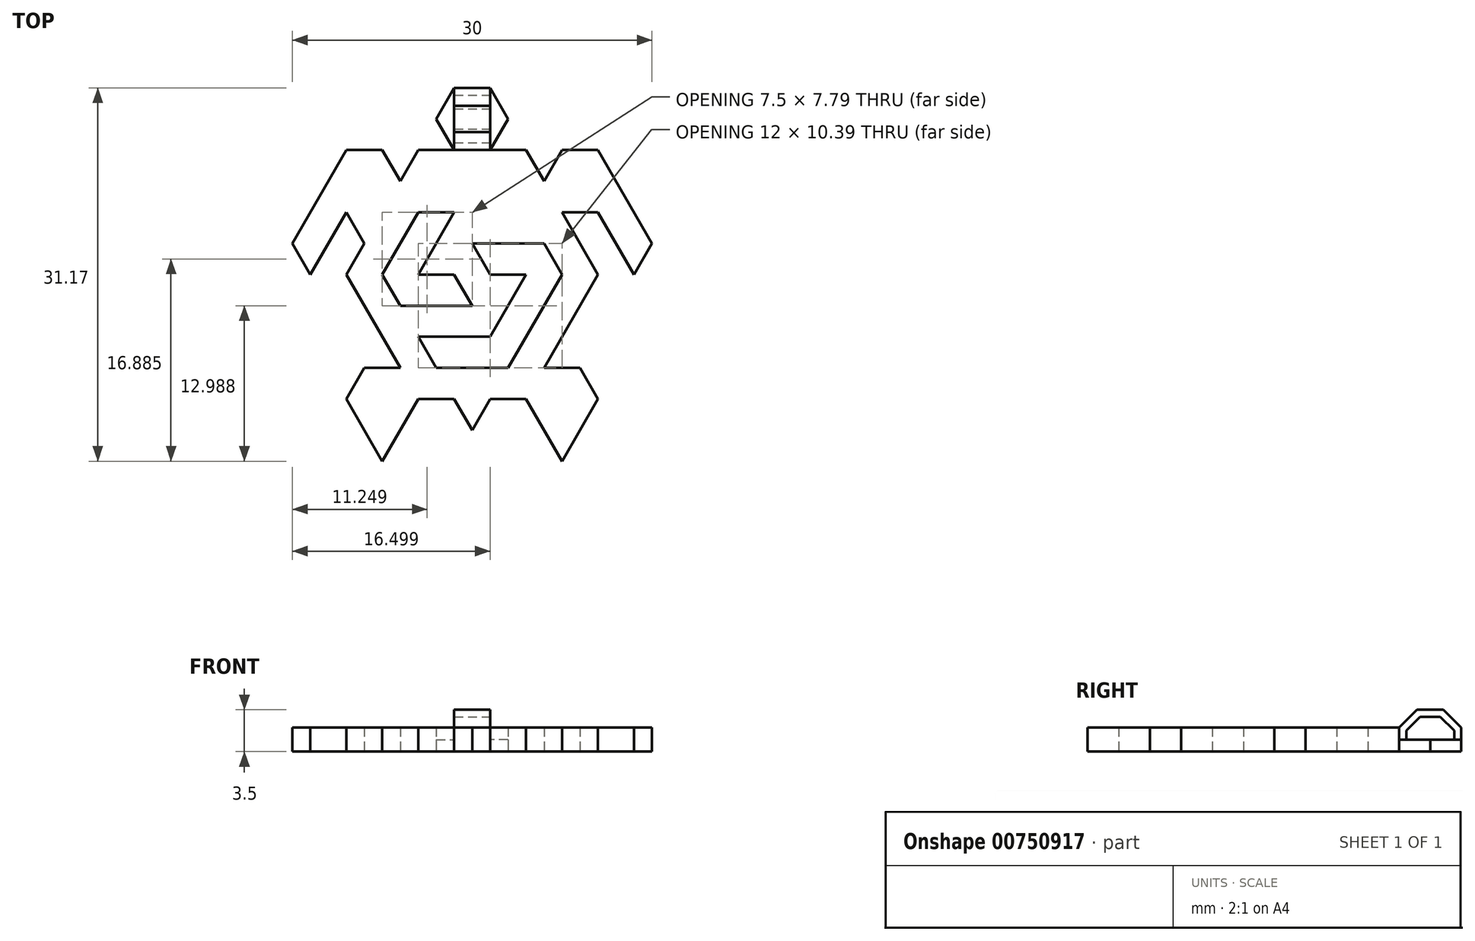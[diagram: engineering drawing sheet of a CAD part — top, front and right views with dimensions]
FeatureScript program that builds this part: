
annotation { "Feature Type Name" : "Feature", "Feature Type Description" : "" }
export const myFeature = defineFeature(function(context is Context, id is Id, definition is map)
    precondition{}
    {
        {
            var Q0;
            Q0=qCreatedBy(makeId("Top.planeOp"),FACE);
            var sketch = newSketch(context, id + "F0", { "sketchPlane" : qUnion([Q0])});
            skLineSegment(sketch, "E0", {"start": v(-15.95, 6.9) * mm, "end": v(-12.95, 6.9) * mm});
            skLineSegment(sketch, "E1", {"start": v(-12.95, 6.9) * mm, "end": v(-14.45, 9.5) * mm});
            skLineSegment(sketch, "E2", {"start": v(-14.45, 9.5) * mm, "end": v(-15.95, 6.9) * mm});
            skLineSegment(sketch, "E3", {"start": v(-14.45, 9.5) * mm, "end": v(-11.45, 9.5) * mm});
            skLineSegment(sketch, "E4", {"start": v(-11.45, 9.5) * mm, "end": v(-12.95, 6.9) * mm});
            skLineSegment(sketch, "E5", {"start": v(-11.45, 9.5) * mm, "end": v(-12.95, 12.1) * mm});
            skLineSegment(sketch, "E6", {"start": v(-14.45, 9.5) * mm, "end": v(-12.95, 12.1) * mm});
            skLineSegment(sketch, "E7", {"start": v(-12.95, 12.1) * mm, "end": v(-9.95, 12.1) * mm});
            skLineSegment(sketch, "E8", {"start": v(-9.95, 12.1) * mm, "end": v(-11.45, 9.5) * mm});
            skLineSegment(sketch, "E9.0.1.0", {"start": v(-15.95, 12.1) * mm, "end": v(-12.95, 12.1) * mm});
            skLineSegment(sketch, "E9.0.1.1", {"start": v(-14.45, 14.69) * mm, "end": v(-15.95, 12.1) * mm});
            skLineSegment(sketch, "E9.0.1.2", {"start": v(-12.95, 12.1) * mm, "end": v(-14.45, 14.69) * mm});
            skLineSegment(sketch, "E9.0.1.3", {"start": v(-14.45, 14.69) * mm, "end": v(-11.45, 14.69) * mm});
            skLineSegment(sketch, "E9.0.1.4", {"start": v(-14.45, 14.69) * mm, "end": v(-12.95, 17.29) * mm});
            skLineSegment(sketch, "E9.0.1.5", {"start": v(-11.45, 14.69) * mm, "end": v(-12.95, 17.29) * mm});
            skLineSegment(sketch, "E9.0.2.0", {"start": v(-15.95, 17.29) * mm, "end": v(-12.95, 17.29) * mm});
            skLineSegment(sketch, "E9.0.2.1", {"start": v(-14.45, 19.89) * mm, "end": v(-15.95, 17.29) * mm});
            skLineSegment(sketch, "E9.0.2.2", {"start": v(-12.95, 17.29) * mm, "end": v(-14.45, 19.89) * mm});
            skLineSegment(sketch, "E9.0.2.3", {"start": v(-14.45, 19.89) * mm, "end": v(-11.45, 19.89) * mm});
            skLineSegment(sketch, "E9.0.2.4", {"start": v(-14.45, 19.89) * mm, "end": v(-12.95, 22.48) * mm});
            skLineSegment(sketch, "E9.0.2.5", {"start": v(-11.45, 19.89) * mm, "end": v(-12.95, 22.48) * mm});
            skLineSegment(sketch, "E9.0.3.0", {"start": v(-15.95, 22.48) * mm, "end": v(-12.95, 22.48) * mm});
            skLineSegment(sketch, "E9.0.3.1", {"start": v(-14.45, 25.08) * mm, "end": v(-15.95, 22.48) * mm});
            skLineSegment(sketch, "E9.0.3.2", {"start": v(-12.95, 22.48) * mm, "end": v(-14.45, 25.08) * mm});
            skLineSegment(sketch, "E9.0.3.3", {"start": v(-14.45, 25.08) * mm, "end": v(-11.45, 25.08) * mm});
            skLineSegment(sketch, "E9.0.3.4", {"start": v(-14.45, 25.08) * mm, "end": v(-12.95, 27.68) * mm});
            skLineSegment(sketch, "E9.0.3.5", {"start": v(-11.45, 25.08) * mm, "end": v(-12.95, 27.68) * mm});
            skLineSegment(sketch, "E9.0.4.0", {"start": v(-15.95, 27.68) * mm, "end": v(-12.95, 27.68) * mm});
            skLineSegment(sketch, "E9.0.4.1", {"start": v(-14.45, 30.28) * mm, "end": v(-15.95, 27.68) * mm});
            skLineSegment(sketch, "E9.0.4.2", {"start": v(-12.95, 27.68) * mm, "end": v(-14.45, 30.28) * mm});
            skLineSegment(sketch, "E9.0.4.3", {"start": v(-14.45, 30.28) * mm, "end": v(-11.45, 30.28) * mm});
            skLineSegment(sketch, "E9.0.4.4", {"start": v(-14.45, 30.28) * mm, "end": v(-12.95, 32.88) * mm});
            skLineSegment(sketch, "E9.0.4.5", {"start": v(-11.45, 30.28) * mm, "end": v(-12.95, 32.88) * mm});
            skLineSegment(sketch, "E9.0.5.0", {"start": v(-15.95, 32.88) * mm, "end": v(-12.95, 32.88) * mm});
            skLineSegment(sketch, "E9.0.5.1", {"start": v(-14.45, 35.47) * mm, "end": v(-15.95, 32.88) * mm});
            skLineSegment(sketch, "E9.0.5.2", {"start": v(-12.95, 32.88) * mm, "end": v(-14.45, 35.47) * mm});
            skLineSegment(sketch, "E9.0.5.3", {"start": v(-14.45, 35.47) * mm, "end": v(-11.45, 35.47) * mm});
            skLineSegment(sketch, "E9.0.5.4", {"start": v(-14.45, 35.47) * mm, "end": v(-12.95, 38.07) * mm});
            skLineSegment(sketch, "E9.0.5.5", {"start": v(-11.45, 35.47) * mm, "end": v(-12.95, 38.07) * mm});
            skLineSegment(sketch, "E9.0.6.0", {"start": v(-15.95, 38.07) * mm, "end": v(-12.95, 38.07) * mm});
            skLineSegment(sketch, "E9.0.6.1", {"start": v(-14.45, 40.67) * mm, "end": v(-15.95, 38.07) * mm});
            skLineSegment(sketch, "E9.0.6.2", {"start": v(-12.95, 38.07) * mm, "end": v(-14.45, 40.67) * mm});
            skLineSegment(sketch, "E9.0.6.3", {"start": v(-14.45, 40.67) * mm, "end": v(-11.45, 40.67) * mm});
            skLineSegment(sketch, "E9.0.6.4", {"start": v(-14.45, 40.67) * mm, "end": v(-12.95, 43.27) * mm});
            skLineSegment(sketch, "E9.0.6.5", {"start": v(-11.45, 40.67) * mm, "end": v(-12.95, 43.27) * mm});
            skLineSegment(sketch, "E9.0.7.0", {"start": v(-15.95, 43.27) * mm, "end": v(-12.95, 43.27) * mm});
            skLineSegment(sketch, "E9.0.7.1", {"start": v(-14.45, 45.87) * mm, "end": v(-15.95, 43.27) * mm});
            skLineSegment(sketch, "E9.0.7.2", {"start": v(-12.95, 43.27) * mm, "end": v(-14.45, 45.87) * mm});
            skLineSegment(sketch, "E9.0.7.3", {"start": v(-14.45, 45.87) * mm, "end": v(-11.45, 45.87) * mm});
            skLineSegment(sketch, "E9.0.7.4", {"start": v(-14.45, 45.87) * mm, "end": v(-12.95, 48.46) * mm});
            skLineSegment(sketch, "E9.0.7.5", {"start": v(-11.45, 45.87) * mm, "end": v(-12.95, 48.46) * mm});
            skLineSegment(sketch, "E9.0.8.0", {"start": v(-15.95, 48.46) * mm, "end": v(-12.95, 48.46) * mm});
            skLineSegment(sketch, "E9.0.8.1", {"start": v(-14.45, 51.06) * mm, "end": v(-15.95, 48.46) * mm});
            skLineSegment(sketch, "E9.0.8.2", {"start": v(-12.95, 48.46) * mm, "end": v(-14.45, 51.06) * mm});
            skLineSegment(sketch, "E9.0.8.3", {"start": v(-14.45, 51.06) * mm, "end": v(-11.45, 51.06) * mm});
            skLineSegment(sketch, "E9.0.8.4", {"start": v(-14.45, 51.06) * mm, "end": v(-12.95, 53.66) * mm});
            skLineSegment(sketch, "E9.0.8.5", {"start": v(-11.45, 51.06) * mm, "end": v(-12.95, 53.66) * mm});
            skLineSegment(sketch, "E9.0.9.0", {"start": v(-15.95, 53.66) * mm, "end": v(-12.95, 53.66) * mm});
            skLineSegment(sketch, "E9.0.9.1", {"start": v(-14.45, 56.26) * mm, "end": v(-15.95, 53.66) * mm});
            skLineSegment(sketch, "E9.0.9.2", {"start": v(-12.95, 53.66) * mm, "end": v(-14.45, 56.26) * mm});
            skLineSegment(sketch, "E9.0.9.3", {"start": v(-14.45, 56.26) * mm, "end": v(-11.45, 56.26) * mm});
            skLineSegment(sketch, "E9.0.9.4", {"start": v(-14.45, 56.26) * mm, "end": v(-12.95, 58.86) * mm});
            skLineSegment(sketch, "E9.0.9.5", {"start": v(-11.45, 56.26) * mm, "end": v(-12.95, 58.86) * mm});
            skLineSegment(sketch, "E9.1.0.0", {"start": v(-12.95, 6.9) * mm, "end": v(-9.95, 6.9) * mm});
            skLineSegment(sketch, "E9.1.0.2", {"start": v(-9.95, 6.9) * mm, "end": v(-11.45, 9.5) * mm});
            skLineSegment(sketch, "E9.1.0.3", {"start": v(-11.45, 9.5) * mm, "end": v(-8.45, 9.5) * mm});
            skLineSegment(sketch, "E9.1.0.4", {"start": v(-11.45, 9.5) * mm, "end": v(-9.95, 12.1) * mm});
            skLineSegment(sketch, "E9.1.0.5", {"start": v(-8.45, 9.5) * mm, "end": v(-9.95, 12.1) * mm});
            skLineSegment(sketch, "E9.1.1.1", {"start": v(-11.45, 14.69) * mm, "end": v(-12.95, 12.1) * mm});
            skLineSegment(sketch, "E9.1.1.2", {"start": v(-9.95, 12.1) * mm, "end": v(-11.45, 14.69) * mm});
            skLineSegment(sketch, "E9.1.1.3", {"start": v(-11.45, 14.69) * mm, "end": v(-8.45, 14.69) * mm});
            skLineSegment(sketch, "E9.1.1.4", {"start": v(-11.45, 14.69) * mm, "end": v(-9.95, 17.29) * mm});
            skLineSegment(sketch, "E9.1.1.5", {"start": v(-8.45, 14.69) * mm, "end": v(-9.95, 17.29) * mm});
            skLineSegment(sketch, "E9.1.2.0", {"start": v(-12.95, 17.29) * mm, "end": v(-9.95, 17.29) * mm});
            skLineSegment(sketch, "E9.1.2.1", {"start": v(-11.45, 19.89) * mm, "end": v(-12.95, 17.29) * mm});
            skLineSegment(sketch, "E9.1.2.2", {"start": v(-9.95, 17.29) * mm, "end": v(-11.45, 19.89) * mm});
            skLineSegment(sketch, "E9.1.2.3", {"start": v(-11.45, 19.89) * mm, "end": v(-8.45, 19.89) * mm});
            skLineSegment(sketch, "E9.1.2.4", {"start": v(-11.45, 19.89) * mm, "end": v(-9.95, 22.48) * mm});
            skLineSegment(sketch, "E9.1.2.5", {"start": v(-8.45, 19.89) * mm, "end": v(-9.95, 22.48) * mm});
            skLineSegment(sketch, "E9.1.3.0", {"start": v(-12.95, 22.48) * mm, "end": v(-9.95, 22.48) * mm});
            skLineSegment(sketch, "E9.1.3.1", {"start": v(-11.45, 25.08) * mm, "end": v(-12.95, 22.48) * mm});
            skLineSegment(sketch, "E9.1.3.2", {"start": v(-9.95, 22.48) * mm, "end": v(-11.45, 25.08) * mm});
            skLineSegment(sketch, "E9.1.3.3", {"start": v(-11.45, 25.08) * mm, "end": v(-8.45, 25.08) * mm});
            skLineSegment(sketch, "E9.1.3.4", {"start": v(-11.45, 25.08) * mm, "end": v(-9.95, 27.68) * mm});
            skLineSegment(sketch, "E9.1.3.5", {"start": v(-8.45, 25.08) * mm, "end": v(-9.95, 27.68) * mm});
            skLineSegment(sketch, "E9.1.4.0", {"start": v(-12.95, 27.68) * mm, "end": v(-9.95, 27.68) * mm});
            skLineSegment(sketch, "E9.1.4.1", {"start": v(-11.45, 30.28) * mm, "end": v(-12.95, 27.68) * mm});
            skLineSegment(sketch, "E9.1.4.2", {"start": v(-9.95, 27.68) * mm, "end": v(-11.45, 30.28) * mm});
            skLineSegment(sketch, "E9.1.4.3", {"start": v(-11.45, 30.28) * mm, "end": v(-8.45, 30.28) * mm});
            skLineSegment(sketch, "E9.1.4.4", {"start": v(-11.45, 30.28) * mm, "end": v(-9.95, 32.88) * mm});
            skLineSegment(sketch, "E9.1.4.5", {"start": v(-8.45, 30.28) * mm, "end": v(-9.95, 32.88) * mm});
            skLineSegment(sketch, "E9.1.5.0", {"start": v(-12.95, 32.88) * mm, "end": v(-9.95, 32.88) * mm});
            skLineSegment(sketch, "E9.1.5.1", {"start": v(-11.45, 35.47) * mm, "end": v(-12.95, 32.88) * mm});
            skLineSegment(sketch, "E9.1.5.2", {"start": v(-9.95, 32.88) * mm, "end": v(-11.45, 35.47) * mm});
            skLineSegment(sketch, "E9.1.5.3", {"start": v(-11.45, 35.47) * mm, "end": v(-8.45, 35.47) * mm});
            skLineSegment(sketch, "E9.1.5.4", {"start": v(-11.45, 35.47) * mm, "end": v(-9.95, 38.07) * mm});
            skLineSegment(sketch, "E9.1.5.5", {"start": v(-8.45, 35.47) * mm, "end": v(-9.95, 38.07) * mm});
            skLineSegment(sketch, "E9.1.6.0", {"start": v(-12.95, 38.07) * mm, "end": v(-9.95, 38.07) * mm});
            skLineSegment(sketch, "E9.1.6.1", {"start": v(-11.45, 40.67) * mm, "end": v(-12.95, 38.07) * mm});
            skLineSegment(sketch, "E9.1.6.2", {"start": v(-9.95, 38.07) * mm, "end": v(-11.45, 40.67) * mm});
            skLineSegment(sketch, "E9.1.6.3", {"start": v(-11.45, 40.67) * mm, "end": v(-8.45, 40.67) * mm});
            skLineSegment(sketch, "E9.1.6.4", {"start": v(-11.45, 40.67) * mm, "end": v(-9.95, 43.27) * mm});
            skLineSegment(sketch, "E9.1.6.5", {"start": v(-8.45, 40.67) * mm, "end": v(-9.95, 43.27) * mm});
            skLineSegment(sketch, "E9.1.7.0", {"start": v(-12.95, 43.27) * mm, "end": v(-9.95, 43.27) * mm});
            skLineSegment(sketch, "E9.1.7.1", {"start": v(-11.45, 45.87) * mm, "end": v(-12.95, 43.27) * mm});
            skLineSegment(sketch, "E9.1.7.2", {"start": v(-9.95, 43.27) * mm, "end": v(-11.45, 45.87) * mm});
            skLineSegment(sketch, "E9.1.7.3", {"start": v(-11.45, 45.87) * mm, "end": v(-8.45, 45.87) * mm});
            skLineSegment(sketch, "E9.1.7.4", {"start": v(-11.45, 45.87) * mm, "end": v(-9.95, 48.46) * mm});
            skLineSegment(sketch, "E9.1.7.5", {"start": v(-8.45, 45.87) * mm, "end": v(-9.95, 48.46) * mm});
            skLineSegment(sketch, "E9.1.8.0", {"start": v(-12.95, 48.46) * mm, "end": v(-9.95, 48.46) * mm});
            skLineSegment(sketch, "E9.1.8.1", {"start": v(-11.45, 51.06) * mm, "end": v(-12.95, 48.46) * mm});
            skLineSegment(sketch, "E9.1.8.2", {"start": v(-9.95, 48.46) * mm, "end": v(-11.45, 51.06) * mm});
            skLineSegment(sketch, "E9.1.8.3", {"start": v(-11.45, 51.06) * mm, "end": v(-8.45, 51.06) * mm});
            skLineSegment(sketch, "E9.1.8.4", {"start": v(-11.45, 51.06) * mm, "end": v(-9.95, 53.66) * mm});
            skLineSegment(sketch, "E9.1.8.5", {"start": v(-8.45, 51.06) * mm, "end": v(-9.95, 53.66) * mm});
            skLineSegment(sketch, "E9.1.9.0", {"start": v(-12.95, 53.66) * mm, "end": v(-9.95, 53.66) * mm});
            skLineSegment(sketch, "E9.1.9.1", {"start": v(-11.45, 56.26) * mm, "end": v(-12.95, 53.66) * mm});
            skLineSegment(sketch, "E9.1.9.2", {"start": v(-9.95, 53.66) * mm, "end": v(-11.45, 56.26) * mm});
            skLineSegment(sketch, "E9.1.9.3", {"start": v(-11.45, 56.26) * mm, "end": v(-8.45, 56.26) * mm});
            skLineSegment(sketch, "E9.1.9.4", {"start": v(-11.45, 56.26) * mm, "end": v(-9.95, 58.86) * mm});
            skLineSegment(sketch, "E9.1.9.5", {"start": v(-8.45, 56.26) * mm, "end": v(-9.95, 58.86) * mm});
            skLineSegment(sketch, "E9.2.0.0", {"start": v(-9.95, 6.9) * mm, "end": v(-6.95, 6.9) * mm});
            skLineSegment(sketch, "E9.2.0.1", {"start": v(-8.45, 9.5) * mm, "end": v(-9.95, 6.9) * mm});
            skLineSegment(sketch, "E9.2.0.2", {"start": v(-6.95, 6.9) * mm, "end": v(-8.45, 9.5) * mm});
            skLineSegment(sketch, "E9.2.0.3", {"start": v(-8.45, 9.5) * mm, "end": v(-5.45, 9.5) * mm});
            skLineSegment(sketch, "E9.2.0.4", {"start": v(-8.45, 9.5) * mm, "end": v(-6.95, 12.1) * mm});
            skLineSegment(sketch, "E9.2.0.5", {"start": v(-5.45, 9.5) * mm, "end": v(-6.95, 12.1) * mm});
            skLineSegment(sketch, "E9.2.1.0", {"start": v(-9.95, 12.1) * mm, "end": v(-6.95, 12.1) * mm});
            skLineSegment(sketch, "E9.2.1.1", {"start": v(-8.45, 14.69) * mm, "end": v(-9.95, 12.1) * mm});
            skLineSegment(sketch, "E9.2.1.2", {"start": v(-6.95, 12.1) * mm, "end": v(-8.45, 14.69) * mm});
            skLineSegment(sketch, "E9.2.1.3", {"start": v(-8.45, 14.69) * mm, "end": v(-5.45, 14.69) * mm});
            skLineSegment(sketch, "E9.2.1.4", {"start": v(-8.45, 14.69) * mm, "end": v(-6.95, 17.29) * mm});
            skLineSegment(sketch, "E9.2.1.5", {"start": v(-5.45, 14.69) * mm, "end": v(-6.95, 17.29) * mm});
            skLineSegment(sketch, "E9.2.2.0", {"start": v(-9.95, 17.29) * mm, "end": v(-6.95, 17.29) * mm});
            skLineSegment(sketch, "E9.2.2.1", {"start": v(-8.45, 19.89) * mm, "end": v(-9.95, 17.29) * mm});
            skLineSegment(sketch, "E9.2.2.2", {"start": v(-6.95, 17.29) * mm, "end": v(-8.45, 19.89) * mm});
            skLineSegment(sketch, "E9.2.2.3", {"start": v(-8.45, 19.89) * mm, "end": v(-5.45, 19.89) * mm});
            skLineSegment(sketch, "E9.2.2.4", {"start": v(-8.45, 19.89) * mm, "end": v(-6.95, 22.48) * mm});
            skLineSegment(sketch, "E9.2.2.5", {"start": v(-5.45, 19.89) * mm, "end": v(-6.95, 22.48) * mm});
            skLineSegment(sketch, "E9.2.3.0", {"start": v(-9.95, 22.48) * mm, "end": v(-6.95, 22.48) * mm});
            skLineSegment(sketch, "E9.2.3.1", {"start": v(-8.45, 25.08) * mm, "end": v(-9.95, 22.48) * mm});
            skLineSegment(sketch, "E9.2.3.2", {"start": v(-6.95, 22.48) * mm, "end": v(-8.45, 25.08) * mm});
            skLineSegment(sketch, "E9.2.3.3", {"start": v(-8.45, 25.08) * mm, "end": v(-5.45, 25.08) * mm});
            skLineSegment(sketch, "E9.2.3.4", {"start": v(-8.45, 25.08) * mm, "end": v(-6.95, 27.68) * mm});
            skLineSegment(sketch, "E9.2.3.5", {"start": v(-5.45, 25.08) * mm, "end": v(-6.95, 27.68) * mm});
            skLineSegment(sketch, "E9.2.4.0", {"start": v(-9.95, 27.68) * mm, "end": v(-6.95, 27.68) * mm});
            skLineSegment(sketch, "E9.2.4.1", {"start": v(-8.45, 30.28) * mm, "end": v(-9.95, 27.68) * mm});
            skLineSegment(sketch, "E9.2.4.2", {"start": v(-6.95, 27.68) * mm, "end": v(-8.45, 30.28) * mm});
            skLineSegment(sketch, "E9.2.4.3", {"start": v(-8.45, 30.28) * mm, "end": v(-5.45, 30.28) * mm});
            skLineSegment(sketch, "E9.2.4.4", {"start": v(-8.45, 30.28) * mm, "end": v(-6.95, 32.88) * mm});
            skLineSegment(sketch, "E9.2.4.5", {"start": v(-5.45, 30.28) * mm, "end": v(-6.95, 32.88) * mm});
            skLineSegment(sketch, "E9.2.5.0", {"start": v(-9.95, 32.88) * mm, "end": v(-6.95, 32.88) * mm});
            skLineSegment(sketch, "E9.2.5.1", {"start": v(-8.45, 35.47) * mm, "end": v(-9.95, 32.88) * mm});
            skLineSegment(sketch, "E9.2.5.2", {"start": v(-6.95, 32.88) * mm, "end": v(-8.45, 35.47) * mm});
            skLineSegment(sketch, "E9.2.5.3", {"start": v(-8.45, 35.47) * mm, "end": v(-5.45, 35.47) * mm});
            skLineSegment(sketch, "E9.2.5.4", {"start": v(-8.45, 35.47) * mm, "end": v(-6.95, 38.07) * mm});
            skLineSegment(sketch, "E9.2.5.5", {"start": v(-5.45, 35.47) * mm, "end": v(-6.95, 38.07) * mm});
            skLineSegment(sketch, "E9.2.6.0", {"start": v(-9.95, 38.07) * mm, "end": v(-6.95, 38.07) * mm});
            skLineSegment(sketch, "E9.2.6.1", {"start": v(-8.45, 40.67) * mm, "end": v(-9.95, 38.07) * mm});
            skLineSegment(sketch, "E9.2.6.2", {"start": v(-6.95, 38.07) * mm, "end": v(-8.45, 40.67) * mm});
            skLineSegment(sketch, "E9.2.6.3", {"start": v(-8.45, 40.67) * mm, "end": v(-5.45, 40.67) * mm});
            skLineSegment(sketch, "E9.2.6.4", {"start": v(-8.45, 40.67) * mm, "end": v(-6.95, 43.27) * mm});
            skLineSegment(sketch, "E9.2.6.5", {"start": v(-5.45, 40.67) * mm, "end": v(-6.95, 43.27) * mm});
            skLineSegment(sketch, "E9.2.7.0", {"start": v(-9.95, 43.27) * mm, "end": v(-6.95, 43.27) * mm});
            skLineSegment(sketch, "E9.2.7.1", {"start": v(-8.45, 45.87) * mm, "end": v(-9.95, 43.27) * mm});
            skLineSegment(sketch, "E9.2.7.2", {"start": v(-6.95, 43.27) * mm, "end": v(-8.45, 45.87) * mm});
            skLineSegment(sketch, "E9.2.7.3", {"start": v(-8.45, 45.87) * mm, "end": v(-5.45, 45.87) * mm});
            skLineSegment(sketch, "E9.2.7.4", {"start": v(-8.45, 45.87) * mm, "end": v(-6.95, 48.46) * mm});
            skLineSegment(sketch, "E9.2.7.5", {"start": v(-5.45, 45.87) * mm, "end": v(-6.95, 48.46) * mm});
            skLineSegment(sketch, "E9.2.8.0", {"start": v(-9.95, 48.46) * mm, "end": v(-6.95, 48.46) * mm});
            skLineSegment(sketch, "E9.2.8.1", {"start": v(-8.45, 51.06) * mm, "end": v(-9.95, 48.46) * mm});
            skLineSegment(sketch, "E9.2.8.2", {"start": v(-6.95, 48.46) * mm, "end": v(-8.45, 51.06) * mm});
            skLineSegment(sketch, "E9.2.8.3", {"start": v(-8.45, 51.06) * mm, "end": v(-5.45, 51.06) * mm});
            skLineSegment(sketch, "E9.2.8.4", {"start": v(-8.45, 51.06) * mm, "end": v(-6.95, 53.66) * mm});
            skLineSegment(sketch, "E9.2.8.5", {"start": v(-5.45, 51.06) * mm, "end": v(-6.95, 53.66) * mm});
            skLineSegment(sketch, "E9.2.9.0", {"start": v(-9.95, 53.66) * mm, "end": v(-6.95, 53.66) * mm});
            skLineSegment(sketch, "E9.2.9.1", {"start": v(-8.45, 56.26) * mm, "end": v(-9.95, 53.66) * mm});
            skLineSegment(sketch, "E9.2.9.2", {"start": v(-6.95, 53.66) * mm, "end": v(-8.45, 56.26) * mm});
            skLineSegment(sketch, "E9.2.9.3", {"start": v(-8.45, 56.26) * mm, "end": v(-5.45, 56.26) * mm});
            skLineSegment(sketch, "E9.2.9.4", {"start": v(-8.45, 56.26) * mm, "end": v(-6.95, 58.86) * mm});
            skLineSegment(sketch, "E9.2.9.5", {"start": v(-5.45, 56.26) * mm, "end": v(-6.95, 58.86) * mm});
            skLineSegment(sketch, "E9.3.0.0", {"start": v(-6.95, 6.9) * mm, "end": v(-3.95, 6.9) * mm});
            skLineSegment(sketch, "E9.3.0.1", {"start": v(-5.45, 9.5) * mm, "end": v(-6.95, 6.9) * mm});
            skLineSegment(sketch, "E9.3.0.2", {"start": v(-3.95, 6.9) * mm, "end": v(-5.45, 9.5) * mm});
            skLineSegment(sketch, "E9.3.0.3", {"start": v(-5.45, 9.5) * mm, "end": v(-2.45, 9.5) * mm});
            skLineSegment(sketch, "E9.3.0.4", {"start": v(-5.45, 9.5) * mm, "end": v(-3.95, 12.1) * mm});
            skLineSegment(sketch, "E9.3.0.5", {"start": v(-2.45, 9.5) * mm, "end": v(-3.95, 12.1) * mm});
            skLineSegment(sketch, "E9.3.1.0", {"start": v(-6.95, 12.1) * mm, "end": v(-3.95, 12.1) * mm});
            skLineSegment(sketch, "E9.3.1.1", {"start": v(-5.45, 14.69) * mm, "end": v(-6.95, 12.1) * mm});
            skLineSegment(sketch, "E9.3.1.2", {"start": v(-3.95, 12.1) * mm, "end": v(-5.45, 14.69) * mm});
            skLineSegment(sketch, "E9.3.1.3", {"start": v(-5.45, 14.69) * mm, "end": v(-2.45, 14.69) * mm});
            skLineSegment(sketch, "E9.3.1.4", {"start": v(-5.45, 14.69) * mm, "end": v(-3.95, 17.29) * mm});
            skLineSegment(sketch, "E9.3.1.5", {"start": v(-2.45, 14.69) * mm, "end": v(-3.95, 17.29) * mm});
            skLineSegment(sketch, "E9.3.2.0", {"start": v(-6.95, 17.29) * mm, "end": v(-3.95, 17.29) * mm});
            skLineSegment(sketch, "E9.3.2.1", {"start": v(-5.45, 19.89) * mm, "end": v(-6.95, 17.29) * mm});
            skLineSegment(sketch, "E9.3.2.2", {"start": v(-3.95, 17.29) * mm, "end": v(-5.45, 19.89) * mm});
            skLineSegment(sketch, "E9.3.2.3", {"start": v(-5.45, 19.89) * mm, "end": v(-2.45, 19.89) * mm});
            skLineSegment(sketch, "E9.3.2.4", {"start": v(-5.45, 19.89) * mm, "end": v(-3.95, 22.48) * mm});
            skLineSegment(sketch, "E9.3.2.5", {"start": v(-2.45, 19.89) * mm, "end": v(-3.95, 22.48) * mm});
            skLineSegment(sketch, "E9.3.3.0", {"start": v(-6.95, 22.48) * mm, "end": v(-3.95, 22.48) * mm});
            skLineSegment(sketch, "E9.3.3.1", {"start": v(-5.45, 25.08) * mm, "end": v(-6.95, 22.48) * mm});
            skLineSegment(sketch, "E9.3.3.2", {"start": v(-3.95, 22.48) * mm, "end": v(-5.45, 25.08) * mm});
            skLineSegment(sketch, "E9.3.3.3", {"start": v(-5.45, 25.08) * mm, "end": v(-2.45, 25.08) * mm});
            skLineSegment(sketch, "E9.3.3.4", {"start": v(-5.45, 25.08) * mm, "end": v(-3.95, 27.68) * mm});
            skLineSegment(sketch, "E9.3.3.5", {"start": v(-2.45, 25.08) * mm, "end": v(-3.95, 27.68) * mm});
            skLineSegment(sketch, "E9.3.4.0", {"start": v(-6.95, 27.68) * mm, "end": v(-3.95, 27.68) * mm});
            skLineSegment(sketch, "E9.3.4.1", {"start": v(-5.45, 30.28) * mm, "end": v(-6.95, 27.68) * mm});
            skLineSegment(sketch, "E9.3.4.2", {"start": v(-3.95, 27.68) * mm, "end": v(-5.45, 30.28) * mm});
            skLineSegment(sketch, "E9.3.4.3", {"start": v(-5.45, 30.28) * mm, "end": v(-2.45, 30.28) * mm});
            skLineSegment(sketch, "E9.3.4.4", {"start": v(-5.45, 30.28) * mm, "end": v(-3.95, 32.88) * mm});
            skLineSegment(sketch, "E9.3.4.5", {"start": v(-2.45, 30.28) * mm, "end": v(-3.95, 32.88) * mm});
            skLineSegment(sketch, "E9.3.5.0", {"start": v(-6.95, 32.88) * mm, "end": v(-3.95, 32.88) * mm});
            skLineSegment(sketch, "E9.3.5.1", {"start": v(-5.45, 35.47) * mm, "end": v(-6.95, 32.88) * mm});
            skLineSegment(sketch, "E9.3.5.2", {"start": v(-3.95, 32.88) * mm, "end": v(-5.45, 35.47) * mm});
            skLineSegment(sketch, "E9.3.5.3", {"start": v(-5.45, 35.47) * mm, "end": v(-2.45, 35.47) * mm});
            skLineSegment(sketch, "E9.3.5.4", {"start": v(-5.45, 35.47) * mm, "end": v(-3.95, 38.07) * mm});
            skLineSegment(sketch, "E9.3.5.5", {"start": v(-2.45, 35.47) * mm, "end": v(-3.95, 38.07) * mm});
            skLineSegment(sketch, "E9.3.6.0", {"start": v(-6.95, 38.07) * mm, "end": v(-3.95, 38.07) * mm});
            skLineSegment(sketch, "E9.3.6.1", {"start": v(-5.45, 40.67) * mm, "end": v(-6.95, 38.07) * mm});
            skLineSegment(sketch, "E9.3.6.2", {"start": v(-3.95, 38.07) * mm, "end": v(-5.45, 40.67) * mm});
            skLineSegment(sketch, "E9.3.6.3", {"start": v(-5.45, 40.67) * mm, "end": v(-2.45, 40.67) * mm});
            skLineSegment(sketch, "E9.3.6.4", {"start": v(-5.45, 40.67) * mm, "end": v(-3.95, 43.27) * mm});
            skLineSegment(sketch, "E9.3.6.5", {"start": v(-2.45, 40.67) * mm, "end": v(-3.95, 43.27) * mm});
            skLineSegment(sketch, "E9.3.7.0", {"start": v(-6.95, 43.27) * mm, "end": v(-3.95, 43.27) * mm});
            skLineSegment(sketch, "E9.3.7.1", {"start": v(-5.45, 45.87) * mm, "end": v(-6.95, 43.27) * mm});
            skLineSegment(sketch, "E9.3.7.2", {"start": v(-3.95, 43.27) * mm, "end": v(-5.45, 45.87) * mm});
            skLineSegment(sketch, "E9.3.7.3", {"start": v(-5.45, 45.87) * mm, "end": v(-2.45, 45.87) * mm});
            skLineSegment(sketch, "E9.3.7.4", {"start": v(-5.45, 45.87) * mm, "end": v(-3.95, 48.46) * mm});
            skLineSegment(sketch, "E9.3.7.5", {"start": v(-2.45, 45.87) * mm, "end": v(-3.95, 48.46) * mm});
            skLineSegment(sketch, "E9.3.8.0", {"start": v(-6.95, 48.46) * mm, "end": v(-3.95, 48.46) * mm});
            skLineSegment(sketch, "E9.3.8.1", {"start": v(-5.45, 51.06) * mm, "end": v(-6.95, 48.46) * mm});
            skLineSegment(sketch, "E9.3.8.2", {"start": v(-3.95, 48.46) * mm, "end": v(-5.45, 51.06) * mm});
            skLineSegment(sketch, "E9.3.8.3", {"start": v(-5.45, 51.06) * mm, "end": v(-2.45, 51.06) * mm});
            skLineSegment(sketch, "E9.3.8.4", {"start": v(-5.45, 51.06) * mm, "end": v(-3.95, 53.66) * mm});
            skLineSegment(sketch, "E9.3.8.5", {"start": v(-2.45, 51.06) * mm, "end": v(-3.95, 53.66) * mm});
            skLineSegment(sketch, "E9.3.9.0", {"start": v(-6.95, 53.66) * mm, "end": v(-3.95, 53.66) * mm});
            skLineSegment(sketch, "E9.3.9.1", {"start": v(-5.45, 56.26) * mm, "end": v(-6.95, 53.66) * mm});
            skLineSegment(sketch, "E9.3.9.2", {"start": v(-3.95, 53.66) * mm, "end": v(-5.45, 56.26) * mm});
            skLineSegment(sketch, "E9.3.9.3", {"start": v(-5.45, 56.26) * mm, "end": v(-2.45, 56.26) * mm});
            skLineSegment(sketch, "E9.3.9.4", {"start": v(-5.45, 56.26) * mm, "end": v(-3.95, 58.86) * mm});
            skLineSegment(sketch, "E9.3.9.5", {"start": v(-2.45, 56.26) * mm, "end": v(-3.95, 58.86) * mm});
            skLineSegment(sketch, "E9.4.0.0", {"start": v(-3.95, 6.9) * mm, "end": v(-0.95, 6.9) * mm});
            skLineSegment(sketch, "E9.4.0.1", {"start": v(-2.45, 9.5) * mm, "end": v(-3.95, 6.9) * mm});
            skLineSegment(sketch, "E9.4.0.2", {"start": v(-0.95, 6.9) * mm, "end": v(-2.45, 9.5) * mm});
            skLineSegment(sketch, "E9.4.0.3", {"start": v(-2.45, 9.5) * mm, "end": v(0.55, 9.5) * mm});
            skLineSegment(sketch, "E9.4.0.4", {"start": v(-2.45, 9.5) * mm, "end": v(-0.95, 12.1) * mm});
            skLineSegment(sketch, "E9.4.0.5", {"start": v(0.55, 9.5) * mm, "end": v(-0.95, 12.1) * mm});
            skLineSegment(sketch, "E9.4.1.0", {"start": v(-3.95, 12.1) * mm, "end": v(-0.95, 12.1) * mm});
            skLineSegment(sketch, "E9.4.1.1", {"start": v(-2.45, 14.69) * mm, "end": v(-3.95, 12.1) * mm});
            skLineSegment(sketch, "E9.4.1.2", {"start": v(-0.95, 12.1) * mm, "end": v(-2.45, 14.69) * mm});
            skLineSegment(sketch, "E9.4.1.3", {"start": v(-2.45, 14.69) * mm, "end": v(0.55, 14.69) * mm});
            skLineSegment(sketch, "E9.4.1.4", {"start": v(-2.45, 14.69) * mm, "end": v(-0.95, 17.29) * mm});
            skLineSegment(sketch, "E9.4.1.5", {"start": v(0.55, 14.69) * mm, "end": v(-0.95, 17.29) * mm});
            skLineSegment(sketch, "E9.4.2.0", {"start": v(-3.95, 17.29) * mm, "end": v(-0.95, 17.29) * mm});
            skLineSegment(sketch, "E9.4.2.1", {"start": v(-2.45, 19.89) * mm, "end": v(-3.95, 17.29) * mm});
            skLineSegment(sketch, "E9.4.2.2", {"start": v(-0.95, 17.29) * mm, "end": v(-2.45, 19.89) * mm});
            skLineSegment(sketch, "E9.4.2.3", {"start": v(-2.45, 19.89) * mm, "end": v(0.55, 19.89) * mm});
            skLineSegment(sketch, "E9.4.2.4", {"start": v(-2.45, 19.89) * mm, "end": v(-0.95, 22.48) * mm});
            skLineSegment(sketch, "E9.4.2.5", {"start": v(0.55, 19.89) * mm, "end": v(-0.95, 22.48) * mm});
            skLineSegment(sketch, "E9.4.3.0", {"start": v(-3.95, 22.48) * mm, "end": v(-0.95, 22.48) * mm});
            skLineSegment(sketch, "E9.4.3.1", {"start": v(-2.45, 25.08) * mm, "end": v(-3.95, 22.48) * mm});
            skLineSegment(sketch, "E9.4.3.2", {"start": v(-0.95, 22.48) * mm, "end": v(-2.45, 25.08) * mm});
            skLineSegment(sketch, "E9.4.3.3", {"start": v(-2.45, 25.08) * mm, "end": v(0.55, 25.08) * mm});
            skLineSegment(sketch, "E9.4.3.4", {"start": v(-2.45, 25.08) * mm, "end": v(-0.95, 27.68) * mm});
            skLineSegment(sketch, "E9.4.3.5", {"start": v(0.55, 25.08) * mm, "end": v(-0.95, 27.68) * mm});
            skLineSegment(sketch, "E9.4.4.0", {"start": v(-3.95, 27.68) * mm, "end": v(-0.95, 27.68) * mm});
            skLineSegment(sketch, "E9.4.4.1", {"start": v(-2.45, 30.28) * mm, "end": v(-3.95, 27.68) * mm});
            skLineSegment(sketch, "E9.4.4.2", {"start": v(-0.95, 27.68) * mm, "end": v(-2.45, 30.28) * mm});
            skLineSegment(sketch, "E9.4.4.3", {"start": v(-2.45, 30.28) * mm, "end": v(0.55, 30.28) * mm});
            skLineSegment(sketch, "E9.4.4.4", {"start": v(-2.45, 30.28) * mm, "end": v(-0.95, 32.88) * mm});
            skLineSegment(sketch, "E9.4.4.5", {"start": v(0.55, 30.28) * mm, "end": v(-0.95, 32.88) * mm});
            skLineSegment(sketch, "E9.4.5.0", {"start": v(-3.95, 32.88) * mm, "end": v(-0.95, 32.88) * mm});
            skLineSegment(sketch, "E9.4.5.1", {"start": v(-2.45, 35.47) * mm, "end": v(-3.95, 32.88) * mm});
            skLineSegment(sketch, "E9.4.5.2", {"start": v(-0.95, 32.88) * mm, "end": v(-2.45, 35.47) * mm});
            skLineSegment(sketch, "E9.4.5.3", {"start": v(-2.45, 35.47) * mm, "end": v(0.55, 35.47) * mm});
            skLineSegment(sketch, "E9.4.5.4", {"start": v(-2.45, 35.47) * mm, "end": v(-0.95, 38.07) * mm});
            skLineSegment(sketch, "E9.4.5.5", {"start": v(0.55, 35.47) * mm, "end": v(-0.95, 38.07) * mm});
            skLineSegment(sketch, "E9.4.6.0", {"start": v(-3.95, 38.07) * mm, "end": v(-0.95, 38.07) * mm});
            skLineSegment(sketch, "E9.4.6.1", {"start": v(-2.45, 40.67) * mm, "end": v(-3.95, 38.07) * mm});
            skLineSegment(sketch, "E9.4.6.2", {"start": v(-0.95, 38.07) * mm, "end": v(-2.45, 40.67) * mm});
            skLineSegment(sketch, "E9.4.6.3", {"start": v(-2.45, 40.67) * mm, "end": v(0.55, 40.67) * mm});
            skLineSegment(sketch, "E9.4.6.4", {"start": v(-2.45, 40.67) * mm, "end": v(-0.95, 43.27) * mm});
            skLineSegment(sketch, "E9.4.6.5", {"start": v(0.55, 40.67) * mm, "end": v(-0.95, 43.27) * mm});
            skLineSegment(sketch, "E9.4.7.0", {"start": v(-3.95, 43.27) * mm, "end": v(-0.95, 43.27) * mm});
            skLineSegment(sketch, "E9.4.7.1", {"start": v(-2.45, 45.87) * mm, "end": v(-3.95, 43.27) * mm});
            skLineSegment(sketch, "E9.4.7.2", {"start": v(-0.95, 43.27) * mm, "end": v(-2.45, 45.87) * mm});
            skLineSegment(sketch, "E9.4.7.3", {"start": v(-2.45, 45.87) * mm, "end": v(0.55, 45.87) * mm});
            skLineSegment(sketch, "E9.4.7.4", {"start": v(-2.45, 45.87) * mm, "end": v(-0.95, 48.46) * mm});
            skLineSegment(sketch, "E9.4.7.5", {"start": v(0.55, 45.87) * mm, "end": v(-0.95, 48.46) * mm});
            skLineSegment(sketch, "E9.4.8.0", {"start": v(-3.95, 48.46) * mm, "end": v(-0.95, 48.46) * mm});
            skLineSegment(sketch, "E9.4.8.1", {"start": v(-2.45, 51.06) * mm, "end": v(-3.95, 48.46) * mm});
            skLineSegment(sketch, "E9.4.8.2", {"start": v(-0.95, 48.46) * mm, "end": v(-2.45, 51.06) * mm});
            skLineSegment(sketch, "E9.4.8.3", {"start": v(-2.45, 51.06) * mm, "end": v(0.55, 51.06) * mm});
            skLineSegment(sketch, "E9.4.8.4", {"start": v(-2.45, 51.06) * mm, "end": v(-0.95, 53.66) * mm});
            skLineSegment(sketch, "E9.4.8.5", {"start": v(0.55, 51.06) * mm, "end": v(-0.95, 53.66) * mm});
            skLineSegment(sketch, "E9.4.9.0", {"start": v(-3.95, 53.66) * mm, "end": v(-0.95, 53.66) * mm});
            skLineSegment(sketch, "E9.4.9.1", {"start": v(-2.45, 56.26) * mm, "end": v(-3.95, 53.66) * mm});
            skLineSegment(sketch, "E9.4.9.2", {"start": v(-0.95, 53.66) * mm, "end": v(-2.45, 56.26) * mm});
            skLineSegment(sketch, "E9.4.9.3", {"start": v(-2.45, 56.26) * mm, "end": v(0.55, 56.26) * mm});
            skLineSegment(sketch, "E9.4.9.4", {"start": v(-2.45, 56.26) * mm, "end": v(-0.95, 58.86) * mm});
            skLineSegment(sketch, "E9.4.9.5", {"start": v(0.55, 56.26) * mm, "end": v(-0.95, 58.86) * mm});
            skLineSegment(sketch, "E9.5.0.0", {"start": v(-0.95, 6.9) * mm, "end": v(2.05, 6.9) * mm});
            skLineSegment(sketch, "E9.5.0.1", {"start": v(0.55, 9.5) * mm, "end": v(-0.95, 6.9) * mm});
            skLineSegment(sketch, "E9.5.0.2", {"start": v(2.05, 6.9) * mm, "end": v(0.55, 9.5) * mm});
            skLineSegment(sketch, "E9.5.0.3", {"start": v(0.55, 9.5) * mm, "end": v(3.55, 9.5) * mm});
            skLineSegment(sketch, "E9.5.0.4", {"start": v(0.55, 9.5) * mm, "end": v(2.05, 12.1) * mm});
            skLineSegment(sketch, "E9.5.0.5", {"start": v(3.55, 9.5) * mm, "end": v(2.05, 12.1) * mm});
            skLineSegment(sketch, "E9.5.1.0", {"start": v(-0.95, 12.1) * mm, "end": v(2.05, 12.1) * mm});
            skLineSegment(sketch, "E9.5.1.1", {"start": v(0.55, 14.69) * mm, "end": v(-0.95, 12.1) * mm});
            skLineSegment(sketch, "E9.5.1.2", {"start": v(2.05, 12.1) * mm, "end": v(0.55, 14.69) * mm});
            skLineSegment(sketch, "E9.5.1.3", {"start": v(0.55, 14.69) * mm, "end": v(3.55, 14.69) * mm});
            skLineSegment(sketch, "E9.5.1.4", {"start": v(0.55, 14.69) * mm, "end": v(2.05, 17.29) * mm});
            skLineSegment(sketch, "E9.5.1.5", {"start": v(3.55, 14.69) * mm, "end": v(2.05, 17.29) * mm});
            skLineSegment(sketch, "E9.5.2.0", {"start": v(-0.95, 17.29) * mm, "end": v(2.05, 17.29) * mm});
            skLineSegment(sketch, "E9.5.2.1", {"start": v(0.55, 19.89) * mm, "end": v(-0.95, 17.29) * mm});
            skLineSegment(sketch, "E9.5.2.2", {"start": v(2.05, 17.29) * mm, "end": v(0.55, 19.89) * mm});
            skLineSegment(sketch, "E9.5.2.3", {"start": v(0.55, 19.89) * mm, "end": v(3.55, 19.89) * mm});
            skLineSegment(sketch, "E9.5.2.4", {"start": v(0.55, 19.89) * mm, "end": v(2.05, 22.48) * mm});
            skLineSegment(sketch, "E9.5.2.5", {"start": v(3.55, 19.89) * mm, "end": v(2.05, 22.48) * mm});
            skLineSegment(sketch, "E9.5.3.0", {"start": v(-0.95, 22.48) * mm, "end": v(2.05, 22.48) * mm});
            skLineSegment(sketch, "E9.5.3.1", {"start": v(0.55, 25.08) * mm, "end": v(-0.95, 22.48) * mm});
            skLineSegment(sketch, "E9.5.3.2", {"start": v(2.05, 22.48) * mm, "end": v(0.55, 25.08) * mm});
            skLineSegment(sketch, "E9.5.3.3", {"start": v(0.55, 25.08) * mm, "end": v(3.55, 25.08) * mm});
            skLineSegment(sketch, "E9.5.3.4", {"start": v(0.55, 25.08) * mm, "end": v(2.05, 27.68) * mm});
            skLineSegment(sketch, "E9.5.3.5", {"start": v(3.55, 25.08) * mm, "end": v(2.05, 27.68) * mm});
            skLineSegment(sketch, "E9.5.4.0", {"start": v(-0.95, 27.68) * mm, "end": v(2.05, 27.68) * mm});
            skLineSegment(sketch, "E9.5.4.1", {"start": v(0.55, 30.28) * mm, "end": v(-0.95, 27.68) * mm});
            skLineSegment(sketch, "E9.5.4.2", {"start": v(2.05, 27.68) * mm, "end": v(0.55, 30.28) * mm});
            skLineSegment(sketch, "E9.5.4.3", {"start": v(0.55, 30.28) * mm, "end": v(3.55, 30.28) * mm});
            skLineSegment(sketch, "E9.5.4.4", {"start": v(0.55, 30.28) * mm, "end": v(2.05, 32.88) * mm});
            skLineSegment(sketch, "E9.5.4.5", {"start": v(3.55, 30.28) * mm, "end": v(2.05, 32.88) * mm});
            skLineSegment(sketch, "E9.5.5.0", {"start": v(-0.95, 32.88) * mm, "end": v(2.05, 32.88) * mm});
            skLineSegment(sketch, "E9.5.5.1", {"start": v(0.55, 35.47) * mm, "end": v(-0.95, 32.88) * mm});
            skLineSegment(sketch, "E9.5.5.2", {"start": v(2.05, 32.88) * mm, "end": v(0.55, 35.47) * mm});
            skLineSegment(sketch, "E9.5.5.3", {"start": v(0.55, 35.47) * mm, "end": v(3.55, 35.47) * mm});
            skLineSegment(sketch, "E9.5.5.4", {"start": v(0.55, 35.47) * mm, "end": v(2.05, 38.07) * mm});
            skLineSegment(sketch, "E9.5.5.5", {"start": v(3.55, 35.47) * mm, "end": v(2.05, 38.07) * mm});
            skLineSegment(sketch, "E9.5.6.0", {"start": v(-0.95, 38.07) * mm, "end": v(2.05, 38.07) * mm});
            skLineSegment(sketch, "E9.5.6.1", {"start": v(0.55, 40.67) * mm, "end": v(-0.95, 38.07) * mm});
            skLineSegment(sketch, "E9.5.6.2", {"start": v(2.05, 38.07) * mm, "end": v(0.55, 40.67) * mm});
            skLineSegment(sketch, "E9.5.6.3", {"start": v(0.55, 40.67) * mm, "end": v(3.55, 40.67) * mm});
            skLineSegment(sketch, "E9.5.6.4", {"start": v(0.55, 40.67) * mm, "end": v(2.05, 43.27) * mm});
            skLineSegment(sketch, "E9.5.6.5", {"start": v(3.55, 40.67) * mm, "end": v(2.05, 43.27) * mm});
            skLineSegment(sketch, "E9.5.7.0", {"start": v(-0.95, 43.27) * mm, "end": v(2.05, 43.27) * mm});
            skLineSegment(sketch, "E9.5.7.1", {"start": v(0.55, 45.87) * mm, "end": v(-0.95, 43.27) * mm});
            skLineSegment(sketch, "E9.5.7.2", {"start": v(2.05, 43.27) * mm, "end": v(0.55, 45.87) * mm});
            skLineSegment(sketch, "E9.5.7.3", {"start": v(0.55, 45.87) * mm, "end": v(3.55, 45.87) * mm});
            skLineSegment(sketch, "E9.5.7.4", {"start": v(0.55, 45.87) * mm, "end": v(2.05, 48.46) * mm});
            skLineSegment(sketch, "E9.5.7.5", {"start": v(3.55, 45.87) * mm, "end": v(2.05, 48.46) * mm});
            skLineSegment(sketch, "E9.5.8.0", {"start": v(-0.95, 48.46) * mm, "end": v(2.05, 48.46) * mm});
            skLineSegment(sketch, "E9.5.8.1", {"start": v(0.55, 51.06) * mm, "end": v(-0.95, 48.46) * mm});
            skLineSegment(sketch, "E9.5.8.2", {"start": v(2.05, 48.46) * mm, "end": v(0.55, 51.06) * mm});
            skLineSegment(sketch, "E9.5.8.3", {"start": v(0.55, 51.06) * mm, "end": v(3.55, 51.06) * mm});
            skLineSegment(sketch, "E9.5.8.4", {"start": v(0.55, 51.06) * mm, "end": v(2.05, 53.66) * mm});
            skLineSegment(sketch, "E9.5.8.5", {"start": v(3.55, 51.06) * mm, "end": v(2.05, 53.66) * mm});
            skLineSegment(sketch, "E9.5.9.0", {"start": v(-0.95, 53.66) * mm, "end": v(2.05, 53.66) * mm});
            skLineSegment(sketch, "E9.5.9.1", {"start": v(0.55, 56.26) * mm, "end": v(-0.95, 53.66) * mm});
            skLineSegment(sketch, "E9.5.9.2", {"start": v(2.05, 53.66) * mm, "end": v(0.55, 56.26) * mm});
            skLineSegment(sketch, "E9.5.9.3", {"start": v(0.55, 56.26) * mm, "end": v(3.55, 56.26) * mm});
            skLineSegment(sketch, "E9.5.9.4", {"start": v(0.55, 56.26) * mm, "end": v(2.05, 58.86) * mm});
            skLineSegment(sketch, "E9.5.9.5", {"start": v(3.55, 56.26) * mm, "end": v(2.05, 58.86) * mm});
            skLineSegment(sketch, "E9.6.0.0", {"start": v(2.05, 6.9) * mm, "end": v(5.05, 6.9) * mm});
            skLineSegment(sketch, "E9.6.0.1", {"start": v(3.55, 9.5) * mm, "end": v(2.05, 6.9) * mm});
            skLineSegment(sketch, "E9.6.0.2", {"start": v(5.05, 6.9) * mm, "end": v(3.55, 9.5) * mm});
            skLineSegment(sketch, "E9.6.0.3", {"start": v(3.55, 9.5) * mm, "end": v(6.55, 9.5) * mm});
            skLineSegment(sketch, "E9.6.0.4", {"start": v(3.55, 9.5) * mm, "end": v(5.05, 12.1) * mm});
            skLineSegment(sketch, "E9.6.0.5", {"start": v(6.55, 9.5) * mm, "end": v(5.05, 12.1) * mm});
            skLineSegment(sketch, "E9.6.1.0", {"start": v(2.05, 12.1) * mm, "end": v(5.05, 12.1) * mm});
            skLineSegment(sketch, "E9.6.1.1", {"start": v(3.55, 14.69) * mm, "end": v(2.05, 12.1) * mm});
            skLineSegment(sketch, "E9.6.1.2", {"start": v(5.05, 12.1) * mm, "end": v(3.55, 14.69) * mm});
            skLineSegment(sketch, "E9.6.1.3", {"start": v(3.55, 14.69) * mm, "end": v(6.55, 14.69) * mm});
            skLineSegment(sketch, "E9.6.1.4", {"start": v(3.55, 14.69) * mm, "end": v(5.05, 17.29) * mm});
            skLineSegment(sketch, "E9.6.1.5", {"start": v(6.55, 14.69) * mm, "end": v(5.05, 17.29) * mm});
            skLineSegment(sketch, "E9.6.2.0", {"start": v(2.05, 17.29) * mm, "end": v(5.05, 17.29) * mm});
            skLineSegment(sketch, "E9.6.2.1", {"start": v(3.55, 19.89) * mm, "end": v(2.05, 17.29) * mm});
            skLineSegment(sketch, "E9.6.2.2", {"start": v(5.05, 17.29) * mm, "end": v(3.55, 19.89) * mm});
            skLineSegment(sketch, "E9.6.2.3", {"start": v(3.55, 19.89) * mm, "end": v(6.55, 19.89) * mm});
            skLineSegment(sketch, "E9.6.2.4", {"start": v(3.55, 19.89) * mm, "end": v(5.05, 22.48) * mm});
            skLineSegment(sketch, "E9.6.2.5", {"start": v(6.55, 19.89) * mm, "end": v(5.05, 22.48) * mm});
            skLineSegment(sketch, "E9.6.3.0", {"start": v(2.05, 22.48) * mm, "end": v(5.05, 22.48) * mm});
            skLineSegment(sketch, "E9.6.3.1", {"start": v(3.55, 25.08) * mm, "end": v(2.05, 22.48) * mm});
            skLineSegment(sketch, "E9.6.3.2", {"start": v(5.05, 22.48) * mm, "end": v(3.55, 25.08) * mm});
            skLineSegment(sketch, "E9.6.3.3", {"start": v(3.55, 25.08) * mm, "end": v(6.55, 25.08) * mm});
            skLineSegment(sketch, "E9.6.3.4", {"start": v(3.55, 25.08) * mm, "end": v(5.05, 27.68) * mm});
            skLineSegment(sketch, "E9.6.3.5", {"start": v(6.55, 25.08) * mm, "end": v(5.05, 27.68) * mm});
            skLineSegment(sketch, "E9.6.4.0", {"start": v(2.05, 27.68) * mm, "end": v(5.05, 27.68) * mm});
            skLineSegment(sketch, "E9.6.4.1", {"start": v(3.55, 30.28) * mm, "end": v(2.05, 27.68) * mm});
            skLineSegment(sketch, "E9.6.4.2", {"start": v(5.05, 27.68) * mm, "end": v(3.55, 30.28) * mm});
            skLineSegment(sketch, "E9.6.4.3", {"start": v(3.55, 30.28) * mm, "end": v(6.55, 30.28) * mm});
            skLineSegment(sketch, "E9.6.4.4", {"start": v(3.55, 30.28) * mm, "end": v(5.05, 32.88) * mm});
            skLineSegment(sketch, "E9.6.4.5", {"start": v(6.55, 30.28) * mm, "end": v(5.05, 32.88) * mm});
            skLineSegment(sketch, "E9.6.5.0", {"start": v(2.05, 32.88) * mm, "end": v(5.05, 32.88) * mm});
            skLineSegment(sketch, "E9.6.5.1", {"start": v(3.55, 35.47) * mm, "end": v(2.05, 32.88) * mm});
            skLineSegment(sketch, "E9.6.5.2", {"start": v(5.05, 32.88) * mm, "end": v(3.55, 35.47) * mm});
            skLineSegment(sketch, "E9.6.5.3", {"start": v(3.55, 35.47) * mm, "end": v(6.55, 35.47) * mm});
            skLineSegment(sketch, "E9.6.5.4", {"start": v(3.55, 35.47) * mm, "end": v(5.05, 38.07) * mm});
            skLineSegment(sketch, "E9.6.5.5", {"start": v(6.55, 35.47) * mm, "end": v(5.05, 38.07) * mm});
            skLineSegment(sketch, "E9.6.6.0", {"start": v(2.05, 38.07) * mm, "end": v(5.05, 38.07) * mm});
            skLineSegment(sketch, "E9.6.6.1", {"start": v(3.55, 40.67) * mm, "end": v(2.05, 38.07) * mm});
            skLineSegment(sketch, "E9.6.6.2", {"start": v(5.05, 38.07) * mm, "end": v(3.55, 40.67) * mm});
            skLineSegment(sketch, "E9.6.6.3", {"start": v(3.55, 40.67) * mm, "end": v(6.55, 40.67) * mm});
            skLineSegment(sketch, "E9.6.6.4", {"start": v(3.55, 40.67) * mm, "end": v(5.05, 43.27) * mm});
            skLineSegment(sketch, "E9.6.6.5", {"start": v(6.55, 40.67) * mm, "end": v(5.05, 43.27) * mm});
            skLineSegment(sketch, "E9.6.7.0", {"start": v(2.05, 43.27) * mm, "end": v(5.05, 43.27) * mm});
            skLineSegment(sketch, "E9.6.7.1", {"start": v(3.55, 45.87) * mm, "end": v(2.05, 43.27) * mm});
            skLineSegment(sketch, "E9.6.7.2", {"start": v(5.05, 43.27) * mm, "end": v(3.55, 45.87) * mm});
            skLineSegment(sketch, "E9.6.7.3", {"start": v(3.55, 45.87) * mm, "end": v(6.55, 45.87) * mm});
            skLineSegment(sketch, "E9.6.7.4", {"start": v(3.55, 45.87) * mm, "end": v(5.05, 48.46) * mm});
            skLineSegment(sketch, "E9.6.7.5", {"start": v(6.55, 45.87) * mm, "end": v(5.05, 48.46) * mm});
            skLineSegment(sketch, "E9.6.8.0", {"start": v(2.05, 48.46) * mm, "end": v(5.05, 48.46) * mm});
            skLineSegment(sketch, "E9.6.8.1", {"start": v(3.55, 51.06) * mm, "end": v(2.05, 48.46) * mm});
            skLineSegment(sketch, "E9.6.8.2", {"start": v(5.05, 48.46) * mm, "end": v(3.55, 51.06) * mm});
            skLineSegment(sketch, "E9.6.8.3", {"start": v(3.55, 51.06) * mm, "end": v(6.55, 51.06) * mm});
            skLineSegment(sketch, "E9.6.8.4", {"start": v(3.55, 51.06) * mm, "end": v(5.05, 53.66) * mm});
            skLineSegment(sketch, "E9.6.8.5", {"start": v(6.55, 51.06) * mm, "end": v(5.05, 53.66) * mm});
            skLineSegment(sketch, "E9.6.9.0", {"start": v(2.05, 53.66) * mm, "end": v(5.05, 53.66) * mm});
            skLineSegment(sketch, "E9.6.9.1", {"start": v(3.55, 56.26) * mm, "end": v(2.05, 53.66) * mm});
            skLineSegment(sketch, "E9.6.9.2", {"start": v(5.05, 53.66) * mm, "end": v(3.55, 56.26) * mm});
            skLineSegment(sketch, "E9.6.9.3", {"start": v(3.55, 56.26) * mm, "end": v(6.55, 56.26) * mm});
            skLineSegment(sketch, "E9.6.9.4", {"start": v(3.55, 56.26) * mm, "end": v(5.05, 58.86) * mm});
            skLineSegment(sketch, "E9.6.9.5", {"start": v(6.55, 56.26) * mm, "end": v(5.05, 58.86) * mm});
            skLineSegment(sketch, "E9.7.0.0", {"start": v(5.05, 6.9) * mm, "end": v(8.05, 6.9) * mm});
            skLineSegment(sketch, "E9.7.0.1", {"start": v(6.55, 9.5) * mm, "end": v(5.05, 6.9) * mm});
            skLineSegment(sketch, "E9.7.0.2", {"start": v(8.05, 6.9) * mm, "end": v(6.55, 9.5) * mm});
            skLineSegment(sketch, "E9.7.0.3", {"start": v(6.55, 9.5) * mm, "end": v(9.55, 9.5) * mm});
            skLineSegment(sketch, "E9.7.0.4", {"start": v(6.55, 9.5) * mm, "end": v(8.05, 12.1) * mm});
            skLineSegment(sketch, "E9.7.0.5", {"start": v(9.55, 9.5) * mm, "end": v(8.05, 12.1) * mm});
            skLineSegment(sketch, "E9.7.1.0", {"start": v(5.05, 12.1) * mm, "end": v(8.05, 12.1) * mm});
            skLineSegment(sketch, "E9.7.1.1", {"start": v(6.55, 14.69) * mm, "end": v(5.05, 12.1) * mm});
            skLineSegment(sketch, "E9.7.1.2", {"start": v(8.05, 12.1) * mm, "end": v(6.55, 14.69) * mm});
            skLineSegment(sketch, "E9.7.1.3", {"start": v(6.55, 14.69) * mm, "end": v(9.55, 14.69) * mm});
            skLineSegment(sketch, "E9.7.1.4", {"start": v(6.55, 14.69) * mm, "end": v(8.05, 17.29) * mm});
            skLineSegment(sketch, "E9.7.1.5", {"start": v(9.55, 14.69) * mm, "end": v(8.05, 17.29) * mm});
            skLineSegment(sketch, "E9.7.2.0", {"start": v(5.05, 17.29) * mm, "end": v(8.05, 17.29) * mm});
            skLineSegment(sketch, "E9.7.2.1", {"start": v(6.55, 19.89) * mm, "end": v(5.05, 17.29) * mm});
            skLineSegment(sketch, "E9.7.2.2", {"start": v(8.05, 17.29) * mm, "end": v(6.55, 19.89) * mm});
            skLineSegment(sketch, "E9.7.2.3", {"start": v(6.55, 19.89) * mm, "end": v(9.55, 19.89) * mm});
            skLineSegment(sketch, "E9.7.2.4", {"start": v(6.55, 19.89) * mm, "end": v(8.05, 22.48) * mm});
            skLineSegment(sketch, "E9.7.2.5", {"start": v(9.55, 19.89) * mm, "end": v(8.05, 22.48) * mm});
            skLineSegment(sketch, "E9.7.3.0", {"start": v(5.05, 22.48) * mm, "end": v(8.05, 22.48) * mm});
            skLineSegment(sketch, "E9.7.3.1", {"start": v(6.55, 25.08) * mm, "end": v(5.05, 22.48) * mm});
            skLineSegment(sketch, "E9.7.3.2", {"start": v(8.05, 22.48) * mm, "end": v(6.55, 25.08) * mm});
            skLineSegment(sketch, "E9.7.3.3", {"start": v(6.55, 25.08) * mm, "end": v(9.55, 25.08) * mm});
            skLineSegment(sketch, "E9.7.3.4", {"start": v(6.55, 25.08) * mm, "end": v(8.05, 27.68) * mm});
            skLineSegment(sketch, "E9.7.3.5", {"start": v(9.55, 25.08) * mm, "end": v(8.05, 27.68) * mm});
            skLineSegment(sketch, "E9.7.4.0", {"start": v(5.05, 27.68) * mm, "end": v(8.05, 27.68) * mm});
            skLineSegment(sketch, "E9.7.4.1", {"start": v(6.55, 30.28) * mm, "end": v(5.05, 27.68) * mm});
            skLineSegment(sketch, "E9.7.4.2", {"start": v(8.05, 27.68) * mm, "end": v(6.55, 30.28) * mm});
            skLineSegment(sketch, "E9.7.4.3", {"start": v(6.55, 30.28) * mm, "end": v(9.55, 30.28) * mm});
            skLineSegment(sketch, "E9.7.4.4", {"start": v(6.55, 30.28) * mm, "end": v(8.05, 32.88) * mm});
            skLineSegment(sketch, "E9.7.4.5", {"start": v(9.55, 30.28) * mm, "end": v(8.05, 32.88) * mm});
            skLineSegment(sketch, "E9.7.5.0", {"start": v(5.05, 32.88) * mm, "end": v(8.05, 32.88) * mm});
            skLineSegment(sketch, "E9.7.5.1", {"start": v(6.55, 35.47) * mm, "end": v(5.05, 32.88) * mm});
            skLineSegment(sketch, "E9.7.5.2", {"start": v(8.05, 32.88) * mm, "end": v(6.55, 35.47) * mm});
            skLineSegment(sketch, "E9.7.5.3", {"start": v(6.55, 35.47) * mm, "end": v(9.55, 35.47) * mm});
            skLineSegment(sketch, "E9.7.5.4", {"start": v(6.55, 35.47) * mm, "end": v(8.05, 38.07) * mm});
            skLineSegment(sketch, "E9.7.5.5", {"start": v(9.55, 35.47) * mm, "end": v(8.05, 38.07) * mm});
            skLineSegment(sketch, "E9.7.6.0", {"start": v(5.05, 38.07) * mm, "end": v(8.05, 38.07) * mm});
            skLineSegment(sketch, "E9.7.6.1", {"start": v(6.55, 40.67) * mm, "end": v(5.05, 38.07) * mm});
            skLineSegment(sketch, "E9.7.6.2", {"start": v(8.05, 38.07) * mm, "end": v(6.55, 40.67) * mm});
            skLineSegment(sketch, "E9.7.6.3", {"start": v(6.55, 40.67) * mm, "end": v(9.55, 40.67) * mm});
            skLineSegment(sketch, "E9.7.6.4", {"start": v(6.55, 40.67) * mm, "end": v(8.05, 43.27) * mm});
            skLineSegment(sketch, "E9.7.6.5", {"start": v(9.55, 40.67) * mm, "end": v(8.05, 43.27) * mm});
            skLineSegment(sketch, "E9.7.7.0", {"start": v(5.05, 43.27) * mm, "end": v(8.05, 43.27) * mm});
            skLineSegment(sketch, "E9.7.7.1", {"start": v(6.55, 45.87) * mm, "end": v(5.05, 43.27) * mm});
            skLineSegment(sketch, "E9.7.7.2", {"start": v(8.05, 43.27) * mm, "end": v(6.55, 45.87) * mm});
            skLineSegment(sketch, "E9.7.7.3", {"start": v(6.55, 45.87) * mm, "end": v(9.55, 45.87) * mm});
            skLineSegment(sketch, "E9.7.7.4", {"start": v(6.55, 45.87) * mm, "end": v(8.05, 48.46) * mm});
            skLineSegment(sketch, "E9.7.7.5", {"start": v(9.55, 45.87) * mm, "end": v(8.05, 48.46) * mm});
            skLineSegment(sketch, "E9.7.8.0", {"start": v(5.05, 48.46) * mm, "end": v(8.05, 48.46) * mm});
            skLineSegment(sketch, "E9.7.8.1", {"start": v(6.55, 51.06) * mm, "end": v(5.05, 48.46) * mm});
            skLineSegment(sketch, "E9.7.8.2", {"start": v(8.05, 48.46) * mm, "end": v(6.55, 51.06) * mm});
            skLineSegment(sketch, "E9.7.8.3", {"start": v(6.55, 51.06) * mm, "end": v(9.55, 51.06) * mm});
            skLineSegment(sketch, "E9.7.8.4", {"start": v(6.55, 51.06) * mm, "end": v(8.05, 53.66) * mm});
            skLineSegment(sketch, "E9.7.8.5", {"start": v(9.55, 51.06) * mm, "end": v(8.05, 53.66) * mm});
            skLineSegment(sketch, "E9.7.9.0", {"start": v(5.05, 53.66) * mm, "end": v(8.05, 53.66) * mm});
            skLineSegment(sketch, "E9.7.9.1", {"start": v(6.55, 56.26) * mm, "end": v(5.05, 53.66) * mm});
            skLineSegment(sketch, "E9.7.9.2", {"start": v(8.05, 53.66) * mm, "end": v(6.55, 56.26) * mm});
            skLineSegment(sketch, "E9.7.9.3", {"start": v(6.55, 56.26) * mm, "end": v(9.55, 56.26) * mm});
            skLineSegment(sketch, "E9.7.9.4", {"start": v(6.55, 56.26) * mm, "end": v(8.05, 58.86) * mm});
            skLineSegment(sketch, "E9.7.9.5", {"start": v(9.55, 56.26) * mm, "end": v(8.05, 58.86) * mm});
            skLineSegment(sketch, "E9.8.0.0", {"start": v(8.05, 6.9) * mm, "end": v(11.05, 6.9) * mm});
            skLineSegment(sketch, "E9.8.0.1", {"start": v(9.55, 9.5) * mm, "end": v(8.05, 6.9) * mm});
            skLineSegment(sketch, "E9.8.0.2", {"start": v(11.05, 6.9) * mm, "end": v(9.55, 9.5) * mm});
            skLineSegment(sketch, "E9.8.0.3", {"start": v(9.55, 9.5) * mm, "end": v(12.55, 9.5) * mm});
            skLineSegment(sketch, "E9.8.0.4", {"start": v(9.55, 9.5) * mm, "end": v(11.05, 12.1) * mm});
            skLineSegment(sketch, "E9.8.0.5", {"start": v(12.55, 9.5) * mm, "end": v(11.05, 12.1) * mm});
            skLineSegment(sketch, "E9.8.1.0", {"start": v(8.05, 12.1) * mm, "end": v(11.05, 12.1) * mm});
            skLineSegment(sketch, "E9.8.1.1", {"start": v(9.55, 14.69) * mm, "end": v(8.05, 12.1) * mm});
            skLineSegment(sketch, "E9.8.1.2", {"start": v(11.05, 12.1) * mm, "end": v(9.55, 14.69) * mm});
            skLineSegment(sketch, "E9.8.1.3", {"start": v(9.55, 14.69) * mm, "end": v(12.55, 14.69) * mm});
            skLineSegment(sketch, "E9.8.1.4", {"start": v(9.55, 14.69) * mm, "end": v(11.05, 17.29) * mm});
            skLineSegment(sketch, "E9.8.1.5", {"start": v(12.55, 14.69) * mm, "end": v(11.05, 17.29) * mm});
            skLineSegment(sketch, "E9.8.2.0", {"start": v(8.05, 17.29) * mm, "end": v(11.05, 17.29) * mm});
            skLineSegment(sketch, "E9.8.2.1", {"start": v(9.55, 19.89) * mm, "end": v(8.05, 17.29) * mm});
            skLineSegment(sketch, "E9.8.2.2", {"start": v(11.05, 17.29) * mm, "end": v(9.55, 19.89) * mm});
            skLineSegment(sketch, "E9.8.2.3", {"start": v(9.55, 19.89) * mm, "end": v(12.55, 19.89) * mm});
            skLineSegment(sketch, "E9.8.2.4", {"start": v(9.55, 19.89) * mm, "end": v(11.05, 22.48) * mm});
            skLineSegment(sketch, "E9.8.2.5", {"start": v(12.55, 19.89) * mm, "end": v(11.05, 22.48) * mm});
            skLineSegment(sketch, "E9.8.3.0", {"start": v(8.05, 22.48) * mm, "end": v(11.05, 22.48) * mm});
            skLineSegment(sketch, "E9.8.3.1", {"start": v(9.55, 25.08) * mm, "end": v(8.05, 22.48) * mm});
            skLineSegment(sketch, "E9.8.3.2", {"start": v(11.05, 22.48) * mm, "end": v(9.55, 25.08) * mm});
            skLineSegment(sketch, "E9.8.3.3", {"start": v(9.55, 25.08) * mm, "end": v(12.55, 25.08) * mm});
            skLineSegment(sketch, "E9.8.3.4", {"start": v(9.55, 25.08) * mm, "end": v(11.05, 27.68) * mm});
            skLineSegment(sketch, "E9.8.3.5", {"start": v(12.55, 25.08) * mm, "end": v(11.05, 27.68) * mm});
            skLineSegment(sketch, "E9.8.4.0", {"start": v(8.05, 27.68) * mm, "end": v(11.05, 27.68) * mm});
            skLineSegment(sketch, "E9.8.4.1", {"start": v(9.55, 30.28) * mm, "end": v(8.05, 27.68) * mm});
            skLineSegment(sketch, "E9.8.4.2", {"start": v(11.05, 27.68) * mm, "end": v(9.55, 30.28) * mm});
            skLineSegment(sketch, "E9.8.4.3", {"start": v(9.55, 30.28) * mm, "end": v(12.55, 30.28) * mm});
            skLineSegment(sketch, "E9.8.4.4", {"start": v(9.55, 30.28) * mm, "end": v(11.05, 32.88) * mm});
            skLineSegment(sketch, "E9.8.4.5", {"start": v(12.55, 30.28) * mm, "end": v(11.05, 32.88) * mm});
            skLineSegment(sketch, "E9.8.5.0", {"start": v(8.05, 32.88) * mm, "end": v(11.05, 32.88) * mm});
            skLineSegment(sketch, "E9.8.5.1", {"start": v(9.55, 35.47) * mm, "end": v(8.05, 32.88) * mm});
            skLineSegment(sketch, "E9.8.5.2", {"start": v(11.05, 32.88) * mm, "end": v(9.55, 35.47) * mm});
            skLineSegment(sketch, "E9.8.5.3", {"start": v(9.55, 35.47) * mm, "end": v(12.55, 35.47) * mm});
            skLineSegment(sketch, "E9.8.5.4", {"start": v(9.55, 35.47) * mm, "end": v(11.05, 38.07) * mm});
            skLineSegment(sketch, "E9.8.5.5", {"start": v(12.55, 35.47) * mm, "end": v(11.05, 38.07) * mm});
            skLineSegment(sketch, "E9.8.6.0", {"start": v(8.05, 38.07) * mm, "end": v(11.05, 38.07) * mm});
            skLineSegment(sketch, "E9.8.6.1", {"start": v(9.55, 40.67) * mm, "end": v(8.05, 38.07) * mm});
            skLineSegment(sketch, "E9.8.6.2", {"start": v(11.05, 38.07) * mm, "end": v(9.55, 40.67) * mm});
            skLineSegment(sketch, "E9.8.6.3", {"start": v(9.55, 40.67) * mm, "end": v(12.55, 40.67) * mm});
            skLineSegment(sketch, "E9.8.6.4", {"start": v(9.55, 40.67) * mm, "end": v(11.05, 43.27) * mm});
            skLineSegment(sketch, "E9.8.6.5", {"start": v(12.55, 40.67) * mm, "end": v(11.05, 43.27) * mm});
            skLineSegment(sketch, "E9.8.7.0", {"start": v(8.05, 43.27) * mm, "end": v(11.05, 43.27) * mm});
            skLineSegment(sketch, "E9.8.7.1", {"start": v(9.55, 45.87) * mm, "end": v(8.05, 43.27) * mm});
            skLineSegment(sketch, "E9.8.7.2", {"start": v(11.05, 43.27) * mm, "end": v(9.55, 45.87) * mm});
            skLineSegment(sketch, "E9.8.7.3", {"start": v(9.55, 45.87) * mm, "end": v(12.55, 45.87) * mm});
            skLineSegment(sketch, "E9.8.7.4", {"start": v(9.55, 45.87) * mm, "end": v(11.05, 48.46) * mm});
            skLineSegment(sketch, "E9.8.7.5", {"start": v(12.55, 45.87) * mm, "end": v(11.05, 48.46) * mm});
            skLineSegment(sketch, "E9.8.8.0", {"start": v(8.05, 48.46) * mm, "end": v(11.05, 48.46) * mm});
            skLineSegment(sketch, "E9.8.8.1", {"start": v(9.55, 51.06) * mm, "end": v(8.05, 48.46) * mm});
            skLineSegment(sketch, "E9.8.8.2", {"start": v(11.05, 48.46) * mm, "end": v(9.55, 51.06) * mm});
            skLineSegment(sketch, "E9.8.8.3", {"start": v(9.55, 51.06) * mm, "end": v(12.55, 51.06) * mm});
            skLineSegment(sketch, "E9.8.8.4", {"start": v(9.55, 51.06) * mm, "end": v(11.05, 53.66) * mm});
            skLineSegment(sketch, "E9.8.8.5", {"start": v(12.55, 51.06) * mm, "end": v(11.05, 53.66) * mm});
            skLineSegment(sketch, "E9.8.9.0", {"start": v(8.05, 53.66) * mm, "end": v(11.05, 53.66) * mm});
            skLineSegment(sketch, "E9.8.9.1", {"start": v(9.55, 56.26) * mm, "end": v(8.05, 53.66) * mm});
            skLineSegment(sketch, "E9.8.9.2", {"start": v(11.05, 53.66) * mm, "end": v(9.55, 56.26) * mm});
            skLineSegment(sketch, "E9.8.9.3", {"start": v(9.55, 56.26) * mm, "end": v(12.55, 56.26) * mm});
            skLineSegment(sketch, "E9.8.9.4", {"start": v(9.55, 56.26) * mm, "end": v(11.05, 58.86) * mm});
            skLineSegment(sketch, "E9.8.9.5", {"start": v(12.55, 56.26) * mm, "end": v(11.05, 58.86) * mm});
            skLineSegment(sketch, "E9.9.0.0", {"start": v(11.05, 6.9) * mm, "end": v(14.05, 6.9) * mm});
            skLineSegment(sketch, "E9.9.0.1", {"start": v(12.55, 9.5) * mm, "end": v(11.05, 6.9) * mm});
            skLineSegment(sketch, "E9.9.0.2", {"start": v(14.05, 6.9) * mm, "end": v(12.55, 9.5) * mm});
            skLineSegment(sketch, "E9.9.0.3", {"start": v(12.55, 9.5) * mm, "end": v(15.55, 9.5) * mm});
            skLineSegment(sketch, "E9.9.0.4", {"start": v(12.55, 9.5) * mm, "end": v(14.05, 12.1) * mm});
            skLineSegment(sketch, "E9.9.0.5", {"start": v(15.55, 9.5) * mm, "end": v(14.05, 12.1) * mm});
            skLineSegment(sketch, "E9.9.1.0", {"start": v(11.05, 12.1) * mm, "end": v(14.05, 12.1) * mm});
            skLineSegment(sketch, "E9.9.1.1", {"start": v(12.55, 14.69) * mm, "end": v(11.05, 12.1) * mm});
            skLineSegment(sketch, "E9.9.1.2", {"start": v(14.05, 12.1) * mm, "end": v(12.55, 14.69) * mm});
            skLineSegment(sketch, "E9.9.1.3", {"start": v(12.55, 14.69) * mm, "end": v(15.55, 14.69) * mm});
            skLineSegment(sketch, "E9.9.1.4", {"start": v(12.55, 14.69) * mm, "end": v(14.05, 17.29) * mm});
            skLineSegment(sketch, "E9.9.1.5", {"start": v(15.55, 14.69) * mm, "end": v(14.05, 17.29) * mm});
            skLineSegment(sketch, "E9.9.2.0", {"start": v(11.05, 17.29) * mm, "end": v(14.05, 17.29) * mm});
            skLineSegment(sketch, "E9.9.2.1", {"start": v(12.55, 19.89) * mm, "end": v(11.05, 17.29) * mm});
            skLineSegment(sketch, "E9.9.2.2", {"start": v(14.05, 17.29) * mm, "end": v(12.55, 19.89) * mm});
            skLineSegment(sketch, "E9.9.2.3", {"start": v(12.55, 19.89) * mm, "end": v(15.55, 19.89) * mm});
            skLineSegment(sketch, "E9.9.2.4", {"start": v(12.55, 19.89) * mm, "end": v(14.05, 22.48) * mm});
            skLineSegment(sketch, "E9.9.2.5", {"start": v(15.55, 19.89) * mm, "end": v(14.05, 22.48) * mm});
            skLineSegment(sketch, "E9.9.3.0", {"start": v(11.05, 22.48) * mm, "end": v(14.05, 22.48) * mm});
            skLineSegment(sketch, "E9.9.3.1", {"start": v(12.55, 25.08) * mm, "end": v(11.05, 22.48) * mm});
            skLineSegment(sketch, "E9.9.3.2", {"start": v(14.05, 22.48) * mm, "end": v(12.55, 25.08) * mm});
            skLineSegment(sketch, "E9.9.3.3", {"start": v(12.55, 25.08) * mm, "end": v(15.55, 25.08) * mm});
            skLineSegment(sketch, "E9.9.3.4", {"start": v(12.55, 25.08) * mm, "end": v(14.05, 27.68) * mm});
            skLineSegment(sketch, "E9.9.3.5", {"start": v(15.55, 25.08) * mm, "end": v(14.05, 27.68) * mm});
            skLineSegment(sketch, "E9.9.4.0", {"start": v(11.05, 27.68) * mm, "end": v(14.05, 27.68) * mm});
            skLineSegment(sketch, "E9.9.4.1", {"start": v(12.55, 30.28) * mm, "end": v(11.05, 27.68) * mm});
            skLineSegment(sketch, "E9.9.4.2", {"start": v(14.05, 27.68) * mm, "end": v(12.55, 30.28) * mm});
            skLineSegment(sketch, "E9.9.4.3", {"start": v(12.55, 30.28) * mm, "end": v(15.55, 30.28) * mm});
            skLineSegment(sketch, "E9.9.4.4", {"start": v(12.55, 30.28) * mm, "end": v(14.05, 32.88) * mm});
            skLineSegment(sketch, "E9.9.4.5", {"start": v(15.55, 30.28) * mm, "end": v(14.05, 32.88) * mm});
            skLineSegment(sketch, "E9.9.5.0", {"start": v(11.05, 32.88) * mm, "end": v(14.05, 32.88) * mm});
            skLineSegment(sketch, "E9.9.5.1", {"start": v(12.55, 35.47) * mm, "end": v(11.05, 32.88) * mm});
            skLineSegment(sketch, "E9.9.5.2", {"start": v(14.05, 32.88) * mm, "end": v(12.55, 35.47) * mm});
            skLineSegment(sketch, "E9.9.5.3", {"start": v(12.55, 35.47) * mm, "end": v(15.55, 35.47) * mm});
            skLineSegment(sketch, "E9.9.5.4", {"start": v(12.55, 35.47) * mm, "end": v(14.05, 38.07) * mm});
            skLineSegment(sketch, "E9.9.5.5", {"start": v(15.55, 35.47) * mm, "end": v(14.05, 38.07) * mm});
            skLineSegment(sketch, "E9.9.6.0", {"start": v(11.05, 38.07) * mm, "end": v(14.05, 38.07) * mm});
            skLineSegment(sketch, "E9.9.6.1", {"start": v(12.55, 40.67) * mm, "end": v(11.05, 38.07) * mm});
            skLineSegment(sketch, "E9.9.6.2", {"start": v(14.05, 38.07) * mm, "end": v(12.55, 40.67) * mm});
            skLineSegment(sketch, "E9.9.6.3", {"start": v(12.55, 40.67) * mm, "end": v(15.55, 40.67) * mm});
            skLineSegment(sketch, "E9.9.6.4", {"start": v(12.55, 40.67) * mm, "end": v(14.05, 43.27) * mm});
            skLineSegment(sketch, "E9.9.6.5", {"start": v(15.55, 40.67) * mm, "end": v(14.05, 43.27) * mm});
            skLineSegment(sketch, "E9.9.7.0", {"start": v(11.05, 43.27) * mm, "end": v(14.05, 43.27) * mm});
            skLineSegment(sketch, "E9.9.7.1", {"start": v(12.55, 45.87) * mm, "end": v(11.05, 43.27) * mm});
            skLineSegment(sketch, "E9.9.7.2", {"start": v(14.05, 43.27) * mm, "end": v(12.55, 45.87) * mm});
            skLineSegment(sketch, "E9.9.7.3", {"start": v(12.55, 45.87) * mm, "end": v(15.55, 45.87) * mm});
            skLineSegment(sketch, "E9.9.7.4", {"start": v(12.55, 45.87) * mm, "end": v(14.05, 48.46) * mm});
            skLineSegment(sketch, "E9.9.7.5", {"start": v(15.55, 45.87) * mm, "end": v(14.05, 48.46) * mm});
            skLineSegment(sketch, "E9.9.8.0", {"start": v(11.05, 48.46) * mm, "end": v(14.05, 48.46) * mm});
            skLineSegment(sketch, "E9.9.8.1", {"start": v(12.55, 51.06) * mm, "end": v(11.05, 48.46) * mm});
            skLineSegment(sketch, "E9.9.8.2", {"start": v(14.05, 48.46) * mm, "end": v(12.55, 51.06) * mm});
            skLineSegment(sketch, "E9.9.8.3", {"start": v(12.55, 51.06) * mm, "end": v(15.55, 51.06) * mm});
            skLineSegment(sketch, "E9.9.8.4", {"start": v(12.55, 51.06) * mm, "end": v(14.05, 53.66) * mm});
            skLineSegment(sketch, "E9.9.8.5", {"start": v(15.55, 51.06) * mm, "end": v(14.05, 53.66) * mm});
            skLineSegment(sketch, "E9.9.9.0", {"start": v(11.05, 53.66) * mm, "end": v(14.05, 53.66) * mm});
            skLineSegment(sketch, "E9.9.9.1", {"start": v(12.55, 56.26) * mm, "end": v(11.05, 53.66) * mm});
            skLineSegment(sketch, "E9.9.9.2", {"start": v(14.05, 53.66) * mm, "end": v(12.55, 56.26) * mm});
            skLineSegment(sketch, "E9.9.9.3", {"start": v(12.55, 56.26) * mm, "end": v(15.55, 56.26) * mm});
            skLineSegment(sketch, "E9.9.9.4", {"start": v(12.55, 56.26) * mm, "end": v(14.05, 58.86) * mm});
            skLineSegment(sketch, "E9.9.9.5", {"start": v(15.55, 56.26) * mm, "end": v(14.05, 58.86) * mm});
            skLineSegment(sketch, "E9.10.0.0", {"start": v(14.05, 6.9) * mm, "end": v(17.05, 6.9) * mm});
            skLineSegment(sketch, "E9.10.0.1", {"start": v(15.55, 9.5) * mm, "end": v(14.05, 6.9) * mm});
            skLineSegment(sketch, "E9.10.0.2", {"start": v(17.05, 6.9) * mm, "end": v(15.55, 9.5) * mm});
            skLineSegment(sketch, "E9.10.0.3", {"start": v(15.55, 9.5) * mm, "end": v(18.55, 9.5) * mm});
            skLineSegment(sketch, "E9.10.0.4", {"start": v(15.55, 9.5) * mm, "end": v(17.05, 12.1) * mm});
            skLineSegment(sketch, "E9.10.0.5", {"start": v(18.55, 9.5) * mm, "end": v(17.05, 12.1) * mm});
            skLineSegment(sketch, "E9.10.1.0", {"start": v(14.05, 12.1) * mm, "end": v(17.05, 12.1) * mm});
            skLineSegment(sketch, "E9.10.1.1", {"start": v(15.55, 14.69) * mm, "end": v(14.05, 12.1) * mm});
            skLineSegment(sketch, "E9.10.1.2", {"start": v(17.05, 12.1) * mm, "end": v(15.55, 14.69) * mm});
            skLineSegment(sketch, "E9.10.1.3", {"start": v(15.55, 14.69) * mm, "end": v(18.55, 14.69) * mm});
            skLineSegment(sketch, "E9.10.1.4", {"start": v(15.55, 14.69) * mm, "end": v(17.05, 17.29) * mm});
            skLineSegment(sketch, "E9.10.1.5", {"start": v(18.55, 14.69) * mm, "end": v(17.05, 17.29) * mm});
            skLineSegment(sketch, "E9.10.2.0", {"start": v(14.05, 17.29) * mm, "end": v(17.05, 17.29) * mm});
            skLineSegment(sketch, "E9.10.2.1", {"start": v(15.55, 19.89) * mm, "end": v(14.05, 17.29) * mm});
            skLineSegment(sketch, "E9.10.2.2", {"start": v(17.05, 17.29) * mm, "end": v(15.55, 19.89) * mm});
            skLineSegment(sketch, "E9.10.2.3", {"start": v(15.55, 19.89) * mm, "end": v(18.55, 19.89) * mm});
            skLineSegment(sketch, "E9.10.2.4", {"start": v(15.55, 19.89) * mm, "end": v(17.05, 22.48) * mm});
            skLineSegment(sketch, "E9.10.2.5", {"start": v(18.55, 19.89) * mm, "end": v(17.05, 22.48) * mm});
            skLineSegment(sketch, "E9.10.3.0", {"start": v(14.05, 22.48) * mm, "end": v(17.05, 22.48) * mm});
            skLineSegment(sketch, "E9.10.3.1", {"start": v(15.55, 25.08) * mm, "end": v(14.05, 22.48) * mm});
            skLineSegment(sketch, "E9.10.3.2", {"start": v(17.05, 22.48) * mm, "end": v(15.55, 25.08) * mm});
            skLineSegment(sketch, "E9.10.3.3", {"start": v(15.55, 25.08) * mm, "end": v(18.55, 25.08) * mm});
            skLineSegment(sketch, "E9.10.3.4", {"start": v(15.55, 25.08) * mm, "end": v(17.05, 27.68) * mm});
            skLineSegment(sketch, "E9.10.3.5", {"start": v(18.55, 25.08) * mm, "end": v(17.05, 27.68) * mm});
            skLineSegment(sketch, "E9.10.4.0", {"start": v(14.05, 27.68) * mm, "end": v(17.05, 27.68) * mm});
            skLineSegment(sketch, "E9.10.4.1", {"start": v(15.55, 30.28) * mm, "end": v(14.05, 27.68) * mm});
            skLineSegment(sketch, "E9.10.4.2", {"start": v(17.05, 27.68) * mm, "end": v(15.55, 30.28) * mm});
            skLineSegment(sketch, "E9.10.4.3", {"start": v(15.55, 30.28) * mm, "end": v(18.55, 30.28) * mm});
            skLineSegment(sketch, "E9.10.4.4", {"start": v(15.55, 30.28) * mm, "end": v(17.05, 32.88) * mm});
            skLineSegment(sketch, "E9.10.4.5", {"start": v(18.55, 30.28) * mm, "end": v(17.05, 32.88) * mm});
            skLineSegment(sketch, "E9.10.5.0", {"start": v(14.05, 32.88) * mm, "end": v(17.05, 32.88) * mm});
            skLineSegment(sketch, "E9.10.5.1", {"start": v(15.55, 35.47) * mm, "end": v(14.05, 32.88) * mm});
            skLineSegment(sketch, "E9.10.5.2", {"start": v(17.05, 32.88) * mm, "end": v(15.55, 35.47) * mm});
            skLineSegment(sketch, "E9.10.5.3", {"start": v(15.55, 35.47) * mm, "end": v(18.55, 35.47) * mm});
            skLineSegment(sketch, "E9.10.5.4", {"start": v(15.55, 35.47) * mm, "end": v(17.05, 38.07) * mm});
            skLineSegment(sketch, "E9.10.5.5", {"start": v(18.55, 35.47) * mm, "end": v(17.05, 38.07) * mm});
            skLineSegment(sketch, "E9.10.6.0", {"start": v(14.05, 38.07) * mm, "end": v(17.05, 38.07) * mm});
            skLineSegment(sketch, "E9.10.6.1", {"start": v(15.55, 40.67) * mm, "end": v(14.05, 38.07) * mm});
            skLineSegment(sketch, "E9.10.6.2", {"start": v(17.05, 38.07) * mm, "end": v(15.55, 40.67) * mm});
            skLineSegment(sketch, "E9.10.6.3", {"start": v(15.55, 40.67) * mm, "end": v(18.55, 40.67) * mm});
            skLineSegment(sketch, "E9.10.6.4", {"start": v(15.55, 40.67) * mm, "end": v(17.05, 43.27) * mm});
            skLineSegment(sketch, "E9.10.6.5", {"start": v(18.55, 40.67) * mm, "end": v(17.05, 43.27) * mm});
            skLineSegment(sketch, "E9.10.7.0", {"start": v(14.05, 43.27) * mm, "end": v(17.05, 43.27) * mm});
            skLineSegment(sketch, "E9.10.7.1", {"start": v(15.55, 45.87) * mm, "end": v(14.05, 43.27) * mm});
            skLineSegment(sketch, "E9.10.7.2", {"start": v(17.05, 43.27) * mm, "end": v(15.55, 45.87) * mm});
            skLineSegment(sketch, "E9.10.7.3", {"start": v(15.55, 45.87) * mm, "end": v(18.55, 45.87) * mm});
            skLineSegment(sketch, "E9.10.7.4", {"start": v(15.55, 45.87) * mm, "end": v(17.05, 48.46) * mm});
            skLineSegment(sketch, "E9.10.7.5", {"start": v(18.55, 45.87) * mm, "end": v(17.05, 48.46) * mm});
            skLineSegment(sketch, "E9.10.8.0", {"start": v(14.05, 48.46) * mm, "end": v(17.05, 48.46) * mm});
            skLineSegment(sketch, "E9.10.8.1", {"start": v(15.55, 51.06) * mm, "end": v(14.05, 48.46) * mm});
            skLineSegment(sketch, "E9.10.8.2", {"start": v(17.05, 48.46) * mm, "end": v(15.55, 51.06) * mm});
            skLineSegment(sketch, "E9.10.8.3", {"start": v(15.55, 51.06) * mm, "end": v(18.55, 51.06) * mm});
            skLineSegment(sketch, "E9.10.8.4", {"start": v(15.55, 51.06) * mm, "end": v(17.05, 53.66) * mm});
            skLineSegment(sketch, "E9.10.8.5", {"start": v(18.55, 51.06) * mm, "end": v(17.05, 53.66) * mm});
            skLineSegment(sketch, "E9.10.9.0", {"start": v(14.05, 53.66) * mm, "end": v(17.05, 53.66) * mm});
            skLineSegment(sketch, "E9.10.9.1", {"start": v(15.55, 56.26) * mm, "end": v(14.05, 53.66) * mm});
            skLineSegment(sketch, "E9.10.9.2", {"start": v(17.05, 53.66) * mm, "end": v(15.55, 56.26) * mm});
            skLineSegment(sketch, "E9.10.9.3", {"start": v(15.55, 56.26) * mm, "end": v(18.55, 56.26) * mm});
            skLineSegment(sketch, "E9.10.9.4", {"start": v(15.55, 56.26) * mm, "end": v(17.05, 58.86) * mm});
            skLineSegment(sketch, "E9.10.9.5", {"start": v(18.55, 56.26) * mm, "end": v(17.05, 58.86) * mm});
            skLineSegment(sketch, "E9.11.0.0", {"start": v(17.05, 6.9) * mm, "end": v(20.05, 6.9) * mm});
            skLineSegment(sketch, "E9.11.0.1", {"start": v(18.55, 9.5) * mm, "end": v(17.05, 6.9) * mm});
            skLineSegment(sketch, "E9.11.0.2", {"start": v(20.05, 6.9) * mm, "end": v(18.55, 9.5) * mm});
            skLineSegment(sketch, "E9.11.0.3", {"start": v(18.55, 9.5) * mm, "end": v(21.55, 9.5) * mm});
            skLineSegment(sketch, "E9.11.0.4", {"start": v(18.55, 9.5) * mm, "end": v(20.05, 12.1) * mm});
            skLineSegment(sketch, "E9.11.0.5", {"start": v(21.55, 9.5) * mm, "end": v(20.05, 12.1) * mm});
            skLineSegment(sketch, "E9.11.1.0", {"start": v(17.05, 12.1) * mm, "end": v(20.05, 12.1) * mm});
            skLineSegment(sketch, "E9.11.1.1", {"start": v(18.55, 14.69) * mm, "end": v(17.05, 12.1) * mm});
            skLineSegment(sketch, "E9.11.1.2", {"start": v(20.05, 12.1) * mm, "end": v(18.55, 14.69) * mm});
            skLineSegment(sketch, "E9.11.1.3", {"start": v(18.55, 14.69) * mm, "end": v(21.55, 14.69) * mm});
            skLineSegment(sketch, "E9.11.1.4", {"start": v(18.55, 14.69) * mm, "end": v(20.05, 17.29) * mm});
            skLineSegment(sketch, "E9.11.1.5", {"start": v(21.55, 14.69) * mm, "end": v(20.05, 17.29) * mm});
            skLineSegment(sketch, "E9.11.2.0", {"start": v(17.05, 17.29) * mm, "end": v(20.05, 17.29) * mm});
            skLineSegment(sketch, "E9.11.2.1", {"start": v(18.55, 19.89) * mm, "end": v(17.05, 17.29) * mm});
            skLineSegment(sketch, "E9.11.2.2", {"start": v(20.05, 17.29) * mm, "end": v(18.55, 19.89) * mm});
            skLineSegment(sketch, "E9.11.2.3", {"start": v(18.55, 19.89) * mm, "end": v(21.55, 19.89) * mm});
            skLineSegment(sketch, "E9.11.2.4", {"start": v(18.55, 19.89) * mm, "end": v(20.05, 22.48) * mm});
            skLineSegment(sketch, "E9.11.2.5", {"start": v(21.55, 19.89) * mm, "end": v(20.05, 22.48) * mm});
            skLineSegment(sketch, "E9.11.3.0", {"start": v(17.05, 22.48) * mm, "end": v(20.05, 22.48) * mm});
            skLineSegment(sketch, "E9.11.3.1", {"start": v(18.55, 25.08) * mm, "end": v(17.05, 22.48) * mm});
            skLineSegment(sketch, "E9.11.3.2", {"start": v(20.05, 22.48) * mm, "end": v(18.55, 25.08) * mm});
            skLineSegment(sketch, "E9.11.3.3", {"start": v(18.55, 25.08) * mm, "end": v(21.55, 25.08) * mm});
            skLineSegment(sketch, "E9.11.3.4", {"start": v(18.55, 25.08) * mm, "end": v(20.05, 27.68) * mm});
            skLineSegment(sketch, "E9.11.3.5", {"start": v(21.55, 25.08) * mm, "end": v(20.05, 27.68) * mm});
            skLineSegment(sketch, "E9.11.4.0", {"start": v(17.05, 27.68) * mm, "end": v(20.05, 27.68) * mm});
            skLineSegment(sketch, "E9.11.4.1", {"start": v(18.55, 30.28) * mm, "end": v(17.05, 27.68) * mm});
            skLineSegment(sketch, "E9.11.4.2", {"start": v(20.05, 27.68) * mm, "end": v(18.55, 30.28) * mm});
            skLineSegment(sketch, "E9.11.4.3", {"start": v(18.55, 30.28) * mm, "end": v(21.55, 30.28) * mm});
            skLineSegment(sketch, "E9.11.4.4", {"start": v(18.55, 30.28) * mm, "end": v(20.05, 32.88) * mm});
            skLineSegment(sketch, "E9.11.4.5", {"start": v(21.55, 30.28) * mm, "end": v(20.05, 32.88) * mm});
            skLineSegment(sketch, "E9.11.5.0", {"start": v(17.05, 32.88) * mm, "end": v(20.05, 32.88) * mm});
            skLineSegment(sketch, "E9.11.5.1", {"start": v(18.55, 35.47) * mm, "end": v(17.05, 32.88) * mm});
            skLineSegment(sketch, "E9.11.5.2", {"start": v(20.05, 32.88) * mm, "end": v(18.55, 35.47) * mm});
            skLineSegment(sketch, "E9.11.5.3", {"start": v(18.55, 35.47) * mm, "end": v(21.55, 35.47) * mm});
            skLineSegment(sketch, "E9.11.5.4", {"start": v(18.55, 35.47) * mm, "end": v(20.05, 38.07) * mm});
            skLineSegment(sketch, "E9.11.5.5", {"start": v(21.55, 35.47) * mm, "end": v(20.05, 38.07) * mm});
            skLineSegment(sketch, "E9.11.6.0", {"start": v(17.05, 38.07) * mm, "end": v(20.05, 38.07) * mm});
            skLineSegment(sketch, "E9.11.6.1", {"start": v(18.55, 40.67) * mm, "end": v(17.05, 38.07) * mm});
            skLineSegment(sketch, "E9.11.6.2", {"start": v(20.05, 38.07) * mm, "end": v(18.55, 40.67) * mm});
            skLineSegment(sketch, "E9.11.6.3", {"start": v(18.55, 40.67) * mm, "end": v(21.55, 40.67) * mm});
            skLineSegment(sketch, "E9.11.6.4", {"start": v(18.55, 40.67) * mm, "end": v(20.05, 43.27) * mm});
            skLineSegment(sketch, "E9.11.6.5", {"start": v(21.55, 40.67) * mm, "end": v(20.05, 43.27) * mm});
            skLineSegment(sketch, "E9.11.7.0", {"start": v(17.05, 43.27) * mm, "end": v(20.05, 43.27) * mm});
            skLineSegment(sketch, "E9.11.7.1", {"start": v(18.55, 45.87) * mm, "end": v(17.05, 43.27) * mm});
            skLineSegment(sketch, "E9.11.7.2", {"start": v(20.05, 43.27) * mm, "end": v(18.55, 45.87) * mm});
            skLineSegment(sketch, "E9.11.7.3", {"start": v(18.55, 45.87) * mm, "end": v(21.55, 45.87) * mm});
            skLineSegment(sketch, "E9.11.7.4", {"start": v(18.55, 45.87) * mm, "end": v(20.05, 48.46) * mm});
            skLineSegment(sketch, "E9.11.7.5", {"start": v(21.55, 45.87) * mm, "end": v(20.05, 48.46) * mm});
            skLineSegment(sketch, "E9.11.8.0", {"start": v(17.05, 48.46) * mm, "end": v(20.05, 48.46) * mm});
            skLineSegment(sketch, "E9.11.8.1", {"start": v(18.55, 51.06) * mm, "end": v(17.05, 48.46) * mm});
            skLineSegment(sketch, "E9.11.8.2", {"start": v(20.05, 48.46) * mm, "end": v(18.55, 51.06) * mm});
            skLineSegment(sketch, "E9.11.8.3", {"start": v(18.55, 51.06) * mm, "end": v(21.55, 51.06) * mm});
            skLineSegment(sketch, "E9.11.8.4", {"start": v(18.55, 51.06) * mm, "end": v(20.05, 53.66) * mm});
            skLineSegment(sketch, "E9.11.8.5", {"start": v(21.55, 51.06) * mm, "end": v(20.05, 53.66) * mm});
            skLineSegment(sketch, "E9.11.9.0", {"start": v(17.05, 53.66) * mm, "end": v(20.05, 53.66) * mm});
            skLineSegment(sketch, "E9.11.9.1", {"start": v(18.55, 56.26) * mm, "end": v(17.05, 53.66) * mm});
            skLineSegment(sketch, "E9.11.9.2", {"start": v(20.05, 53.66) * mm, "end": v(18.55, 56.26) * mm});
            skLineSegment(sketch, "E9.11.9.3", {"start": v(18.55, 56.26) * mm, "end": v(21.55, 56.26) * mm});
            skLineSegment(sketch, "E9.11.9.4", {"start": v(18.55, 56.26) * mm, "end": v(20.05, 58.86) * mm});
            skLineSegment(sketch, "E9.11.9.5", {"start": v(21.55, 56.26) * mm, "end": v(20.05, 58.86) * mm});
            skLineSegment(sketch, "E9.12.0.0", {"start": v(20.05, 6.9) * mm, "end": v(23.05, 6.9) * mm});
            skLineSegment(sketch, "E9.12.0.1", {"start": v(21.55, 9.5) * mm, "end": v(20.05, 6.9) * mm});
            skLineSegment(sketch, "E9.12.0.2", {"start": v(23.05, 6.9) * mm, "end": v(21.55, 9.5) * mm});
            skLineSegment(sketch, "E9.12.0.3", {"start": v(21.55, 9.5) * mm, "end": v(24.55, 9.5) * mm});
            skLineSegment(sketch, "E9.12.0.4", {"start": v(21.55, 9.5) * mm, "end": v(23.05, 12.1) * mm});
            skLineSegment(sketch, "E9.12.0.5", {"start": v(24.55, 9.5) * mm, "end": v(23.05, 12.1) * mm});
            skLineSegment(sketch, "E9.12.1.0", {"start": v(20.05, 12.1) * mm, "end": v(23.05, 12.1) * mm});
            skLineSegment(sketch, "E9.12.1.1", {"start": v(21.55, 14.69) * mm, "end": v(20.05, 12.1) * mm});
            skLineSegment(sketch, "E9.12.1.2", {"start": v(23.05, 12.1) * mm, "end": v(21.55, 14.69) * mm});
            skLineSegment(sketch, "E9.12.1.3", {"start": v(21.55, 14.69) * mm, "end": v(24.55, 14.69) * mm});
            skLineSegment(sketch, "E9.12.1.4", {"start": v(21.55, 14.69) * mm, "end": v(23.05, 17.29) * mm});
            skLineSegment(sketch, "E9.12.1.5", {"start": v(24.55, 14.69) * mm, "end": v(23.05, 17.29) * mm});
            skLineSegment(sketch, "E9.12.2.0", {"start": v(20.05, 17.29) * mm, "end": v(23.05, 17.29) * mm});
            skLineSegment(sketch, "E9.12.2.1", {"start": v(21.55, 19.89) * mm, "end": v(20.05, 17.29) * mm});
            skLineSegment(sketch, "E9.12.2.2", {"start": v(23.05, 17.29) * mm, "end": v(21.55, 19.89) * mm});
            skLineSegment(sketch, "E9.12.2.3", {"start": v(21.55, 19.89) * mm, "end": v(24.55, 19.89) * mm});
            skLineSegment(sketch, "E9.12.2.4", {"start": v(21.55, 19.89) * mm, "end": v(23.05, 22.48) * mm});
            skLineSegment(sketch, "E9.12.2.5", {"start": v(24.55, 19.89) * mm, "end": v(23.05, 22.48) * mm});
            skLineSegment(sketch, "E9.12.3.0", {"start": v(20.05, 22.48) * mm, "end": v(23.05, 22.48) * mm});
            skLineSegment(sketch, "E9.12.3.1", {"start": v(21.55, 25.08) * mm, "end": v(20.05, 22.48) * mm});
            skLineSegment(sketch, "E9.12.3.2", {"start": v(23.05, 22.48) * mm, "end": v(21.55, 25.08) * mm});
            skLineSegment(sketch, "E9.12.3.3", {"start": v(21.55, 25.08) * mm, "end": v(24.55, 25.08) * mm});
            skLineSegment(sketch, "E9.12.3.4", {"start": v(21.55, 25.08) * mm, "end": v(23.05, 27.68) * mm});
            skLineSegment(sketch, "E9.12.3.5", {"start": v(24.55, 25.08) * mm, "end": v(23.05, 27.68) * mm});
            skLineSegment(sketch, "E9.12.4.0", {"start": v(20.05, 27.68) * mm, "end": v(23.05, 27.68) * mm});
            skLineSegment(sketch, "E9.12.4.1", {"start": v(21.55, 30.28) * mm, "end": v(20.05, 27.68) * mm});
            skLineSegment(sketch, "E9.12.4.2", {"start": v(23.05, 27.68) * mm, "end": v(21.55, 30.28) * mm});
            skLineSegment(sketch, "E9.12.4.3", {"start": v(21.55, 30.28) * mm, "end": v(24.55, 30.28) * mm});
            skLineSegment(sketch, "E9.12.4.4", {"start": v(21.55, 30.28) * mm, "end": v(23.05, 32.88) * mm});
            skLineSegment(sketch, "E9.12.4.5", {"start": v(24.55, 30.28) * mm, "end": v(23.05, 32.88) * mm});
            skLineSegment(sketch, "E9.12.5.0", {"start": v(20.05, 32.88) * mm, "end": v(23.05, 32.88) * mm});
            skLineSegment(sketch, "E9.12.5.1", {"start": v(21.55, 35.47) * mm, "end": v(20.05, 32.88) * mm});
            skLineSegment(sketch, "E9.12.5.2", {"start": v(23.05, 32.88) * mm, "end": v(21.55, 35.47) * mm});
            skLineSegment(sketch, "E9.12.5.3", {"start": v(21.55, 35.47) * mm, "end": v(24.55, 35.47) * mm});
            skLineSegment(sketch, "E9.12.5.4", {"start": v(21.55, 35.47) * mm, "end": v(23.05, 38.07) * mm});
            skLineSegment(sketch, "E9.12.5.5", {"start": v(24.55, 35.47) * mm, "end": v(23.05, 38.07) * mm});
            skLineSegment(sketch, "E9.12.6.0", {"start": v(20.05, 38.07) * mm, "end": v(23.05, 38.07) * mm});
            skLineSegment(sketch, "E9.12.6.1", {"start": v(21.55, 40.67) * mm, "end": v(20.05, 38.07) * mm});
            skLineSegment(sketch, "E9.12.6.2", {"start": v(23.05, 38.07) * mm, "end": v(21.55, 40.67) * mm});
            skLineSegment(sketch, "E9.12.6.3", {"start": v(21.55, 40.67) * mm, "end": v(24.55, 40.67) * mm});
            skLineSegment(sketch, "E9.12.6.4", {"start": v(21.55, 40.67) * mm, "end": v(23.05, 43.27) * mm});
            skLineSegment(sketch, "E9.12.6.5", {"start": v(24.55, 40.67) * mm, "end": v(23.05, 43.27) * mm});
            skLineSegment(sketch, "E9.12.7.0", {"start": v(20.05, 43.27) * mm, "end": v(23.05, 43.27) * mm});
            skLineSegment(sketch, "E9.12.7.1", {"start": v(21.55, 45.87) * mm, "end": v(20.05, 43.27) * mm});
            skLineSegment(sketch, "E9.12.7.2", {"start": v(23.05, 43.27) * mm, "end": v(21.55, 45.87) * mm});
            skLineSegment(sketch, "E9.12.7.3", {"start": v(21.55, 45.87) * mm, "end": v(24.55, 45.87) * mm});
            skLineSegment(sketch, "E9.12.7.4", {"start": v(21.55, 45.87) * mm, "end": v(23.05, 48.46) * mm});
            skLineSegment(sketch, "E9.12.7.5", {"start": v(24.55, 45.87) * mm, "end": v(23.05, 48.46) * mm});
            skLineSegment(sketch, "E9.12.8.0", {"start": v(20.05, 48.46) * mm, "end": v(23.05, 48.46) * mm});
            skLineSegment(sketch, "E9.12.8.1", {"start": v(21.55, 51.06) * mm, "end": v(20.05, 48.46) * mm});
            skLineSegment(sketch, "E9.12.8.2", {"start": v(23.05, 48.46) * mm, "end": v(21.55, 51.06) * mm});
            skLineSegment(sketch, "E9.12.8.3", {"start": v(21.55, 51.06) * mm, "end": v(24.55, 51.06) * mm});
            skLineSegment(sketch, "E9.12.8.4", {"start": v(21.55, 51.06) * mm, "end": v(23.05, 53.66) * mm});
            skLineSegment(sketch, "E9.12.8.5", {"start": v(24.55, 51.06) * mm, "end": v(23.05, 53.66) * mm});
            skLineSegment(sketch, "E9.12.9.0", {"start": v(20.05, 53.66) * mm, "end": v(23.05, 53.66) * mm});
            skLineSegment(sketch, "E9.12.9.1", {"start": v(21.55, 56.26) * mm, "end": v(20.05, 53.66) * mm});
            skLineSegment(sketch, "E9.12.9.2", {"start": v(23.05, 53.66) * mm, "end": v(21.55, 56.26) * mm});
            skLineSegment(sketch, "E9.12.9.3", {"start": v(21.55, 56.26) * mm, "end": v(24.55, 56.26) * mm});
            skLineSegment(sketch, "E9.12.9.4", {"start": v(21.55, 56.26) * mm, "end": v(23.05, 58.86) * mm});
            skLineSegment(sketch, "E9.12.9.5", {"start": v(24.55, 56.26) * mm, "end": v(23.05, 58.86) * mm});
            skLineSegment(sketch, "E9.13.0.0", {"start": v(23.05, 6.9) * mm, "end": v(26.05, 6.9) * mm});
            skLineSegment(sketch, "E9.13.0.1", {"start": v(24.55, 9.5) * mm, "end": v(23.05, 6.9) * mm});
            skLineSegment(sketch, "E9.13.0.2", {"start": v(26.05, 6.9) * mm, "end": v(24.55, 9.5) * mm});
            skLineSegment(sketch, "E9.13.0.3", {"start": v(24.55, 9.5) * mm, "end": v(27.55, 9.5) * mm});
            skLineSegment(sketch, "E9.13.0.4", {"start": v(24.55, 9.5) * mm, "end": v(26.05, 12.1) * mm});
            skLineSegment(sketch, "E9.13.0.5", {"start": v(27.55, 9.5) * mm, "end": v(26.05, 12.1) * mm});
            skLineSegment(sketch, "E9.13.1.0", {"start": v(23.05, 12.1) * mm, "end": v(26.05, 12.1) * mm});
            skLineSegment(sketch, "E9.13.1.1", {"start": v(24.55, 14.69) * mm, "end": v(23.05, 12.1) * mm});
            skLineSegment(sketch, "E9.13.1.2", {"start": v(26.05, 12.1) * mm, "end": v(24.55, 14.69) * mm});
            skLineSegment(sketch, "E9.13.1.3", {"start": v(24.55, 14.69) * mm, "end": v(27.55, 14.69) * mm});
            skLineSegment(sketch, "E9.13.1.4", {"start": v(24.55, 14.69) * mm, "end": v(26.05, 17.29) * mm});
            skLineSegment(sketch, "E9.13.1.5", {"start": v(27.55, 14.69) * mm, "end": v(26.05, 17.29) * mm});
            skLineSegment(sketch, "E9.13.2.0", {"start": v(23.05, 17.29) * mm, "end": v(26.05, 17.29) * mm});
            skLineSegment(sketch, "E9.13.2.1", {"start": v(24.55, 19.89) * mm, "end": v(23.05, 17.29) * mm});
            skLineSegment(sketch, "E9.13.2.2", {"start": v(26.05, 17.29) * mm, "end": v(24.55, 19.89) * mm});
            skLineSegment(sketch, "E9.13.2.3", {"start": v(24.55, 19.89) * mm, "end": v(27.55, 19.89) * mm});
            skLineSegment(sketch, "E9.13.2.4", {"start": v(24.55, 19.89) * mm, "end": v(26.05, 22.48) * mm});
            skLineSegment(sketch, "E9.13.2.5", {"start": v(27.55, 19.89) * mm, "end": v(26.05, 22.48) * mm});
            skLineSegment(sketch, "E9.13.3.0", {"start": v(23.05, 22.48) * mm, "end": v(26.05, 22.48) * mm});
            skLineSegment(sketch, "E9.13.3.1", {"start": v(24.55, 25.08) * mm, "end": v(23.05, 22.48) * mm});
            skLineSegment(sketch, "E9.13.3.2", {"start": v(26.05, 22.48) * mm, "end": v(24.55, 25.08) * mm});
            skLineSegment(sketch, "E9.13.3.3", {"start": v(24.55, 25.08) * mm, "end": v(27.55, 25.08) * mm});
            skLineSegment(sketch, "E9.13.3.4", {"start": v(24.55, 25.08) * mm, "end": v(26.05, 27.68) * mm});
            skLineSegment(sketch, "E9.13.3.5", {"start": v(27.55, 25.08) * mm, "end": v(26.05, 27.68) * mm});
            skLineSegment(sketch, "E9.13.4.0", {"start": v(23.05, 27.68) * mm, "end": v(26.05, 27.68) * mm});
            skLineSegment(sketch, "E9.13.4.1", {"start": v(24.55, 30.28) * mm, "end": v(23.05, 27.68) * mm});
            skLineSegment(sketch, "E9.13.4.2", {"start": v(26.05, 27.68) * mm, "end": v(24.55, 30.28) * mm});
            skLineSegment(sketch, "E9.13.4.3", {"start": v(24.55, 30.28) * mm, "end": v(27.55, 30.28) * mm});
            skLineSegment(sketch, "E9.13.4.4", {"start": v(24.55, 30.28) * mm, "end": v(26.05, 32.88) * mm});
            skLineSegment(sketch, "E9.13.4.5", {"start": v(27.55, 30.28) * mm, "end": v(26.05, 32.88) * mm});
            skLineSegment(sketch, "E9.13.5.0", {"start": v(23.05, 32.88) * mm, "end": v(26.05, 32.88) * mm});
            skLineSegment(sketch, "E9.13.5.1", {"start": v(24.55, 35.47) * mm, "end": v(23.05, 32.88) * mm});
            skLineSegment(sketch, "E9.13.5.2", {"start": v(26.05, 32.88) * mm, "end": v(24.55, 35.47) * mm});
            skLineSegment(sketch, "E9.13.5.3", {"start": v(24.55, 35.47) * mm, "end": v(27.55, 35.47) * mm});
            skLineSegment(sketch, "E9.13.5.4", {"start": v(24.55, 35.47) * mm, "end": v(26.05, 38.07) * mm});
            skLineSegment(sketch, "E9.13.5.5", {"start": v(27.55, 35.47) * mm, "end": v(26.05, 38.07) * mm});
            skLineSegment(sketch, "E9.13.6.0", {"start": v(23.05, 38.07) * mm, "end": v(26.05, 38.07) * mm});
            skLineSegment(sketch, "E9.13.6.1", {"start": v(24.55, 40.67) * mm, "end": v(23.05, 38.07) * mm});
            skLineSegment(sketch, "E9.13.6.2", {"start": v(26.05, 38.07) * mm, "end": v(24.55, 40.67) * mm});
            skLineSegment(sketch, "E9.13.6.3", {"start": v(24.55, 40.67) * mm, "end": v(27.55, 40.67) * mm});
            skLineSegment(sketch, "E9.13.6.4", {"start": v(24.55, 40.67) * mm, "end": v(26.05, 43.27) * mm});
            skLineSegment(sketch, "E9.13.6.5", {"start": v(27.55, 40.67) * mm, "end": v(26.05, 43.27) * mm});
            skLineSegment(sketch, "E9.13.7.0", {"start": v(23.05, 43.27) * mm, "end": v(26.05, 43.27) * mm});
            skLineSegment(sketch, "E9.13.7.1", {"start": v(24.55, 45.87) * mm, "end": v(23.05, 43.27) * mm});
            skLineSegment(sketch, "E9.13.7.2", {"start": v(26.05, 43.27) * mm, "end": v(24.55, 45.87) * mm});
            skLineSegment(sketch, "E9.13.7.3", {"start": v(24.55, 45.87) * mm, "end": v(27.55, 45.87) * mm});
            skLineSegment(sketch, "E9.13.7.4", {"start": v(24.55, 45.87) * mm, "end": v(26.05, 48.46) * mm});
            skLineSegment(sketch, "E9.13.7.5", {"start": v(27.55, 45.87) * mm, "end": v(26.05, 48.46) * mm});
            skLineSegment(sketch, "E9.13.8.0", {"start": v(23.05, 48.46) * mm, "end": v(26.05, 48.46) * mm});
            skLineSegment(sketch, "E9.13.8.1", {"start": v(24.55, 51.06) * mm, "end": v(23.05, 48.46) * mm});
            skLineSegment(sketch, "E9.13.8.2", {"start": v(26.05, 48.46) * mm, "end": v(24.55, 51.06) * mm});
            skLineSegment(sketch, "E9.13.8.3", {"start": v(24.55, 51.06) * mm, "end": v(27.55, 51.06) * mm});
            skLineSegment(sketch, "E9.13.8.4", {"start": v(24.55, 51.06) * mm, "end": v(26.05, 53.66) * mm});
            skLineSegment(sketch, "E9.13.8.5", {"start": v(27.55, 51.06) * mm, "end": v(26.05, 53.66) * mm});
            skLineSegment(sketch, "E9.13.9.0", {"start": v(23.05, 53.66) * mm, "end": v(26.05, 53.66) * mm});
            skLineSegment(sketch, "E9.13.9.1", {"start": v(24.55, 56.26) * mm, "end": v(23.05, 53.66) * mm});
            skLineSegment(sketch, "E9.13.9.2", {"start": v(26.05, 53.66) * mm, "end": v(24.55, 56.26) * mm});
            skLineSegment(sketch, "E9.13.9.3", {"start": v(24.55, 56.26) * mm, "end": v(27.55, 56.26) * mm});
            skLineSegment(sketch, "E9.13.9.4", {"start": v(24.55, 56.26) * mm, "end": v(26.05, 58.86) * mm});
            skLineSegment(sketch, "E9.13.9.5", {"start": v(27.55, 56.26) * mm, "end": v(26.05, 58.86) * mm});
            skLineSegment(sketch, "E9.14.0.0", {"start": v(26.05, 6.9) * mm, "end": v(29.05, 6.9) * mm});
            skLineSegment(sketch, "E9.14.0.1", {"start": v(27.55, 9.5) * mm, "end": v(26.05, 6.9) * mm});
            skLineSegment(sketch, "E9.14.0.2", {"start": v(29.05, 6.9) * mm, "end": v(27.55, 9.5) * mm});
            skLineSegment(sketch, "E9.14.0.3", {"start": v(27.55, 9.5) * mm, "end": v(30.55, 9.5) * mm});
            skLineSegment(sketch, "E9.14.0.4", {"start": v(27.55, 9.5) * mm, "end": v(29.05, 12.1) * mm});
            skLineSegment(sketch, "E9.14.0.5", {"start": v(30.55, 9.5) * mm, "end": v(29.05, 12.1) * mm});
            skLineSegment(sketch, "E9.14.1.0", {"start": v(26.05, 12.1) * mm, "end": v(29.05, 12.1) * mm});
            skLineSegment(sketch, "E9.14.1.1", {"start": v(27.55, 14.69) * mm, "end": v(26.05, 12.1) * mm});
            skLineSegment(sketch, "E9.14.1.2", {"start": v(29.05, 12.1) * mm, "end": v(27.55, 14.69) * mm});
            skLineSegment(sketch, "E9.14.1.3", {"start": v(27.55, 14.69) * mm, "end": v(30.55, 14.69) * mm});
            skLineSegment(sketch, "E9.14.1.4", {"start": v(27.55, 14.69) * mm, "end": v(29.05, 17.29) * mm});
            skLineSegment(sketch, "E9.14.1.5", {"start": v(30.55, 14.69) * mm, "end": v(29.05, 17.29) * mm});
            skLineSegment(sketch, "E9.14.2.0", {"start": v(26.05, 17.29) * mm, "end": v(29.05, 17.29) * mm});
            skLineSegment(sketch, "E9.14.2.1", {"start": v(27.55, 19.89) * mm, "end": v(26.05, 17.29) * mm});
            skLineSegment(sketch, "E9.14.2.2", {"start": v(29.05, 17.29) * mm, "end": v(27.55, 19.89) * mm});
            skLineSegment(sketch, "E9.14.2.3", {"start": v(27.55, 19.89) * mm, "end": v(30.55, 19.89) * mm});
            skLineSegment(sketch, "E9.14.2.4", {"start": v(27.55, 19.89) * mm, "end": v(29.05, 22.48) * mm});
            skLineSegment(sketch, "E9.14.2.5", {"start": v(30.55, 19.89) * mm, "end": v(29.05, 22.48) * mm});
            skLineSegment(sketch, "E9.14.3.0", {"start": v(26.05, 22.48) * mm, "end": v(29.05, 22.48) * mm});
            skLineSegment(sketch, "E9.14.3.1", {"start": v(27.55, 25.08) * mm, "end": v(26.05, 22.48) * mm});
            skLineSegment(sketch, "E9.14.3.2", {"start": v(29.05, 22.48) * mm, "end": v(27.55, 25.08) * mm});
            skLineSegment(sketch, "E9.14.3.3", {"start": v(27.55, 25.08) * mm, "end": v(30.55, 25.08) * mm});
            skLineSegment(sketch, "E9.14.3.4", {"start": v(27.55, 25.08) * mm, "end": v(29.05, 27.68) * mm});
            skLineSegment(sketch, "E9.14.3.5", {"start": v(30.55, 25.08) * mm, "end": v(29.05, 27.68) * mm});
            skLineSegment(sketch, "E9.14.4.0", {"start": v(26.05, 27.68) * mm, "end": v(29.05, 27.68) * mm});
            skLineSegment(sketch, "E9.14.4.1", {"start": v(27.55, 30.28) * mm, "end": v(26.05, 27.68) * mm});
            skLineSegment(sketch, "E9.14.4.2", {"start": v(29.05, 27.68) * mm, "end": v(27.55, 30.28) * mm});
            skLineSegment(sketch, "E9.14.4.3", {"start": v(27.55, 30.28) * mm, "end": v(30.55, 30.28) * mm});
            skLineSegment(sketch, "E9.14.4.4", {"start": v(27.55, 30.28) * mm, "end": v(29.05, 32.88) * mm});
            skLineSegment(sketch, "E9.14.4.5", {"start": v(30.55, 30.28) * mm, "end": v(29.05, 32.88) * mm});
            skLineSegment(sketch, "E9.14.5.0", {"start": v(26.05, 32.88) * mm, "end": v(29.05, 32.88) * mm});
            skLineSegment(sketch, "E9.14.5.1", {"start": v(27.55, 35.47) * mm, "end": v(26.05, 32.88) * mm});
            skLineSegment(sketch, "E9.14.5.2", {"start": v(29.05, 32.88) * mm, "end": v(27.55, 35.47) * mm});
            skLineSegment(sketch, "E9.14.5.3", {"start": v(27.55, 35.47) * mm, "end": v(30.55, 35.47) * mm});
            skLineSegment(sketch, "E9.14.5.4", {"start": v(27.55, 35.47) * mm, "end": v(29.05, 38.07) * mm});
            skLineSegment(sketch, "E9.14.5.5", {"start": v(30.55, 35.47) * mm, "end": v(29.05, 38.07) * mm});
            skLineSegment(sketch, "E9.14.6.0", {"start": v(26.05, 38.07) * mm, "end": v(29.05, 38.07) * mm});
            skLineSegment(sketch, "E9.14.6.1", {"start": v(27.55, 40.67) * mm, "end": v(26.05, 38.07) * mm});
            skLineSegment(sketch, "E9.14.6.2", {"start": v(29.05, 38.07) * mm, "end": v(27.55, 40.67) * mm});
            skLineSegment(sketch, "E9.14.6.3", {"start": v(27.55, 40.67) * mm, "end": v(30.55, 40.67) * mm});
            skLineSegment(sketch, "E9.14.6.4", {"start": v(27.55, 40.67) * mm, "end": v(29.05, 43.27) * mm});
            skLineSegment(sketch, "E9.14.6.5", {"start": v(30.55, 40.67) * mm, "end": v(29.05, 43.27) * mm});
            skLineSegment(sketch, "E9.14.7.0", {"start": v(26.05, 43.27) * mm, "end": v(29.05, 43.27) * mm});
            skLineSegment(sketch, "E9.14.7.1", {"start": v(27.55, 45.87) * mm, "end": v(26.05, 43.27) * mm});
            skLineSegment(sketch, "E9.14.7.2", {"start": v(29.05, 43.27) * mm, "end": v(27.55, 45.87) * mm});
            skLineSegment(sketch, "E9.14.7.3", {"start": v(27.55, 45.87) * mm, "end": v(30.55, 45.87) * mm});
            skLineSegment(sketch, "E9.14.7.4", {"start": v(27.55, 45.87) * mm, "end": v(29.05, 48.46) * mm});
            skLineSegment(sketch, "E9.14.7.5", {"start": v(30.55, 45.87) * mm, "end": v(29.05, 48.46) * mm});
            skLineSegment(sketch, "E9.14.8.0", {"start": v(26.05, 48.46) * mm, "end": v(29.05, 48.46) * mm});
            skLineSegment(sketch, "E9.14.8.1", {"start": v(27.55, 51.06) * mm, "end": v(26.05, 48.46) * mm});
            skLineSegment(sketch, "E9.14.8.2", {"start": v(29.05, 48.46) * mm, "end": v(27.55, 51.06) * mm});
            skLineSegment(sketch, "E9.14.8.3", {"start": v(27.55, 51.06) * mm, "end": v(30.55, 51.06) * mm});
            skLineSegment(sketch, "E9.14.8.4", {"start": v(27.55, 51.06) * mm, "end": v(29.05, 53.66) * mm});
            skLineSegment(sketch, "E9.14.8.5", {"start": v(30.55, 51.06) * mm, "end": v(29.05, 53.66) * mm});
            skLineSegment(sketch, "E9.14.9.0", {"start": v(26.05, 53.66) * mm, "end": v(29.05, 53.66) * mm});
            skLineSegment(sketch, "E9.14.9.1", {"start": v(27.55, 56.26) * mm, "end": v(26.05, 53.66) * mm});
            skLineSegment(sketch, "E9.14.9.2", {"start": v(29.05, 53.66) * mm, "end": v(27.55, 56.26) * mm});
            skLineSegment(sketch, "E9.14.9.3", {"start": v(27.55, 56.26) * mm, "end": v(30.55, 56.26) * mm});
            skLineSegment(sketch, "E9.14.9.4", {"start": v(27.55, 56.26) * mm, "end": v(29.05, 58.86) * mm});
            skLineSegment(sketch, "E9.14.9.5", {"start": v(30.55, 56.26) * mm, "end": v(29.05, 58.86) * mm});
            skLineSegment(sketch, "E9.direction1", {"start": v(-15.95, 6.9) * mm, "end": v(-12.95, 6.9) * mm, "construction": true});
            skLineSegment(sketch, "E9.direction2", {"start": v(-15.95, 6.9) * mm, "end": v(-15.95, 12.1) * mm, "construction": true});
            skSolve(sketch);
        }
        {
            var Q0;
            Q0=makeQuery(id+"F0.imprint","IMPRINT",FACE,{"disambiguationData":[TD([[makeQuery(id+"F0.imprint","IMPRINT",EDGE,{"derivedFrom":sQuery(id+"F0.wireOp",EDGE,"E9.6.7.3")}),1.0]])]});
            var Q1;
            {var subQ0=sQuery(id+"F0.wireOp",EDGE,"E9.6.7.5");Q1=makeQuery(id+"F0.imprint","IMPRINT",FACE,{"disambiguationData":[TD([[makeQuery(id+"F0.imprint","IMPRINT",EDGE,{"derivedFrom":subQ0}),-1.0]])]});}
            var Q2;
            Q2=makeQuery(id+"F0.imprint","IMPRINT",FACE,{"disambiguationData":[TD([[makeQuery(id+"F0.imprint","IMPRINT",EDGE,{"derivedFrom":sQuery(id+"F0.wireOp",EDGE,"E9.7.7.3")}),1.0]])]});
            var Q3;
            Q3=makeQuery(id+"F0.imprint","IMPRINT",FACE,{"disambiguationData":[TD([[makeQuery(id+"F0.imprint","IMPRINT",EDGE,{"derivedFrom":sQuery(id+"F0.wireOp",EDGE,"E9.6.7.2")}),-1.0]])]});
            var Q4;
            {var subQ0=sQuery(id+"F0.wireOp",EDGE,"E9.7.7.1");Q4=makeQuery(id+"F0.imprint","IMPRINT",FACE,{"disambiguationData":[TD([[makeQuery(id+"F0.imprint","IMPRINT",EDGE,{"derivedFrom":subQ0}),1.0]])]});}
            var Q5;
            Q5=makeQuery(id+"F0.imprint","IMPRINT",FACE,{"disambiguationData":[TD([[makeQuery(id+"F0.imprint","IMPRINT",EDGE,{"derivedFrom":sQuery(id+"F0.wireOp",EDGE,"E9.7.7.2")}),-1.0]])]});
            var Q6;
            {var subQ0=sQuery(id+"F0.wireOp",EDGE,"E9.5.6.5");Q6=makeQuery(id+"F0.imprint","IMPRINT",FACE,{"disambiguationData":[TD([[makeQuery(id+"F0.imprint","IMPRINT",EDGE,{"derivedFrom":subQ0}),-1.0]])]});}
            var Q7;
            {var subQ0=sQuery(id+"F0.wireOp",EDGE,"E9.6.6.5");Q7=makeQuery(id+"F0.imprint","IMPRINT",FACE,{"disambiguationData":[TD([[makeQuery(id+"F0.imprint","IMPRINT",EDGE,{"derivedFrom":subQ0}),-1.0]])]});}
            var Q8;
            Q8=makeQuery(id+"F0.imprint","IMPRINT",FACE,{"disambiguationData":[TD([[makeQuery(id+"F0.imprint","IMPRINT",EDGE,{"derivedFrom":sQuery(id+"F0.wireOp",EDGE,"E9.6.6.3")}),1.0]])]});
            var Q9;
            Q9=makeQuery(id+"F0.imprint","IMPRINT",FACE,{"disambiguationData":[TD([[makeQuery(id+"F0.imprint","IMPRINT",EDGE,{"derivedFrom":sQuery(id+"F0.wireOp",EDGE,"E9.7.6.3")}),1.0]])]});
            var Q10;
            {var subQ0=sQuery(id+"F0.wireOp",EDGE,"E9.7.6.5");Q10=makeQuery(id+"F0.imprint","IMPRINT",FACE,{"disambiguationData":[TD([[makeQuery(id+"F0.imprint","IMPRINT",EDGE,{"derivedFrom":subQ0}),-1.0]])]});}
            var Q11;
            Q11=makeQuery(id+"F0.imprint","IMPRINT",FACE,{"disambiguationData":[TD([[makeQuery(id+"F0.imprint","IMPRINT",EDGE,{"derivedFrom":sQuery(id+"F0.wireOp",EDGE,"E9.5.6.3")}),1.0]])]});
            var Q12;
            Q12=makeQuery(id+"F0.imprint","IMPRINT",FACE,{"disambiguationData":[TD([[makeQuery(id+"F0.imprint","IMPRINT",EDGE,{"derivedFrom":sQuery(id+"F0.wireOp",EDGE,"E9.5.6.2")}),-1.0]])]});
            var Q13;
            Q13=makeQuery(id+"F0.imprint","IMPRINT",FACE,{"disambiguationData":[TD([[makeQuery(id+"F0.imprint","IMPRINT",EDGE,{"derivedFrom":sQuery(id+"F0.wireOp",EDGE,"E9.6.6.2")}),-1.0]])]});
            var Q14;
            {var subQ0=sQuery(id+"F0.wireOp",EDGE,"E9.7.6.1");Q14=makeQuery(id+"F0.imprint","IMPRINT",FACE,{"disambiguationData":[TD([[makeQuery(id+"F0.imprint","IMPRINT",EDGE,{"derivedFrom":subQ0}),1.0]])]});}
            var Q15;
            Q15=makeQuery(id+"F0.imprint","IMPRINT",FACE,{"disambiguationData":[TD([[makeQuery(id+"F0.imprint","IMPRINT",EDGE,{"derivedFrom":sQuery(id+"F0.wireOp",EDGE,"E9.7.6.2")}),-1.0]])]});
            var Q16;
            {var subQ0=sQuery(id+"F0.wireOp",EDGE,"E9.8.6.1");Q16=makeQuery(id+"F0.imprint","IMPRINT",FACE,{"disambiguationData":[TD([[makeQuery(id+"F0.imprint","IMPRINT",EDGE,{"derivedFrom":subQ0}),1.0]])]});}
            var Q17;
            Q17=makeQuery(id+"F0.imprint","IMPRINT",FACE,{"disambiguationData":[TD([[makeQuery(id+"F0.imprint","IMPRINT",EDGE,{"derivedFrom":sQuery(id+"F0.wireOp",EDGE,"E9.8.6.3")}),1.0]])]});
            var Q18;
            Q18=makeQuery(id+"F0.imprint","IMPRINT",FACE,{"disambiguationData":[TD([[makeQuery(id+"F0.imprint","IMPRINT",EDGE,{"derivedFrom":sQuery(id+"F0.wireOp",EDGE,"E9.8.6.2")}),-1.0]])]});
            var Q19;
            {var subQ0=sQuery(id+"F0.wireOp",EDGE,"E9.5.6.1");Q19=makeQuery(id+"F0.imprint","IMPRINT",FACE,{"disambiguationData":[TD([[makeQuery(id+"F0.imprint","IMPRINT",EDGE,{"derivedFrom":subQ0}),1.0]])]});}
            var Q20;
            {var subQ0=sQuery(id+"F0.wireOp",EDGE,"E9.4.5.5");Q20=makeQuery(id+"F0.imprint","IMPRINT",FACE,{"disambiguationData":[TD([[makeQuery(id+"F0.imprint","IMPRINT",EDGE,{"derivedFrom":subQ0}),-1.0]])]});}
            var Q21;
            {var subQ0=sQuery(id+"F0.wireOp",EDGE,"E9.6.5.5");Q21=makeQuery(id+"F0.imprint","IMPRINT",FACE,{"disambiguationData":[TD([[makeQuery(id+"F0.imprint","IMPRINT",EDGE,{"derivedFrom":subQ0}),-1.0]])]});}
            var Q22;
            Q22=makeQuery(id+"F0.imprint","IMPRINT",FACE,{"disambiguationData":[TD([[makeQuery(id+"F0.imprint","IMPRINT",EDGE,{"derivedFrom":sQuery(id+"F0.wireOp",EDGE,"E9.6.5.3")}),1.0]])]});
            var Q23;
            {var subQ0=sQuery(id+"F0.wireOp",EDGE,"E9.6.5.1");Q23=makeQuery(id+"F0.imprint","IMPRINT",FACE,{"disambiguationData":[TD([[makeQuery(id+"F0.imprint","IMPRINT",EDGE,{"derivedFrom":subQ0}),1.0]])]});}
            var Q24;
            {var subQ0=sQuery(id+"F0.wireOp",EDGE,"E9.9.6.1");Q24=makeQuery(id+"F0.imprint","IMPRINT",FACE,{"disambiguationData":[TD([[makeQuery(id+"F0.imprint","IMPRINT",EDGE,{"derivedFrom":subQ0}),1.0]])]});}
            var Q25;
            {var subQ0=sQuery(id+"F0.wireOp",EDGE,"E9.8.5.5");Q25=makeQuery(id+"F0.imprint","IMPRINT",FACE,{"disambiguationData":[TD([[makeQuery(id+"F0.imprint","IMPRINT",EDGE,{"derivedFrom":subQ0}),-1.0]])]});}
            var Q26;
            {var subQ0=sQuery(id+"F0.wireOp",EDGE,"E9.7.5.1");Q26=makeQuery(id+"F0.imprint","IMPRINT",FACE,{"disambiguationData":[TD([[makeQuery(id+"F0.imprint","IMPRINT",EDGE,{"derivedFrom":subQ0}),1.0]])]});}
            var Q27;
            Q27=makeQuery(id+"F0.imprint","IMPRINT",FACE,{"disambiguationData":[TD([[makeQuery(id+"F0.imprint","IMPRINT",EDGE,{"derivedFrom":sQuery(id+"F0.wireOp",EDGE,"E9.6.5.2")}),-1.0]])]});
            var Q28;
            Q28=makeQuery(id+"F0.imprint","IMPRINT",FACE,{"disambiguationData":[TD([[makeQuery(id+"F0.imprint","IMPRINT",EDGE,{"derivedFrom":sQuery(id+"F0.wireOp",EDGE,"E9.4.6.3")}),1.0]])]});
            var Q29;
            Q29=makeQuery(id+"F0.imprint","IMPRINT",FACE,{"disambiguationData":[TD([[makeQuery(id+"F0.imprint","IMPRINT",EDGE,{"derivedFrom":sQuery(id+"F0.wireOp",EDGE,"E9.4.6.2")}),-1.0]])]});
            var Q30;
            {var subQ0=sQuery(id+"F0.wireOp",EDGE,"E9.3.6.5");Q30=makeQuery(id+"F0.imprint","IMPRINT",FACE,{"disambiguationData":[TD([[makeQuery(id+"F0.imprint","IMPRINT",EDGE,{"derivedFrom":subQ0}),-1.0]])]});}
            var Q31;
            Q31=makeQuery(id+"F0.imprint","IMPRINT",FACE,{"disambiguationData":[TD([[makeQuery(id+"F0.imprint","IMPRINT",EDGE,{"derivedFrom":sQuery(id+"F0.wireOp",EDGE,"E9.3.6.3")}),1.0]])]});
            var Q32;
            Q32=makeQuery(id+"F0.imprint","IMPRINT",FACE,{"disambiguationData":[TD([[makeQuery(id+"F0.imprint","IMPRINT",EDGE,{"derivedFrom":sQuery(id+"F0.wireOp",EDGE,"E9.3.6.2")}),-1.0]])]});
            var Q33;
            {var subQ0=sQuery(id+"F0.wireOp",EDGE,"E9.3.6.1");Q33=makeQuery(id+"F0.imprint","IMPRINT",FACE,{"disambiguationData":[TD([[makeQuery(id+"F0.imprint","IMPRINT",EDGE,{"derivedFrom":subQ0}),1.0]])]});}
            var Q34;
            Q34=makeQuery(id+"F0.imprint","IMPRINT",FACE,{"disambiguationData":[TD([[makeQuery(id+"F0.imprint","IMPRINT",EDGE,{"derivedFrom":sQuery(id+"F0.wireOp",EDGE,"E9.4.5.3")}),1.0]])]});
            var Q35;
            Q35=makeQuery(id+"F0.imprint","IMPRINT",FACE,{"disambiguationData":[TD([[makeQuery(id+"F0.imprint","IMPRINT",EDGE,{"derivedFrom":sQuery(id+"F0.wireOp",EDGE,"E9.4.5.2")}),-1.0]])]});
            var Q36;
            Q36=makeQuery(id+"F0.imprint","IMPRINT",FACE,{"disambiguationData":[TD([[makeQuery(id+"F0.imprint","IMPRINT",EDGE,{"derivedFrom":sQuery(id+"F0.wireOp",EDGE,"E9.5.4.2")}),-1.0]])]});
            var Q37;
            Q37=makeQuery(id+"F0.imprint","IMPRINT",FACE,{"disambiguationData":[TD([[makeQuery(id+"F0.imprint","IMPRINT",EDGE,{"derivedFrom":sQuery(id+"F0.wireOp",EDGE,"E9.5.3.3")}),1.0]])]});
            var Q38;
            Q38=makeQuery(id+"F0.imprint","IMPRINT",FACE,{"disambiguationData":[TD([[makeQuery(id+"F0.imprint","IMPRINT",EDGE,{"derivedFrom":sQuery(id+"F0.wireOp",EDGE,"E9.4.3.2")}),-1.0]])]});
            var Q39;
            {var subQ0=sQuery(id+"F0.wireOp",EDGE,"E9.4.3.1");Q39=makeQuery(id+"F0.imprint","IMPRINT",FACE,{"disambiguationData":[TD([[makeQuery(id+"F0.imprint","IMPRINT",EDGE,{"derivedFrom":subQ0}),1.0]])]});}
            var Q40;
            {var subQ0=sQuery(id+"F0.wireOp",EDGE,"E9.3.2.5");Q40=makeQuery(id+"F0.imprint","IMPRINT",FACE,{"disambiguationData":[TD([[makeQuery(id+"F0.imprint","IMPRINT",EDGE,{"derivedFrom":subQ0}),-1.0]])]});}
            var Q41;
            Q41=makeQuery(id+"F0.imprint","IMPRINT",FACE,{"disambiguationData":[TD([[makeQuery(id+"F0.imprint","IMPRINT",EDGE,{"derivedFrom":sQuery(id+"F0.wireOp",EDGE,"E9.4.2.3")}),1.0]])]});
            var Q42;
            {var subQ0=sQuery(id+"F0.wireOp",EDGE,"E9.5.3.1");Q42=makeQuery(id+"F0.imprint","IMPRINT",FACE,{"disambiguationData":[TD([[makeQuery(id+"F0.imprint","IMPRINT",EDGE,{"derivedFrom":subQ0}),1.0]])]});}
            var Q43;
            {var subQ0=sQuery(id+"F0.wireOp",EDGE,"E9.4.2.5");Q43=makeQuery(id+"F0.imprint","IMPRINT",FACE,{"disambiguationData":[TD([[makeQuery(id+"F0.imprint","IMPRINT",EDGE,{"derivedFrom":subQ0}),-1.0]])]});}
            var Q44;
            Q44=makeQuery(id+"F0.imprint","IMPRINT",FACE,{"disambiguationData":[TD([[makeQuery(id+"F0.imprint","IMPRINT",EDGE,{"derivedFrom":sQuery(id+"F0.wireOp",EDGE,"E9.5.3.2")}),-1.0]])]});
            var Q45;
            Q45=makeQuery(id+"F0.imprint","IMPRINT",FACE,{"disambiguationData":[TD([[makeQuery(id+"F0.imprint","IMPRINT",EDGE,{"derivedFrom":sQuery(id+"F0.wireOp",EDGE,"E9.6.3.2")}),-1.0]])]});
            var Q46;
            {var subQ0=sQuery(id+"F0.wireOp",EDGE,"E9.7.3.1");Q46=makeQuery(id+"F0.imprint","IMPRINT",FACE,{"disambiguationData":[TD([[makeQuery(id+"F0.imprint","IMPRINT",EDGE,{"derivedFrom":subQ0}),1.0]])]});}
            var Q47;
            Q47=makeQuery(id+"F0.imprint","IMPRINT",FACE,{"disambiguationData":[TD([[makeQuery(id+"F0.imprint","IMPRINT",EDGE,{"derivedFrom":sQuery(id+"F0.wireOp",EDGE,"E9.7.3.2")}),-1.0]])]});
            var Q48;
            {var subQ0=sQuery(id+"F0.wireOp",EDGE,"E9.6.4.1");Q48=makeQuery(id+"F0.imprint","IMPRINT",FACE,{"disambiguationData":[TD([[makeQuery(id+"F0.imprint","IMPRINT",EDGE,{"derivedFrom":subQ0}),1.0]])]});}
            var Q49;
            Q49=makeQuery(id+"F0.imprint","IMPRINT",FACE,{"disambiguationData":[TD([[makeQuery(id+"F0.imprint","IMPRINT",EDGE,{"derivedFrom":sQuery(id+"F0.wireOp",EDGE,"E9.6.4.2")}),-1.0]])]});
            var Q50;
            {var subQ0=sQuery(id+"F0.wireOp",EDGE,"E9.6.4.5");Q50=makeQuery(id+"F0.imprint","IMPRINT",FACE,{"disambiguationData":[TD([[makeQuery(id+"F0.imprint","IMPRINT",EDGE,{"derivedFrom":subQ0}),-1.0]])]});}
            var Q51;
            Q51=makeQuery(id+"F0.imprint","IMPRINT",FACE,{"disambiguationData":[TD([[makeQuery(id+"F0.imprint","IMPRINT",EDGE,{"derivedFrom":sQuery(id+"F0.wireOp",EDGE,"E9.7.4.3")}),1.0]])]});
            var Q52;
            {var subQ0=sQuery(id+"F0.wireOp",EDGE,"E9.4.5.1");Q52=makeQuery(id+"F0.imprint","IMPRINT",FACE,{"disambiguationData":[TD([[makeQuery(id+"F0.imprint","IMPRINT",EDGE,{"derivedFrom":subQ0}),1.0]])]});}
            var Q53;
            {var subQ0=sQuery(id+"F0.wireOp",EDGE,"E9.3.4.5");Q53=makeQuery(id+"F0.imprint","IMPRINT",FACE,{"disambiguationData":[TD([[makeQuery(id+"F0.imprint","IMPRINT",EDGE,{"derivedFrom":subQ0}),-1.0]])]});}
            var Q54;
            Q54=makeQuery(id+"F0.imprint","IMPRINT",FACE,{"disambiguationData":[TD([[makeQuery(id+"F0.imprint","IMPRINT",EDGE,{"derivedFrom":sQuery(id+"F0.wireOp",EDGE,"E9.4.4.2")}),-1.0]])]});
            var Q55;
            {var subQ0=sQuery(id+"F0.wireOp",EDGE,"E9.5.4.1");Q55=makeQuery(id+"F0.imprint","IMPRINT",FACE,{"disambiguationData":[TD([[makeQuery(id+"F0.imprint","IMPRINT",EDGE,{"derivedFrom":subQ0}),1.0]])]});}
            var Q56;
            Q56=makeQuery(id+"F0.imprint","IMPRINT",FACE,{"disambiguationData":[TD([[makeQuery(id+"F0.imprint","IMPRINT",EDGE,{"derivedFrom":sQuery(id+"F0.wireOp",EDGE,"E9.4.4.3")}),1.0]])]});
            var Q57;
            {var subQ0=sQuery(id+"F0.wireOp",EDGE,"E9.4.3.5");Q57=makeQuery(id+"F0.imprint","IMPRINT",FACE,{"disambiguationData":[TD([[makeQuery(id+"F0.imprint","IMPRINT",EDGE,{"derivedFrom":subQ0}),-1.0]])]});}
            var Q58;
            {var subQ0=sQuery(id+"F0.wireOp",EDGE,"E9.6.2.5");Q58=makeQuery(id+"F0.imprint","IMPRINT",FACE,{"disambiguationData":[TD([[makeQuery(id+"F0.imprint","IMPRINT",EDGE,{"derivedFrom":subQ0}),-1.0]])]});}
            var Q59;
            Q59=makeQuery(id+"F0.imprint","IMPRINT",FACE,{"disambiguationData":[TD([[makeQuery(id+"F0.imprint","IMPRINT",EDGE,{"derivedFrom":sQuery(id+"F0.wireOp",EDGE,"E9.8.3.3")}),1.0]])]});
            var Q60;
            {var subQ0=sQuery(id+"F0.wireOp",EDGE,"E9.7.4.5");Q60=makeQuery(id+"F0.imprint","IMPRINT",FACE,{"disambiguationData":[TD([[makeQuery(id+"F0.imprint","IMPRINT",EDGE,{"derivedFrom":subQ0}),-1.0]])]});}
            var Q61;
            Q61=makeQuery(id+"F0.imprint","IMPRINT",FACE,{"disambiguationData":[TD([[makeQuery(id+"F0.imprint","IMPRINT",EDGE,{"derivedFrom":sQuery(id+"F0.wireOp",EDGE,"E9.9.5.2")}),-1.0]])]});
            var Q62;
            Q62=makeQuery(id+"F0.imprint","IMPRINT",FACE,{"disambiguationData":[TD([[makeQuery(id+"F0.imprint","IMPRINT",EDGE,{"derivedFrom":sQuery(id+"F0.wireOp",EDGE,"E9.9.5.3")}),1.0]])]});
            var Q63;
            {var subQ0=sQuery(id+"F0.wireOp",EDGE,"E9.9.4.1");Q63=makeQuery(id+"F0.imprint","IMPRINT",FACE,{"disambiguationData":[TD([[makeQuery(id+"F0.imprint","IMPRINT",EDGE,{"derivedFrom":subQ0}),1.0]])]});}
            var Q64;
            Q64=makeQuery(id+"F0.imprint","IMPRINT",FACE,{"disambiguationData":[TD([[makeQuery(id+"F0.imprint","IMPRINT",EDGE,{"derivedFrom":sQuery(id+"F0.wireOp",EDGE,"E9.9.4.2")}),-1.0]])]});
            var Q65;
            Q65=makeQuery(id+"F0.imprint","IMPRINT",FACE,{"disambiguationData":[TD([[makeQuery(id+"F0.imprint","IMPRINT",EDGE,{"derivedFrom":sQuery(id+"F0.wireOp",EDGE,"E9.9.4.3")}),1.0]])]});
            var Q66;
            {var subQ0=sQuery(id+"F0.wireOp",EDGE,"E9.9.4.5");Q66=makeQuery(id+"F0.imprint","IMPRINT",FACE,{"disambiguationData":[TD([[makeQuery(id+"F0.imprint","IMPRINT",EDGE,{"derivedFrom":subQ0}),-1.0]])]});}
            var Q67;
            {var subQ0=sQuery(id+"F0.wireOp",EDGE,"E9.10.5.1");Q67=makeQuery(id+"F0.imprint","IMPRINT",FACE,{"disambiguationData":[TD([[makeQuery(id+"F0.imprint","IMPRINT",EDGE,{"derivedFrom":subQ0}),1.0]])]});}
            var Q68;
            {var subQ0=sQuery(id+"F0.wireOp",EDGE,"E9.8.3.5");Q68=makeQuery(id+"F0.imprint","IMPRINT",FACE,{"disambiguationData":[TD([[makeQuery(id+"F0.imprint","IMPRINT",EDGE,{"derivedFrom":subQ0}),-1.0]])]});}
            var Q69;
            {var subQ0=sQuery(id+"F0.wireOp",EDGE,"E9.6.3.1");Q69=makeQuery(id+"F0.imprint","IMPRINT",FACE,{"disambiguationData":[TD([[makeQuery(id+"F0.imprint","IMPRINT",EDGE,{"derivedFrom":subQ0}),1.0]])]});}
            var Q70;
            {var subQ0=sQuery(id+"F0.wireOp",EDGE,"E9.8.3.1");Q70=makeQuery(id+"F0.imprint","IMPRINT",FACE,{"disambiguationData":[TD([[makeQuery(id+"F0.imprint","IMPRINT",EDGE,{"derivedFrom":subQ0}),1.0]])]});}
            var Q71;
            Q71=makeQuery(id+"F0.imprint","IMPRINT",FACE,{"disambiguationData":[TD([[makeQuery(id+"F0.imprint","IMPRINT",EDGE,{"derivedFrom":sQuery(id+"F0.wireOp",EDGE,"E9.8.3.2")}),-1.0]])]});
            var Q72;
            {var subQ0=sQuery(id+"F0.wireOp",EDGE,"E9.9.3.1");Q72=makeQuery(id+"F0.imprint","IMPRINT",FACE,{"disambiguationData":[TD([[makeQuery(id+"F0.imprint","IMPRINT",EDGE,{"derivedFrom":subQ0}),1.0]])]});}
            var Q73;
            {var subQ0=sQuery(id+"F0.wireOp",EDGE,"E9.8.2.5");Q73=makeQuery(id+"F0.imprint","IMPRINT",FACE,{"disambiguationData":[TD([[makeQuery(id+"F0.imprint","IMPRINT",EDGE,{"derivedFrom":subQ0}),-1.0]])]});}
            var Q74;
            Q74=makeQuery(id+"F0.imprint","IMPRINT",FACE,{"disambiguationData":[TD([[makeQuery(id+"F0.imprint","IMPRINT",EDGE,{"derivedFrom":sQuery(id+"F0.wireOp",EDGE,"E9.9.3.2")}),-1.0]])]});
            var Q75;
            {var subQ0=sQuery(id+"F0.wireOp",EDGE,"E9.10.3.1");Q75=makeQuery(id+"F0.imprint","IMPRINT",FACE,{"disambiguationData":[TD([[makeQuery(id+"F0.imprint","IMPRINT",EDGE,{"derivedFrom":subQ0}),1.0]])]});}
            var Q76;
            {var subQ0=sQuery(id+"F0.wireOp",EDGE,"E9.9.2.5");Q76=makeQuery(id+"F0.imprint","IMPRINT",FACE,{"disambiguationData":[TD([[makeQuery(id+"F0.imprint","IMPRINT",EDGE,{"derivedFrom":subQ0}),-1.0]])]});}
            var Q77;
            Q77=makeQuery(id+"F0.imprint","IMPRINT",FACE,{"disambiguationData":[TD([[makeQuery(id+"F0.imprint","IMPRINT",EDGE,{"derivedFrom":sQuery(id+"F0.wireOp",EDGE,"E9.9.2.3")}),1.0]])]});
            var Q78;
            Q78=makeQuery(id+"F0.imprint","IMPRINT",FACE,{"disambiguationData":[TD([[makeQuery(id+"F0.imprint","IMPRINT",EDGE,{"derivedFrom":sQuery(id+"F0.wireOp",EDGE,"E9.2.5.2")}),-1.0]])]});
            var Q79;
            Q79=makeQuery(id+"F0.imprint","IMPRINT",FACE,{"disambiguationData":[TD([[makeQuery(id+"F0.imprint","IMPRINT",EDGE,{"derivedFrom":sQuery(id+"F0.wireOp",EDGE,"E9.2.5.3")}),1.0]])]});
            var Q80;
            {var subQ0=sQuery(id+"F0.wireOp",EDGE,"E9.2.5.5");Q80=makeQuery(id+"F0.imprint","IMPRINT",FACE,{"disambiguationData":[TD([[makeQuery(id+"F0.imprint","IMPRINT",EDGE,{"derivedFrom":subQ0}),-1.0]])]});}
            var Q81;
            Q81=makeQuery(id+"F0.imprint","IMPRINT",FACE,{"disambiguationData":[TD([[makeQuery(id+"F0.imprint","IMPRINT",EDGE,{"derivedFrom":sQuery(id+"F0.wireOp",EDGE,"E9.4.2.2")}),-1.0]])]});
            var Q82;
            Q82=makeQuery(id+"F0.imprint","IMPRINT",FACE,{"disambiguationData":[TD([[makeQuery(id+"F0.imprint","IMPRINT",EDGE,{"derivedFrom":sQuery(id+"F0.wireOp",EDGE,"E9.9.2.2")}),-1.0]])]});
            var Q83;
            Q83=makeQuery(id+"F0.imprint","IMPRINT",FACE,{"disambiguationData":[TD([[makeQuery(id+"F0.imprint","IMPRINT",EDGE,{"derivedFrom":sQuery(id+"F0.wireOp",EDGE,"E9.9.6.2")}),-1.0]])]});
            var Q84;
            Q84=makeQuery(id+"F0.imprint","IMPRINT",FACE,{"disambiguationData":[TD([[makeQuery(id+"F0.imprint","IMPRINT",EDGE,{"derivedFrom":sQuery(id+"F0.wireOp",EDGE,"E9.9.6.3")}),1.0]])]});
            var Q85;
            {var subQ0=sQuery(id+"F0.wireOp",EDGE,"E9.4.6.1");Q85=makeQuery(id+"F0.imprint","IMPRINT",FACE,{"disambiguationData":[TD([[makeQuery(id+"F0.imprint","IMPRINT",EDGE,{"derivedFrom":subQ0}),1.0]])]});}
            var Q86;
            Q86=makeQuery(id+"F0.imprint","IMPRINT",FACE,{"disambiguationData":[TD([[makeQuery(id+"F0.imprint","IMPRINT",EDGE,{"derivedFrom":sQuery(id+"F0.wireOp",EDGE,"E9.10.6.2")}),-1.0]])]});
            var Q87;
            {var subQ0=sQuery(id+"F0.wireOp",EDGE,"E9.9.6.5");Q87=makeQuery(id+"F0.imprint","IMPRINT",FACE,{"disambiguationData":[TD([[makeQuery(id+"F0.imprint","IMPRINT",EDGE,{"derivedFrom":subQ0}),-1.0]])]});}
            var Q88;
            Q88=makeQuery(id+"F0.imprint","IMPRINT",FACE,{"disambiguationData":[TD([[makeQuery(id+"F0.imprint","IMPRINT",EDGE,{"derivedFrom":sQuery(id+"F0.wireOp",EDGE,"E9.10.6.3")}),1.0]])]});
            var Q89;
            {var subQ0=sQuery(id+"F0.wireOp",EDGE,"E9.11.6.1");Q89=makeQuery(id+"F0.imprint","IMPRINT",FACE,{"disambiguationData":[TD([[makeQuery(id+"F0.imprint","IMPRINT",EDGE,{"derivedFrom":subQ0}),1.0]])]});}
            var Q90;
            {var subQ0=sQuery(id+"F0.wireOp",EDGE,"E9.10.5.5");Q90=makeQuery(id+"F0.imprint","IMPRINT",FACE,{"disambiguationData":[TD([[makeQuery(id+"F0.imprint","IMPRINT",EDGE,{"derivedFrom":subQ0}),-1.0]])]});}
            var Q91;
            Q91=makeQuery(id+"F0.imprint","IMPRINT",FACE,{"disambiguationData":[TD([[makeQuery(id+"F0.imprint","IMPRINT",EDGE,{"derivedFrom":sQuery(id+"F0.wireOp",EDGE,"E9.11.5.2")}),-1.0]])]});
            var Q92;
            Q92=makeQuery(id+"F0.imprint","IMPRINT",FACE,{"disambiguationData":[TD([[makeQuery(id+"F0.imprint","IMPRINT",EDGE,{"derivedFrom":sQuery(id+"F0.wireOp",EDGE,"E9.11.5.3")}),1.0]])]});
            var Q93;
            {var subQ0=sQuery(id+"F0.wireOp",EDGE,"E9.6.6.1");Q93=makeQuery(id+"F0.imprint","IMPRINT",FACE,{"disambiguationData":[TD([[makeQuery(id+"F0.imprint","IMPRINT",EDGE,{"derivedFrom":subQ0}),1.0]])]});}
            var Q94;
            Q94=makeQuery(id+"F0.imprint","IMPRINT",FACE,{"disambiguationData":[TD([[makeQuery(id+"F0.imprint","IMPRINT",EDGE,{"derivedFrom":sQuery(id+"F0.wireOp",EDGE,"E9.7.5.3")}),1.0]])]});
            var Q95;
            {var subQ0=sQuery(id+"F0.wireOp",EDGE,"E9.7.5.5");Q95=makeQuery(id+"F0.imprint","IMPRINT",FACE,{"disambiguationData":[TD([[makeQuery(id+"F0.imprint","IMPRINT",EDGE,{"derivedFrom":subQ0}),-1.0]])]});}
            var Q96;
            Q96=makeQuery(id+"F0.imprint","IMPRINT",FACE,{"disambiguationData":[TD([[makeQuery(id+"F0.imprint","IMPRINT",EDGE,{"derivedFrom":sQuery(id+"F0.wireOp",EDGE,"E9.8.5.3")}),1.0]])]});
            var Q97;
            {var subQ0=sQuery(id+"F0.wireOp",EDGE,"E9.10.6.1");Q97=makeQuery(id+"F0.imprint","IMPRINT",FACE,{"disambiguationData":[TD([[makeQuery(id+"F0.imprint","IMPRINT",EDGE,{"derivedFrom":subQ0}),1.0]])]});}
            var Q98;
            {var subQ3=sQuery(id+"F0.wireOp",EDGE,"E9.4.3.5");var subQ5=sQuery(id+"F0.wireOp",EDGE,"E9.5.4.0");var subQ9=makeQuery(id+"F0.imprint","INTERSECT",VERTEX,{"derivedFrom":[subQ3,subQ5]});Q98=makeQuery(id+"F0.imprint","IMPRINT",FACE,{"disambiguationData":[TD([[makeQuery(id+"F0.imprint","IMPRINT",EDGE,{"disambiguationData":[TD([[subQ9,-1.0]])],"derivedFrom":subQ3}),-1.0]])]});}
            var Q99;
            {var subQ0=sQuery(id+"F0.wireOp",EDGE,"E9.4.4.3");Q99=makeQuery(id+"F0.imprint","IMPRINT",FACE,{"disambiguationData":[TD([[makeQuery(id+"F0.imprint","IMPRINT",EDGE,{"derivedFrom":subQ0}),-1.0]])]});}
            var Q100;
            {var subQ3=sQuery(id+"F0.wireOp",EDGE,"E9.3.4.5");var subQ5=sQuery(id+"F0.wireOp",EDGE,"E9.4.5.0");var subQ9=makeQuery(id+"F0.imprint","INTERSECT",VERTEX,{"derivedFrom":[subQ3,subQ5]});Q100=makeQuery(id+"F0.imprint","IMPRINT",FACE,{"disambiguationData":[TD([[makeQuery(id+"F0.imprint","IMPRINT",EDGE,{"disambiguationData":[TD([[subQ9,-1.0]])],"derivedFrom":subQ3}),-1.0]])]});}
            var Q101;
            {var subQ0=sQuery(id+"F0.wireOp",EDGE,"E9.4.5.3");Q101=makeQuery(id+"F0.imprint","IMPRINT",FACE,{"disambiguationData":[TD([[makeQuery(id+"F0.imprint","IMPRINT",EDGE,{"derivedFrom":subQ0}),-1.0]])]});}
            var Q102;
            {var subQ0=sQuery(id+"F0.wireOp",EDGE,"E9.5.6.3");Q102=makeQuery(id+"F0.imprint","IMPRINT",FACE,{"disambiguationData":[TD([[makeQuery(id+"F0.imprint","IMPRINT",EDGE,{"derivedFrom":subQ0}),-1.0]])]});}
            var Q103;
            {var subQ3=sQuery(id+"F0.wireOp",EDGE,"E9.4.5.5");var subQ5=sQuery(id+"F0.wireOp",EDGE,"E9.5.6.0");var subQ9=makeQuery(id+"F0.imprint","INTERSECT",VERTEX,{"derivedFrom":[subQ3,subQ5]});Q103=makeQuery(id+"F0.imprint","IMPRINT",FACE,{"disambiguationData":[TD([[makeQuery(id+"F0.imprint","IMPRINT",EDGE,{"disambiguationData":[TD([[subQ9,-1.0]])],"derivedFrom":subQ3}),-1.0]])]});}
            var Q104;
            {var subQ0=sQuery(id+"F0.wireOp",EDGE,"E9.6.6.3");Q104=makeQuery(id+"F0.imprint","IMPRINT",FACE,{"disambiguationData":[TD([[makeQuery(id+"F0.imprint","IMPRINT",EDGE,{"derivedFrom":subQ0}),-1.0]])]});}
            var Q105;
            {var subQ3=sQuery(id+"F0.wireOp",EDGE,"E9.6.5.5");var subQ5=sQuery(id+"F0.wireOp",EDGE,"E9.7.6.0");var subQ9=makeQuery(id+"F0.imprint","INTERSECT",VERTEX,{"derivedFrom":[subQ3,subQ5]});Q105=makeQuery(id+"F0.imprint","IMPRINT",FACE,{"disambiguationData":[TD([[makeQuery(id+"F0.imprint","IMPRINT",EDGE,{"disambiguationData":[TD([[subQ9,-1.0]])],"derivedFrom":subQ3}),-1.0]])]});}
            var Q106;
            {var subQ0=sQuery(id+"F0.wireOp",EDGE,"E9.7.6.3");Q106=makeQuery(id+"F0.imprint","IMPRINT",FACE,{"disambiguationData":[TD([[makeQuery(id+"F0.imprint","IMPRINT",EDGE,{"derivedFrom":subQ0}),-1.0]])]});}
            var Q107;
            {var subQ3=sQuery(id+"F0.wireOp",EDGE,"E9.7.5.5");var subQ5=sQuery(id+"F0.wireOp",EDGE,"E9.8.6.0");var subQ9=makeQuery(id+"F0.imprint","INTERSECT",VERTEX,{"derivedFrom":[subQ3,subQ5]});Q107=makeQuery(id+"F0.imprint","IMPRINT",FACE,{"disambiguationData":[TD([[makeQuery(id+"F0.imprint","IMPRINT",EDGE,{"disambiguationData":[TD([[subQ9,-1.0]])],"derivedFrom":subQ3}),-1.0]])]});}
            var Q108;
            {var subQ0=sQuery(id+"F0.wireOp",EDGE,"E9.8.6.3");Q108=makeQuery(id+"F0.imprint","IMPRINT",FACE,{"disambiguationData":[TD([[makeQuery(id+"F0.imprint","IMPRINT",EDGE,{"derivedFrom":subQ0}),-1.0]])]});}
            var Q109;
            {var subQ3=sQuery(id+"F0.wireOp",EDGE,"E9.8.5.5");var subQ5=sQuery(id+"F0.wireOp",EDGE,"E9.9.6.0");var subQ9=makeQuery(id+"F0.imprint","INTERSECT",VERTEX,{"derivedFrom":[subQ3,subQ5]});Q109=makeQuery(id+"F0.imprint","IMPRINT",FACE,{"disambiguationData":[TD([[makeQuery(id+"F0.imprint","IMPRINT",EDGE,{"disambiguationData":[TD([[subQ9,-1.0]])],"derivedFrom":subQ3}),-1.0]])]});}
            var Q110;
            {var subQ0=sQuery(id+"F0.wireOp",EDGE,"E9.5.4.3");Q110=makeQuery(id+"F0.imprint","IMPRINT",FACE,{"disambiguationData":[TD([[makeQuery(id+"F0.imprint","IMPRINT",EDGE,{"derivedFrom":subQ0}),-1.0]])]});}
            var Q111;
            {var subQ0=sQuery(id+"F0.wireOp",EDGE,"E9.6.4.3");Q111=makeQuery(id+"F0.imprint","IMPRINT",FACE,{"disambiguationData":[TD([[makeQuery(id+"F0.imprint","IMPRINT",EDGE,{"derivedFrom":subQ0}),-1.0]])]});}
            var Q112;
            {var subQ0=sQuery(id+"F0.wireOp",EDGE,"E9.7.4.3");Q112=makeQuery(id+"F0.imprint","IMPRINT",FACE,{"disambiguationData":[TD([[makeQuery(id+"F0.imprint","IMPRINT",EDGE,{"derivedFrom":subQ0}),-1.0]])]});}
            var Q113;
            {var subQ3=sQuery(id+"F0.wireOp",EDGE,"E9.8.3.5");var subQ5=sQuery(id+"F0.wireOp",EDGE,"E9.9.4.0");var subQ9=makeQuery(id+"F0.imprint","INTERSECT",VERTEX,{"derivedFrom":[subQ3,subQ5]});Q113=makeQuery(id+"F0.imprint","IMPRINT",FACE,{"disambiguationData":[TD([[makeQuery(id+"F0.imprint","IMPRINT",EDGE,{"disambiguationData":[TD([[subQ9,-1.0]])],"derivedFrom":subQ3}),-1.0]])]});}
            var Q114;
            {var subQ3=sQuery(id+"F0.wireOp",EDGE,"E9.7.4.5");var subQ5=sQuery(id+"F0.wireOp",EDGE,"E9.8.5.0");var subQ9=makeQuery(id+"F0.imprint","INTERSECT",VERTEX,{"derivedFrom":[subQ3,subQ5]});Q114=makeQuery(id+"F0.imprint","IMPRINT",FACE,{"disambiguationData":[TD([[makeQuery(id+"F0.imprint","IMPRINT",EDGE,{"disambiguationData":[TD([[subQ9,-1.0]])],"derivedFrom":subQ3}),-1.0]])]});}
            var Q115;
            {var subQ3=sQuery(id+"F0.wireOp",EDGE,"E9.6.4.5");var subQ5=sQuery(id+"F0.wireOp",EDGE,"E9.7.5.0");var subQ9=makeQuery(id+"F0.imprint","INTERSECT",VERTEX,{"derivedFrom":[subQ3,subQ5]});Q115=makeQuery(id+"F0.imprint","IMPRINT",FACE,{"disambiguationData":[TD([[makeQuery(id+"F0.imprint","IMPRINT",EDGE,{"disambiguationData":[TD([[subQ9,-1.0]])],"derivedFrom":subQ3}),-1.0]])]});}
            var Q116;
            {var subQ0=sQuery(id+"F0.wireOp",EDGE,"E9.6.5.3");Q116=makeQuery(id+"F0.imprint","IMPRINT",FACE,{"disambiguationData":[TD([[makeQuery(id+"F0.imprint","IMPRINT",EDGE,{"derivedFrom":subQ0}),-1.0]])]});}
            var Q117;
            {var subQ0=sQuery(id+"F0.wireOp",EDGE,"E9.9.4.3");Q117=makeQuery(id+"F0.imprint","IMPRINT",FACE,{"disambiguationData":[TD([[makeQuery(id+"F0.imprint","IMPRINT",EDGE,{"derivedFrom":subQ0}),-1.0]])]});}
            var Q118;
            {var subQ3=sQuery(id+"F0.wireOp",EDGE,"E9.9.4.5");var subQ5=sQuery(id+"F0.wireOp",EDGE,"E9.10.5.0");var subQ9=makeQuery(id+"F0.imprint","INTERSECT",VERTEX,{"derivedFrom":[subQ3,subQ5]});Q118=makeQuery(id+"F0.imprint","IMPRINT",FACE,{"disambiguationData":[TD([[makeQuery(id+"F0.imprint","IMPRINT",EDGE,{"disambiguationData":[TD([[subQ9,-1.0]])],"derivedFrom":subQ3}),-1.0]])]});}
            var Q119;
            {var subQ3=sQuery(id+"F0.wireOp",EDGE,"E9.2.5.5");var subQ5=sQuery(id+"F0.wireOp",EDGE,"E9.3.6.0");var subQ9=makeQuery(id+"F0.imprint","INTERSECT",VERTEX,{"derivedFrom":[subQ3,subQ5]});Q119=makeQuery(id+"F0.imprint","IMPRINT",FACE,{"disambiguationData":[TD([[makeQuery(id+"F0.imprint","IMPRINT",EDGE,{"disambiguationData":[TD([[subQ9,-1.0]])],"derivedFrom":subQ3}),-1.0]])]});}
            var Q120;
            {var subQ0=sQuery(id+"F0.wireOp",EDGE,"E9.3.6.3");Q120=makeQuery(id+"F0.imprint","IMPRINT",FACE,{"disambiguationData":[TD([[makeQuery(id+"F0.imprint","IMPRINT",EDGE,{"derivedFrom":subQ0}),-1.0]])]});}
            var Q121;
            {var subQ3=sQuery(id+"F0.wireOp",EDGE,"E9.3.2.5");var subQ5=sQuery(id+"F0.wireOp",EDGE,"E9.4.3.0");var subQ9=makeQuery(id+"F0.imprint","INTERSECT",VERTEX,{"derivedFrom":[subQ3,subQ5]});Q121=makeQuery(id+"F0.imprint","IMPRINT",FACE,{"disambiguationData":[TD([[makeQuery(id+"F0.imprint","IMPRINT",EDGE,{"disambiguationData":[TD([[subQ9,-1.0]])],"derivedFrom":subQ3}),-1.0]])]});}
            var Q122;
            {var subQ0=sQuery(id+"F0.wireOp",EDGE,"E9.4.3.3");Q122=makeQuery(id+"F0.imprint","IMPRINT",FACE,{"disambiguationData":[TD([[makeQuery(id+"F0.imprint","IMPRINT",EDGE,{"derivedFrom":subQ0}),-1.0]])]});}
            var Q123;
            {var subQ3=sQuery(id+"F0.wireOp",EDGE,"E9.4.2.5");var subQ5=sQuery(id+"F0.wireOp",EDGE,"E9.5.3.0");var subQ9=makeQuery(id+"F0.imprint","INTERSECT",VERTEX,{"derivedFrom":[subQ3,subQ5]});Q123=makeQuery(id+"F0.imprint","IMPRINT",FACE,{"disambiguationData":[TD([[makeQuery(id+"F0.imprint","IMPRINT",EDGE,{"disambiguationData":[TD([[subQ9,-1.0]])],"derivedFrom":subQ3}),-1.0]])]});}
            var Q124;
            {var subQ0=sQuery(id+"F0.wireOp",EDGE,"E9.5.3.3");Q124=makeQuery(id+"F0.imprint","IMPRINT",FACE,{"disambiguationData":[TD([[makeQuery(id+"F0.imprint","IMPRINT",EDGE,{"derivedFrom":subQ0}),-1.0]])]});}
            var Q125;
            {var subQ0=sQuery(id+"F0.wireOp",EDGE,"E9.8.3.3");Q125=makeQuery(id+"F0.imprint","IMPRINT",FACE,{"disambiguationData":[TD([[makeQuery(id+"F0.imprint","IMPRINT",EDGE,{"derivedFrom":subQ0}),-1.0]])]});}
            var Q126;
            {var subQ3=sQuery(id+"F0.wireOp",EDGE,"E9.8.2.5");var subQ5=sQuery(id+"F0.wireOp",EDGE,"E9.9.3.0");var subQ9=makeQuery(id+"F0.imprint","INTERSECT",VERTEX,{"derivedFrom":[subQ3,subQ5]});Q126=makeQuery(id+"F0.imprint","IMPRINT",FACE,{"disambiguationData":[TD([[makeQuery(id+"F0.imprint","IMPRINT",EDGE,{"disambiguationData":[TD([[subQ9,-1.0]])],"derivedFrom":subQ3}),-1.0]])]});}
            var Q127;
            {var subQ0=sQuery(id+"F0.wireOp",EDGE,"E9.9.3.3");Q127=makeQuery(id+"F0.imprint","IMPRINT",FACE,{"disambiguationData":[TD([[makeQuery(id+"F0.imprint","IMPRINT",EDGE,{"derivedFrom":subQ0}),-1.0]])]});}
            var Q128;
            {var subQ3=sQuery(id+"F0.wireOp",EDGE,"E9.9.2.5");var subQ5=sQuery(id+"F0.wireOp",EDGE,"E9.10.3.0");var subQ9=makeQuery(id+"F0.imprint","INTERSECT",VERTEX,{"derivedFrom":[subQ3,subQ5]});Q128=makeQuery(id+"F0.imprint","IMPRINT",FACE,{"disambiguationData":[TD([[makeQuery(id+"F0.imprint","IMPRINT",EDGE,{"disambiguationData":[TD([[subQ9,-1.0]])],"derivedFrom":subQ3}),-1.0]])]});}
            var Q129;
            {var subQ0=sQuery(id+"F0.wireOp",EDGE,"E9.4.2.3");Q129=makeQuery(id+"F0.imprint","IMPRINT",FACE,{"disambiguationData":[TD([[makeQuery(id+"F0.imprint","IMPRINT",EDGE,{"derivedFrom":subQ0}),-1.0]])]});}
            var Q130;
            {var subQ0=sQuery(id+"F0.wireOp",EDGE,"E9.6.3.3");Q130=makeQuery(id+"F0.imprint","IMPRINT",FACE,{"disambiguationData":[TD([[makeQuery(id+"F0.imprint","IMPRINT",EDGE,{"derivedFrom":subQ0}),-1.0]])]});}
            var Q131;
            {var subQ3=sQuery(id+"F0.wireOp",EDGE,"E9.6.2.5");var subQ5=sQuery(id+"F0.wireOp",EDGE,"E9.7.3.0");var subQ9=makeQuery(id+"F0.imprint","INTERSECT",VERTEX,{"derivedFrom":[subQ3,subQ5]});Q131=makeQuery(id+"F0.imprint","IMPRINT",FACE,{"disambiguationData":[TD([[makeQuery(id+"F0.imprint","IMPRINT",EDGE,{"disambiguationData":[TD([[subQ9,-1.0]])],"derivedFrom":subQ3}),-1.0]])]});}
            var Q132;
            {var subQ0=sQuery(id+"F0.wireOp",EDGE,"E9.7.3.3");Q132=makeQuery(id+"F0.imprint","IMPRINT",FACE,{"disambiguationData":[TD([[makeQuery(id+"F0.imprint","IMPRINT",EDGE,{"derivedFrom":subQ0}),-1.0]])]});}
            var Q133;
            {var subQ0=sQuery(id+"F0.wireOp",EDGE,"E9.9.2.3");Q133=makeQuery(id+"F0.imprint","IMPRINT",FACE,{"disambiguationData":[TD([[makeQuery(id+"F0.imprint","IMPRINT",EDGE,{"derivedFrom":subQ0}),-1.0]])]});}
            var Q134;
            {var subQ0=sQuery(id+"F0.wireOp",EDGE,"E9.2.5.3");Q134=makeQuery(id+"F0.imprint","IMPRINT",FACE,{"disambiguationData":[TD([[makeQuery(id+"F0.imprint","IMPRINT",EDGE,{"derivedFrom":subQ0}),-1.0]])]});}
            var Q135;
            {var subQ3=sQuery(id+"F0.wireOp",EDGE,"E9.3.5.5");var subQ5=sQuery(id+"F0.wireOp",EDGE,"E9.4.6.0");var subQ9=makeQuery(id+"F0.imprint","INTERSECT",VERTEX,{"derivedFrom":[subQ3,subQ5]});Q135=makeQuery(id+"F0.imprint","IMPRINT",FACE,{"disambiguationData":[TD([[makeQuery(id+"F0.imprint","IMPRINT",EDGE,{"disambiguationData":[TD([[subQ9,-1.0]])],"derivedFrom":subQ3}),-1.0]])]});}
            var Q136;
            {var subQ0=sQuery(id+"F0.wireOp",EDGE,"E9.4.6.3");Q136=makeQuery(id+"F0.imprint","IMPRINT",FACE,{"disambiguationData":[TD([[makeQuery(id+"F0.imprint","IMPRINT",EDGE,{"derivedFrom":subQ0}),-1.0]])]});}
            var Q137;
            {var subQ0=sQuery(id+"F0.wireOp",EDGE,"E9.9.5.3");Q137=makeQuery(id+"F0.imprint","IMPRINT",FACE,{"disambiguationData":[TD([[makeQuery(id+"F0.imprint","IMPRINT",EDGE,{"derivedFrom":subQ0}),-1.0]])]});}
            var Q138;
            {var subQ0=sQuery(id+"F0.wireOp",EDGE,"E9.9.6.3");Q138=makeQuery(id+"F0.imprint","IMPRINT",FACE,{"disambiguationData":[TD([[makeQuery(id+"F0.imprint","IMPRINT",EDGE,{"derivedFrom":subQ0}),-1.0]])]});}
            var Q139;
            {var subQ0=sQuery(id+"F0.wireOp",EDGE,"E9.10.6.3");Q139=makeQuery(id+"F0.imprint","IMPRINT",FACE,{"disambiguationData":[TD([[makeQuery(id+"F0.imprint","IMPRINT",EDGE,{"derivedFrom":subQ0}),-1.0]])]});}
            var Q140;
            {var subQ3=sQuery(id+"F0.wireOp",EDGE,"E9.10.5.5");var subQ5=sQuery(id+"F0.wireOp",EDGE,"E9.11.6.0");var subQ9=makeQuery(id+"F0.imprint","INTERSECT",VERTEX,{"derivedFrom":[subQ3,subQ5]});Q140=makeQuery(id+"F0.imprint","IMPRINT",FACE,{"disambiguationData":[TD([[makeQuery(id+"F0.imprint","IMPRINT",EDGE,{"disambiguationData":[TD([[subQ9,-1.0]])],"derivedFrom":subQ3}),-1.0]])]});}
            var Q141;
            {var subQ0=sQuery(id+"F0.wireOp",EDGE,"E9.6.7.3");Q141=makeQuery(id+"F0.imprint","IMPRINT",FACE,{"disambiguationData":[TD([[makeQuery(id+"F0.imprint","IMPRINT",EDGE,{"derivedFrom":subQ0}),-1.0]])]});}
            var Q142;
            {var subQ3=sQuery(id+"F0.wireOp",EDGE,"E9.6.6.5");var subQ5=sQuery(id+"F0.wireOp",EDGE,"E9.7.7.0");var subQ9=makeQuery(id+"F0.imprint","INTERSECT",VERTEX,{"derivedFrom":[subQ3,subQ5]});Q142=makeQuery(id+"F0.imprint","IMPRINT",FACE,{"disambiguationData":[TD([[makeQuery(id+"F0.imprint","IMPRINT",EDGE,{"disambiguationData":[TD([[subQ9,-1.0]])],"derivedFrom":subQ3}),-1.0]])]});}
            var Q143;
            {var subQ0=sQuery(id+"F0.wireOp",EDGE,"E9.7.7.3");Q143=makeQuery(id+"F0.imprint","IMPRINT",FACE,{"disambiguationData":[TD([[makeQuery(id+"F0.imprint","IMPRINT",EDGE,{"derivedFrom":subQ0}),-1.0]])]});}
            var Q144;
            {var subQ0=sQuery(id+"F0.wireOp",EDGE,"E9.11.5.3");Q144=makeQuery(id+"F0.imprint","IMPRINT",FACE,{"disambiguationData":[TD([[makeQuery(id+"F0.imprint","IMPRINT",EDGE,{"derivedFrom":subQ0}),-1.0]])]});}
            var Q145;
            Q145=makeQuery(id+"F0.imprint","IMPRINT",FACE,{"disambiguationData":[TD([[makeQuery(id+"F0.imprint","IMPRINT",EDGE,{"derivedFrom":sQuery(id+"F0.wireOp",EDGE,"E9.7.4.0")}),1.0]])]});
            extrude(context, id + "F1", {"entities" : qUnion([Q0, Q1, Q2, Q3, Q4, Q5, Q6, Q7, Q8, Q9, Q10, Q11, Q12, Q13, Q14, Q15, Q16, Q17, Q18, Q19, Q20, Q21, Q22, Q23, Q24, Q25, Q26, Q27, Q28, Q29, Q30, Q31, Q32, Q33, Q34, Q35, Q36, Q37, Q38, Q39, Q40, Q41, Q42, Q43, Q44, Q45, Q46, Q47, Q48, Q49, Q50, Q51, Q52, Q53, Q54, Q55, Q56, Q57, Q58, Q59, Q60, Q61, Q62, Q63, Q64, Q65, Q66, Q67, Q68, Q69, Q70, Q71, Q72, Q73, Q74, Q75, Q76, Q77, Q78, Q79, Q80, Q81, Q82, Q83, Q84, Q85, Q86, Q87, Q88, Q89, Q90, Q91, Q92, Q93, Q94, Q95, Q96, Q97, Q98, Q99, Q100, Q101, Q102, Q103, Q104, Q105, Q106, Q107, Q108, Q109, Q110, Q111, Q112, Q113, Q114, Q115, Q116, Q117, Q118, Q119, Q120, Q121, Q122, Q123, Q124, Q125, Q126, Q127, Q128, Q129, Q130, Q131, Q132, Q133, Q134, Q135, Q136, Q137, Q138, Q139, Q140, Q141, Q142, Q143, Q144, Q145]), "depth" : 1 * mm, "offsetDistance" : 25 * mm});
        }
        {
            var Q0;
            Q0=makeQuery(id+"F1.opExtrude","CAP_FACE",FACE,{"disambiguationData":[OSD([sQuery(id+"F0.wireOp",EDGE,"E9.2.5.2"),sQuery(id+"F0.wireOp",EDGE,"E9.2.5.4"),sQuery(id+"F0.wireOp",EDGE,"E9.2.6.0"),sQuery(id+"F0.wireOp",EDGE,"E9.3.2.5"),sQuery(id+"F0.wireOp",EDGE,"E9.3.3.0"),sQuery(id+"F0.wireOp",EDGE,"E9.3.4.5"),sQuery(id+"F0.wireOp",EDGE,"E9.3.5.0"),sQuery(id+"F0.wireOp",EDGE,"E9.3.5.1"),sQuery(id+"F0.wireOp",EDGE,"E9.3.5.4"),sQuery(id+"F0.wireOp",EDGE,"E9.3.6.0"),sQuery(id+"F0.wireOp",EDGE,"E9.3.6.1"),sQuery(id+"F0.wireOp",EDGE,"E9.3.6.4"),sQuery(id+"F0.wireOp",EDGE,"E9.3.7.0"),sQuery(id+"F0.wireOp",EDGE,"E9.4.2.2"),sQuery(id+"F0.wireOp",EDGE,"E9.4.3.1"),sQuery(id+"F0.wireOp",EDGE,"E9.4.3.3"),sQuery(id+"F0.wireOp",EDGE,"E9.4.3.5"),sQuery(id+"F0.wireOp",EDGE,"E9.4.4.0"),sQuery(id+"F0.wireOp",EDGE,"E9.4.4.2"),sQuery(id+"F0.wireOp",EDGE,"E9.4.4.5"),sQuery(id+"F0.wireOp",EDGE,"E9.4.5.0"),sQuery(id+"F0.wireOp",EDGE,"E9.4.5.1"),sQuery(id+"F0.wireOp",EDGE,"E9.4.5.4"),sQuery(id+"F0.wireOp",EDGE,"E9.4.6.0"),sQuery(id+"F0.wireOp",EDGE,"E9.4.6.5"),sQuery(id+"F0.wireOp",EDGE,"E9.4.7.0"),sQuery(id+"F0.wireOp",EDGE,"E9.5.2.1"),sQuery(id+"F0.wireOp",EDGE,"E9.5.2.4"),sQuery(id+"F0.wireOp",EDGE,"E9.5.3.0"),sQuery(id+"F0.wireOp",EDGE,"E9.5.4.3"),sQuery(id+"F0.wireOp",EDGE,"E9.5.5.1"),sQuery(id+"F0.wireOp",EDGE,"E9.5.5.4"),sQuery(id+"F0.wireOp",EDGE,"E9.5.6.0"),sQuery(id+"F0.wireOp",EDGE,"E9.5.6.4"),sQuery(id+"F0.wireOp",EDGE,"E9.5.7.0"),sQuery(id+"F0.wireOp",EDGE,"E9.6.2.5"),sQuery(id+"F0.wireOp",EDGE,"E9.6.3.0"),sQuery(id+"F0.wireOp",EDGE,"E9.6.4.4"),sQuery(id+"F0.wireOp",EDGE,"E9.6.5.0"),sQuery(id+"F0.wireOp",EDGE,"E9.6.5.1"),sQuery(id+"F0.wireOp",EDGE,"E9.6.5.4"),sQuery(id+"F0.wireOp",EDGE,"E9.6.6.0"),sQuery(id+"F0.wireOp",EDGE,"E9.6.7.0"),sQuery(id+"F0.wireOp",EDGE,"E9.6.7.2"),sQuery(id+"F0.wireOp",EDGE,"E9.6.7.4"),sQuery(id+"F0.wireOp",EDGE,"E9.6.8.0"),sQuery(id+"F0.wireOp",EDGE,"E9.7.2.4"),sQuery(id+"F0.wireOp",EDGE,"E9.7.3.0"),sQuery(id+"F0.wireOp",EDGE,"E9.7.4.0"),sQuery(id+"F0.wireOp",EDGE,"E9.7.4.1"),sQuery(id+"F0.wireOp",EDGE,"E9.7.4.3"),sQuery(id+"F0.wireOp",EDGE,"E9.7.7.5"),sQuery(id+"F0.wireOp",EDGE,"E9.7.8.0"),sQuery(id+"F0.wireOp",EDGE,"E9.8.2.5"),sQuery(id+"F0.wireOp",EDGE,"E9.8.3.0"),sQuery(id+"F0.wireOp",EDGE,"E9.8.4.0"),sQuery(id+"F0.wireOp",EDGE,"E9.8.4.4"),sQuery(id+"F0.wireOp",EDGE,"E9.8.5.0"),sQuery(id+"F0.wireOp",EDGE,"E9.8.5.1"),sQuery(id+"F0.wireOp",EDGE,"E9.8.5.3"),sQuery(id+"F0.wireOp",EDGE,"E9.8.6.5"),sQuery(id+"F0.wireOp",EDGE,"E9.8.7.0"),sQuery(id+"F0.wireOp",EDGE,"E9.8.7.1"),sQuery(id+"F0.wireOp",EDGE,"E9.9.2.2"),sQuery(id+"F0.wireOp",EDGE,"E9.9.3.3"),sQuery(id+"F0.wireOp",EDGE,"E9.9.3.4"),sQuery(id+"F0.wireOp",EDGE,"E9.9.4.0"),sQuery(id+"F0.wireOp",EDGE,"E9.9.4.1"),sQuery(id+"F0.wireOp",EDGE,"E9.9.4.4"),sQuery(id+"F0.wireOp",EDGE,"E9.9.5.0"),sQuery(id+"F0.wireOp",EDGE,"E9.9.5.2"),sQuery(id+"F0.wireOp",EDGE,"E9.9.5.5"),sQuery(id+"F0.wireOp",EDGE,"E9.9.6.0"),sQuery(id+"F0.wireOp",EDGE,"E9.9.6.4"),sQuery(id+"F0.wireOp",EDGE,"E9.9.7.0"),sQuery(id+"F0.wireOp",EDGE,"E9.10.2.1"),sQuery(id+"F0.wireOp",EDGE,"E9.10.2.4"),sQuery(id+"F0.wireOp",EDGE,"E9.10.3.0"),sQuery(id+"F0.wireOp",EDGE,"E9.10.3.2"),sQuery(id+"F0.wireOp",EDGE,"E9.10.4.1"),sQuery(id+"F0.wireOp",EDGE,"E9.10.4.4"),sQuery(id+"F0.wireOp",EDGE,"E9.10.5.0"),sQuery(id+"F0.wireOp",EDGE,"E9.10.5.2"),sQuery(id+"F0.wireOp",EDGE,"E9.10.5.5"),sQuery(id+"F0.wireOp",EDGE,"E9.10.6.0"),sQuery(id+"F0.wireOp",EDGE,"E9.10.6.5"),sQuery(id+"F0.wireOp",EDGE,"E9.10.7.0"),sQuery(id+"F0.wireOp",EDGE,"E9.11.5.2"),sQuery(id+"F0.wireOp",EDGE,"E9.11.5.5"),sQuery(id+"F0.wireOp",EDGE,"E9.11.6.0"),sQuery(id+"F0.wireOp",EDGE,"E9.11.6.2"),sQuery(id+"F0.wireOp",EDGE,"E9.12.5.1")])],"isStart":false});
            var sketch = newSketch(context, id + "F2", { "sketchPlane" : qUnion([Q0])});
            skLineSegment(sketch, "E10", {"start": v(5.05, 48.46) * mm, "end": v(5.05, 43.27) * mm});
            skLineSegment(sketch, "E11", {"start": v(8.05, 43.27) * mm, "end": v(8.05, 48.46) * mm});
            skLineSegment(sketch, "E12", {"start": v(8.05, 43.27) * mm, "end": v(5.05, 43.27) * mm});
            skSolve(sketch);
        }
        {
            var Q0;
            Q0 = qSketchRegion(id + "F2", true);
            var Q1;
            Q1=makeQuery(id+"F2.imprint","IMPRINT",FACE,{"disambiguationData":[TD([[makeQuery(id+"F2.imprint","IMPRINT",EDGE,{"derivedFrom":sQuery(id+"F2.wireOp",EDGE,"E10")}),1.0]])]});
            extrude(context, id + "F3", {"entities" : qUnion([Q0, Q1]), "operationType" : NewBodyOperationType.ADD, "depth" : 2.5 * mm, "offsetDistance" : 25 * mm});
        }
        {
            var Q0;
            Q0=makeQuery(id+"F3.opExtrude","CAP_EDGE",EDGE,{"disambiguationData":[OSD([sQuery(id+"F2.wireOp",EDGE,"E12")])],"isStart":false});
            var Q1;
            Q1=makeQuery(id+"F3.opExtrude","CAP_EDGE",EDGE,{"disambiguationData":[OSD([sQuery(id+"F0.wireOp",EDGE,"E9.6.8.0"),sQuery(id+"F0.wireOp",EDGE,"E9.7.8.0")])],"isStart":false});
            chamfer(context, id + "F4", {"entities" : qUnion([Q0, Q1]), "width" : 1.5 * mm, "tangentPropagation" : true});
        }
        {
            var Q0;
            Q0=makeQuery(id+"F3.opExtrude","SWEPT_FACE",FACE,{"disambiguationData":[OSD([sQuery(id+"F2.wireOp",EDGE,"E11")])]});
            var sketch = newSketch(context, id + "F5", { "sketchPlane" : qUnion([Q0])});
            skLineSegment(sketch, "E13.0", {"start": v(43.87, 1.75) * mm, "end": v(43.87, 1) * mm});
            skLineSegment(sketch, "E13.1", {"start": v(47.86, 1.75) * mm, "end": v(47.86, 1) * mm});
            skLineSegment(sketch, "E13.2", {"start": v(47.86, 1.75) * mm, "end": v(46.72, 2.9) * mm});
            skLineSegment(sketch, "E13.3", {"start": v(45.02, 2.9) * mm, "end": v(46.72, 2.9) * mm});
            skLineSegment(sketch, "E13.4", {"start": v(45.02, 2.9) * mm, "end": v(43.87, 1.75) * mm});
            skSolve(sketch);
        }
        {
            var Q0;
            {var subQ1=sQuery(id+"F5.wireOp",EDGE,"E13.0");Q0=makeQuery(id+"F5.imprint","IMPRINT",FACE,{"disambiguationData":[TD([[makeQuery(id+"F5.imprint","IMPRINT",EDGE,{"derivedFrom":subQ1}),1.0]])]});}
            extrude(context, id + "F6", {"entities" : qUnion([Q0]), "operationType" : NewBodyOperationType.REMOVE, "oppositeDirection" : true, "depth" : 25 * mm, "offsetDistance" : 25 * mm});
        }
        {
            var Q0;
            {var subQ0=sQuery(id+"F0.wireOp",EDGE,"E9.10.2.4");var subQ1=sQuery(id+"F0.wireOp",EDGE,"E9.10.2.1");var subQ2=sQuery(id+"F0.wireOp",EDGE,"E9.10.5.2");var subQ3=sQuery(id+"F0.wireOp",EDGE,"E9.9.5.5");var subQ4=sQuery(id+"F0.wireOp",EDGE,"E9.9.5.2");var subQ5=sQuery(id+"F0.wireOp",EDGE,"E9.10.4.4");var subQ6=sQuery(id+"F0.wireOp",EDGE,"E9.10.4.1");var subQ7=sQuery(id+"F0.wireOp",EDGE,"E9.9.3.4");var subQ8=sQuery(id+"F0.wireOp",EDGE,"E9.9.3.3");var subQ9=sQuery(id+"F0.wireOp",EDGE,"E9.8.7.1");var subQ10=sQuery(id+"F0.wireOp",EDGE,"E9.8.7.0");var subQ11=sQuery(id+"F0.wireOp",EDGE,"E9.8.6.5");var subQ12=sQuery(id+"F0.wireOp",EDGE,"E9.8.5.0");var subQ13=sQuery(id+"F0.wireOp",EDGE,"E9.8.4.4");var subQ14=sQuery(id+"F0.wireOp",EDGE,"E9.8.4.1");var subQ15=sQuery(id+"F0.wireOp",EDGE,"E9.9.4.4");var subQ16=sQuery(id+"F0.wireOp",EDGE,"E9.9.4.1");var subQ17=sQuery(id+"F0.wireOp",EDGE,"E9.8.3.4");var subQ18=sQuery(id+"F0.wireOp",EDGE,"E9.8.3.0");var subQ19=sQuery(id+"F0.wireOp",EDGE,"E9.9.2.2");var subQ20=sQuery(id+"F0.wireOp",EDGE,"E9.8.2.5");var subQ21=sQuery(id+"F0.wireOp",EDGE,"E9.8.5.3");var subQ22=sQuery(id+"F0.wireOp",EDGE,"E9.7.5.3");var subQ23=sQuery(id+"F0.wireOp",EDGE,"E9.7.5.2");var subQ24=sQuery(id+"F0.wireOp",EDGE,"E9.7.2.4");var subQ25=sQuery(id+"F0.wireOp",EDGE,"E9.6.7.2");var subQ26=sQuery(id+"F0.wireOp",EDGE,"E9.6.7.0");var subQ27=sQuery(id+"F0.wireOp",EDGE,"E9.6.6.0");var subQ28=sQuery(id+"F0.wireOp",EDGE,"E9.6.5.4");var subQ29=sQuery(id+"F0.wireOp",EDGE,"E9.6.5.1");var subQ30=sQuery(id+"F0.wireOp",EDGE,"E9.6.5.0");var subQ31=sQuery(id+"F0.wireOp",EDGE,"E9.6.4.5");var subQ32=sQuery(id+"F0.wireOp",EDGE,"E9.4.4.5");var subQ33=sQuery(id+"F0.wireOp",EDGE,"E9.4.3.3");var subQ34=sQuery(id+"F0.wireOp",EDGE,"E9.4.3.1");var subQ35=sQuery(id+"F0.wireOp",EDGE,"E9.3.5.5");var subQ36=sQuery(id+"F0.wireOp",EDGE,"E9.3.5.4");var subQ37=sQuery(id+"F0.wireOp",EDGE,"E9.3.5.1");var subQ38=sQuery(id+"F0.wireOp",EDGE,"E9.4.4.2");var subQ39=sQuery(id+"F0.wireOp",EDGE,"E9.4.3.5");var subQ40=sQuery(id+"F0.wireOp",EDGE,"E9.3.4.5");var subQ41=sQuery(id+"F0.wireOp",EDGE,"E9.9.6.4");var subQ42=sQuery(id+"F0.wireOp",EDGE,"E9.2.5.2");var subQ43=sQuery(id+"F0.wireOp",EDGE,"E9.10.3.2");var subQ44=sQuery(id+"F0.wireOp",EDGE,"E9.12.5.1");var subQ45=sQuery(id+"F0.wireOp",EDGE,"E9.11.6.2");var subQ46=sQuery(id+"F0.wireOp",EDGE,"E9.11.5.5");var subQ47=sQuery(id+"F0.wireOp",EDGE,"E9.11.5.2");var subQ48=sQuery(id+"F0.wireOp",EDGE,"E9.10.7.0");var subQ49=sQuery(id+"F0.wireOp",EDGE,"E9.10.6.5");var subQ50=sQuery(id+"F0.wireOp",EDGE,"E9.10.6.0");var subQ51=sQuery(id+"F0.wireOp",EDGE,"E9.10.5.5");var subQ52=sQuery(id+"F0.wireOp",EDGE,"E9.7.4.0");var subQ53=sQuery(id+"F0.wireOp",EDGE,"E9.7.3.3");var subQ54=sQuery(id+"F0.wireOp",EDGE,"E9.6.4.3");var subQ55=sQuery(id+"F0.wireOp",EDGE,"E9.6.4.0");var subQ56=sQuery(id+"F0.wireOp",EDGE,"E9.6.3.3");var subQ57=sQuery(id+"F0.wireOp",EDGE,"E9.6.3.0");var subQ58=sQuery(id+"F0.wireOp",EDGE,"E9.6.2.5");var subQ59=sQuery(id+"F0.wireOp",EDGE,"E9.5.6.4");var subQ60=sQuery(id+"F0.wireOp",EDGE,"E9.5.5.4");var subQ61=sQuery(id+"F0.wireOp",EDGE,"E9.5.5.1");var subQ62=sQuery(id+"F0.wireOp",EDGE,"E9.5.4.3");var subQ63=sQuery(id+"F0.wireOp",EDGE,"E9.5.3.5");var subQ64=sQuery(id+"F0.wireOp",EDGE,"E9.5.2.4");var subQ65=sQuery(id+"F0.wireOp",EDGE,"E9.5.2.1");var subQ66=sQuery(id+"F0.wireOp",EDGE,"E9.4.7.0");var subQ67=sQuery(id+"F0.wireOp",EDGE,"E9.4.6.5");var subQ68=sQuery(id+"F0.wireOp",EDGE,"E9.4.5.1");var subQ69=sQuery(id+"F0.wireOp",EDGE,"E9.4.2.2");var subQ70=sQuery(id+"F0.wireOp",EDGE,"E9.3.6.4");var subQ71=sQuery(id+"F0.wireOp",EDGE,"E9.3.6.1");var subQ72=sQuery(id+"F0.wireOp",EDGE,"E9.3.2.5");var subQ73=sQuery(id+"F0.wireOp",EDGE,"E9.2.5.4");var subQ74=makeQuery(id+"F1.opExtrude","CAP_FACE",FACE,{"disambiguationData":[OSD([subQ42,subQ73,subQ72,subQ40,subQ37,subQ36,subQ35,subQ71,subQ70,subQ69,subQ34,subQ33,subQ39,subQ38,subQ32,subQ68,subQ67,subQ66,subQ65,subQ64,subQ63,subQ62,subQ61,subQ60,subQ59,subQ58,subQ57,subQ56,subQ55,subQ54,subQ31,subQ30,subQ29,subQ28,subQ27,subQ26,subQ25,sQuery(id+"F0.wireOp",EDGE,"E9.6.7.4"),subQ24,subQ53,subQ52,subQ23,subQ22,sQuery(id+"F0.wireOp",EDGE,"E9.7.7.5"),sQuery(id+"F0.wireOp",EDGE,"E9.7.8.0"),subQ20,subQ18,subQ17,subQ14,subQ13,subQ12,subQ21,subQ11,subQ10,subQ9,subQ19,subQ8,subQ7,subQ16,subQ15,subQ4,subQ3,subQ41,subQ1,subQ0,subQ43,subQ6,subQ5,subQ2,subQ51,subQ50,subQ49,subQ48,subQ47,subQ46,subQ45,subQ44])],"isStart":false});Q0=makeQuery(id+"F3.boolean.opBoolean","SPLIT",FACE,{"disambiguationData":[TD([makeQuery(id+"F1.opExtrude","SWEPT_FACE",FACE,{"disambiguationData":[OSD([subQ42])]})])],"derivedFrom":subQ74});}
            extrude(context, id + "F7", {"entities" : qUnion([Q0]), "operationType" : NewBodyOperationType.ADD, "depth" : 1 * mm, "offsetDistance" : 25 * mm});
        }
    });
